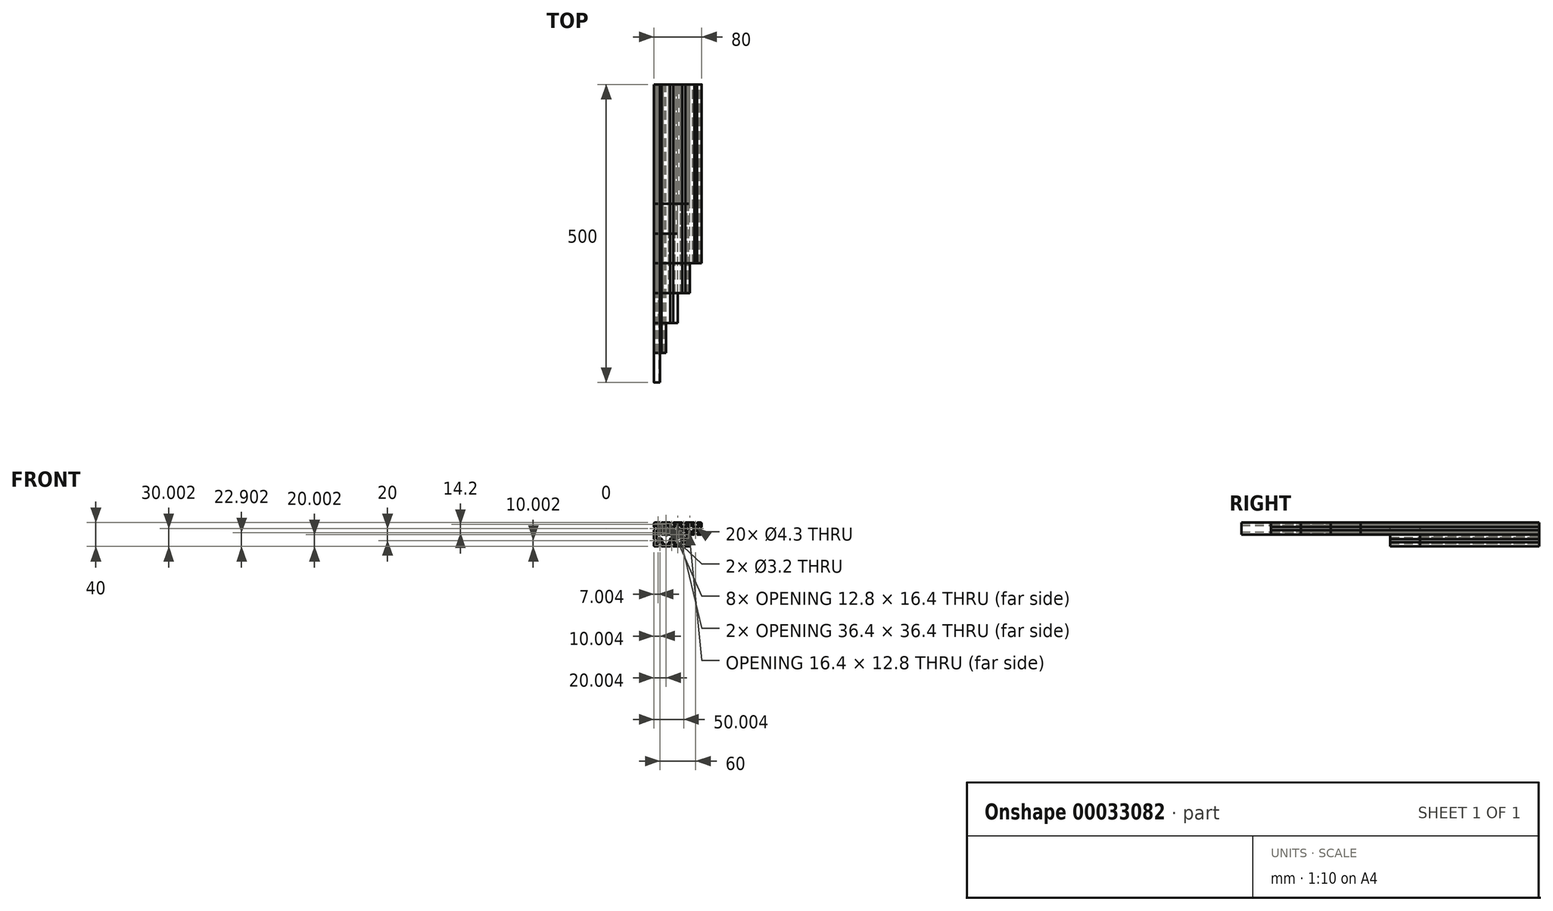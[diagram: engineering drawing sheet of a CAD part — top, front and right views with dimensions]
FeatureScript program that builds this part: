
annotation { "Feature Type Name" : "Feature", "Feature Type Description" : "" }
export const myFeature = defineFeature(function(context is Context, id is Id, definition is map)
    precondition{}
    {
        {
            var Q0;
            Q0=qCreatedBy(makeId("Front.planeOp"),FACE);
            var sketch = newSketch(context, id + "F0", { "sketchPlane" : qUnion([Q0])});
            skLineSegment(sketch, "E0.rect.bottom", {"start": v(-15.79, 10) * mm, "end": v(-10.29, 10) * mm});
            skLineSegment(sketch, "E0.rect.top", {"start": v(-15.79, -10) * mm, "end": v(-10.29, -10) * mm});
            skLineSegment(sketch, "E0.rect.left", {"start": v(-17.29, 8.5) * mm, "end": v(-17.29, 3) * mm});
            skLineSegment(sketch, "E0.rect.right", {"start": v(2.71, 8.5) * mm, "end": v(2.71, 3) * mm});
            skPoint(sketch, "E0.rect.middle", {"position": v(-7.29, 0) * mm});
            skCircle(sketch, "E1", {"center": v(-7.29, 0) * mm, "radius": 2.15 * mm});
            skPoint(sketch, "E2.visualSharp", {"position": v(-17.29, 10) * mm});
            skArc(sketch, "E2.filletArc", {"start": v(-15.79, 10) * mm, "mid": v(-16.85, 9.56) * mm, "end": v(-17.29, 8.5) * mm});
            skPoint(sketch, "E3.visualSharp", {"position": v(2.71, 10) * mm});
            skArc(sketch, "E3.filletArc", {"start": v(2.71, 8.5) * mm, "mid": v(2.27, 9.56) * mm, "end": v(1.21, 10) * mm});
            skPoint(sketch, "E4.visualSharp", {"position": v(2.71, -10) * mm});
            skArc(sketch, "E4.filletArc", {"start": v(1.21, -10) * mm, "mid": v(2.27, -9.56) * mm, "end": v(2.71, -8.5) * mm});
            skPoint(sketch, "E5.visualSharp", {"position": v(-17.29, -10) * mm});
            skArc(sketch, "E5.filletArc", {"start": v(-17.29, -8.5) * mm, "mid": v(-16.85, -9.56) * mm, "end": v(-15.79, -10) * mm});
            skLineSegment(sketch, "E6.rect.bottom", {"start": v(-15.74, 2.5) * mm, "end": v(-16.79, 2.5) * mm});
            skLineSegment(sketch, "E6.rect.top", {"start": v(-15.74, -2.5) * mm, "end": v(-16.79, -2.5) * mm});
            skLineSegment(sketch, "E6.rect.left", {"start": v(-10.89, 1.88) * mm, "end": v(-10.89, -1.88) * mm});
            skLineSegment(sketch, "E6.rect.right", {"start": v(-23.69, 2.5) * mm, "end": v(-23.69, -2.5) * mm});
            skPoint(sketch, "E6.rect.middle", {"position": v(-17.29, 0) * mm});
            skLineSegment(sketch, "E7.rect.bottom", {"start": v(-9.79, 16.4) * mm, "end": v(-4.79, 16.4) * mm});
            skLineSegment(sketch, "E7.rect.top", {"start": v(-9.16, 3.6) * mm, "end": v(-5.4, 3.6) * mm});
            skLineSegment(sketch, "E7.rect.left", {"start": v(-9.79, 9.5) * mm, "end": v(-9.79, 8.45) * mm});
            skLineSegment(sketch, "E7.rect.right", {"start": v(-4.79, 9.5) * mm, "end": v(-4.79, 8.45) * mm});
            skPoint(sketch, "E7.rect.middle", {"position": v(-7.29, 10) * mm});
            skLineSegment(sketch, "E8", {"start": v(-17.29, 10) * mm, "end": v(2.71, -10) * mm, "construction": true});
            skLineSegment(sketch, "E9", {"start": v(4.71, 8.2) * mm, "end": v(-4.79, 8.2) * mm, "construction": true});
            skLineSegment(sketch, "E10", {"start": v(-15.49, 13.5) * mm, "end": v(-15.49, -13.73) * mm, "construction": true});
            skLineSegment(sketch, "E11.0.MirrorCS", {"start": v(1.16, 2.5) * mm, "end": v(2.21, 2.5) * mm});
            skLineSegment(sketch, "E12.0.MirrorCS", {"start": v(1.16, -2.5) * mm, "end": v(2.21, -2.5) * mm});
            skLineSegment(sketch, "E13.0.MirrorCS", {"start": v(-3.69, 1.88) * mm, "end": v(-3.69, -1.88) * mm});
            skLineSegment(sketch, "E14.0.MirrorCS", {"start": v(0.91, 13.5) * mm, "end": v(0.91, -13.73) * mm, "construction": true});
            skLineSegment(sketch, "E15.0.MirrorCS", {"start": v(-4.79, -9.5) * mm, "end": v(-4.79, -8.45) * mm});
            skLineSegment(sketch, "E16.0.MirrorCS", {"start": v(-9.79, -9.5) * mm, "end": v(-9.79, -8.45) * mm});
            skLineSegment(sketch, "E17.0.MirrorCS", {"start": v(-9.16, -3.6) * mm, "end": v(-5.4, -3.6) * mm});
            skLineSegment(sketch, "E18.0.MirrorCS", {"start": v(4.71, -8.2) * mm, "end": v(-18.65, -8.2) * mm, "construction": true});
            skLineSegment(sketch, "E19.0.MirrorCS", {"start": v(-17.29, -10) * mm, "end": v(2.71, 10) * mm, "construction": true});
            skLineSegment(sketch, "E20", {"start": v(-10.23, 4.04) * mm, "end": v(-12.5, 6.32) * mm});
            skLineSegment(sketch, "E21", {"start": v(-11.33, 2.94) * mm, "end": v(-13.6, 5.22) * mm});
            skLineSegment(sketch, "E22", {"start": v(-11.33, -2.94) * mm, "end": v(-13.6, -5.22) * mm});
            skLineSegment(sketch, "E23", {"start": v(-10.23, -4.04) * mm, "end": v(-12.5, -6.32) * mm});
            skLineSegment(sketch, "E24", {"start": v(-4.35, -4.04) * mm, "end": v(-2.06, -6.32) * mm});
            skLineSegment(sketch, "E25", {"start": v(-3.25, -2.94) * mm, "end": v(-0.96, -5.22) * mm});
            skLineSegment(sketch, "E26", {"start": v(-3.25, 2.94) * mm, "end": v(-0.96, 5.22) * mm});
            skLineSegment(sketch, "E27", {"start": v(-4.35, 4.04) * mm, "end": v(-2.06, 6.32) * mm});
            skLineSegment(sketch, "E28", {"start": v(-2.84, 8.2) * mm, "end": v(-4.54, 8.2) * mm});
            skLineSegment(sketch, "E29", {"start": v(-10.04, 8.2) * mm, "end": v(-11.73, 8.2) * mm});
            skLineSegment(sketch, "E30", {"start": v(-15.49, 4.45) * mm, "end": v(-15.49, 2.75) * mm});
            skLineSegment(sketch, "E31", {"start": v(-15.49, -2.75) * mm, "end": v(-15.49, -4.44) * mm});
            skLineSegment(sketch, "E32", {"start": v(-11.73, -8.2) * mm, "end": v(-10.04, -8.2) * mm});
            skLineSegment(sketch, "E33", {"start": v(-4.54, -8.2) * mm, "end": v(-2.84, -8.2) * mm});
            skLineSegment(sketch, "E34", {"start": v(0.91, -4.44) * mm, "end": v(0.91, -2.75) * mm});
            skLineSegment(sketch, "E35", {"start": v(0.91, 2.75) * mm, "end": v(0.91, 4.45) * mm});
            skLineSegment(sketch, "E36.trimOffspring", {"start": v(-17.29, -3) * mm, "end": v(-17.29, -8.5) * mm});
            skLineSegment(sketch, "E37.trimOffspring", {"start": v(-4.29, 10) * mm, "end": v(1.21, 10) * mm});
            skLineSegment(sketch, "E38.trimOffspring", {"start": v(2.71, -3) * mm, "end": v(2.71, -8.5) * mm});
            skLineSegment(sketch, "E39.trimOffspring", {"start": v(-9.79, 8.2) * mm, "end": v(-18.65, 8.2) * mm, "construction": true});
            skLineSegment(sketch, "E40.trimOffspring", {"start": v(-4.29, -10) * mm, "end": v(1.21, -10) * mm});
            skPoint(sketch, "E41.0.MirrorCS.end.orphan", {"position": v(-4.79, -16.4) * mm});
            skPoint(sketch, "E41.0.MirrorCS.start.orphan", {"position": v(-9.79, -16.4) * mm});
            skPoint(sketch, "E42.visualSharp", {"position": v(-9.79, 10) * mm});
            skArc(sketch, "E42.filletArc", {"start": v(-9.79, 9.5) * mm, "mid": v(-9.93, 9.86) * mm, "end": v(-10.29, 10) * mm});
            skPoint(sketch, "E43.visualSharp", {"position": v(-4.79, 10) * mm});
            skArc(sketch, "E43.filletArc", {"start": v(-4.29, 10) * mm, "mid": v(-4.64, 9.86) * mm, "end": v(-4.79, 9.5) * mm});
            skPoint(sketch, "E44.visualSharp", {"position": v(2.71, 2.5) * mm});
            skArc(sketch, "E44.filletArc", {"start": v(2.21, 2.5) * mm, "mid": v(2.57, 2.65) * mm, "end": v(2.71, 3) * mm});
            skPoint(sketch, "E45.visualSharp", {"position": v(2.71, -2.5) * mm});
            skArc(sketch, "E45.filletArc", {"start": v(2.71, -3) * mm, "mid": v(2.57, -2.64) * mm, "end": v(2.21, -2.5) * mm});
            skPoint(sketch, "E46.visualSharp", {"position": v(-4.79, -10) * mm});
            skArc(sketch, "E46.filletArc", {"start": v(-4.79, -9.5) * mm, "mid": v(-4.64, -9.85) * mm, "end": v(-4.29, -10) * mm});
            skPoint(sketch, "E47.visualSharp", {"position": v(-9.79, -10) * mm});
            skArc(sketch, "E47.filletArc", {"start": v(-10.29, -10) * mm, "mid": v(-9.93, -9.85) * mm, "end": v(-9.79, -9.5) * mm});
            skPoint(sketch, "E48.visualSharp", {"position": v(-17.29, -2.5) * mm});
            skArc(sketch, "E48.filletArc", {"start": v(-16.79, -2.5) * mm, "mid": v(-17.14, -2.64) * mm, "end": v(-17.29, -3) * mm});
            skPoint(sketch, "E49.visualSharp", {"position": v(-17.29, 2.5) * mm});
            skArc(sketch, "E49.filletArc", {"start": v(-17.29, 3) * mm, "mid": v(-17.14, 2.65) * mm, "end": v(-16.79, 2.5) * mm});
            skPoint(sketch, "E50.visualSharp", {"position": v(-9.79, 8.2) * mm});
            skArc(sketch, "E50.filletArc", {"start": v(-10.04, 8.2) * mm, "mid": v(-9.86, 8.28) * mm, "end": v(-9.79, 8.45) * mm});
            skPoint(sketch, "E51.visualSharp", {"position": v(-4.79, 8.2) * mm});
            skArc(sketch, "E51.filletArc", {"start": v(-4.79, 8.45) * mm, "mid": v(-4.71, 8.28) * mm, "end": v(-4.54, 8.2) * mm});
            skPoint(sketch, "E52.visualSharp", {"position": v(0.91, 2.5) * mm});
            skArc(sketch, "E52.filletArc", {"start": v(0.91, 2.75) * mm, "mid": v(0.99, 2.58) * mm, "end": v(1.16, 2.5) * mm});
            skPoint(sketch, "E53.visualSharp", {"position": v(0.91, -2.5) * mm});
            skArc(sketch, "E53.filletArc", {"start": v(1.16, -2.5) * mm, "mid": v(0.99, -2.57) * mm, "end": v(0.91, -2.75) * mm});
            skPoint(sketch, "E54.visualSharp", {"position": v(-4.79, -8.2) * mm});
            skArc(sketch, "E54.filletArc", {"start": v(-4.54, -8.2) * mm, "mid": v(-4.71, -8.27) * mm, "end": v(-4.79, -8.45) * mm});
            skPoint(sketch, "E55.visualSharp", {"position": v(-9.79, -8.2) * mm});
            skArc(sketch, "E55.filletArc", {"start": v(-9.79, -8.45) * mm, "mid": v(-9.86, -8.27) * mm, "end": v(-10.04, -8.2) * mm});
            skPoint(sketch, "E56.visualSharp", {"position": v(-15.49, -2.5) * mm});
            skArc(sketch, "E56.filletArc", {"start": v(-15.49, -2.75) * mm, "mid": v(-15.56, -2.57) * mm, "end": v(-15.74, -2.5) * mm});
            skPoint(sketch, "E57.visualSharp", {"position": v(-15.49, 2.5) * mm});
            skArc(sketch, "E57.filletArc", {"start": v(-15.74, 2.5) * mm, "mid": v(-15.56, 2.58) * mm, "end": v(-15.49, 2.75) * mm});
            skPoint(sketch, "E58.visualSharp", {"position": v(-14.39, 8.2) * mm});
            skArc(sketch, "E58.filletArc", {"start": v(-11.73, 8.2) * mm, "mid": v(-12.75, 7.52) * mm, "end": v(-12.5, 6.32) * mm});
            skPoint(sketch, "E59.visualSharp", {"position": v(-0.19, 8.2) * mm});
            skArc(sketch, "E59.filletArc", {"start": v(-2.06, 6.32) * mm, "mid": v(-1.83, 7.52) * mm, "end": v(-2.84, 8.2) * mm});
            skPoint(sketch, "E60.visualSharp", {"position": v(0.91, 7.1) * mm});
            skArc(sketch, "E60.filletArc", {"start": v(0.91, 4.45) * mm, "mid": v(0.23, 5.46) * mm, "end": v(-0.96, 5.22) * mm});
            skPoint(sketch, "E61.visualSharp", {"position": v(0.91, -7.1) * mm});
            skArc(sketch, "E61.filletArc", {"start": v(-0.96, -5.22) * mm, "mid": v(0.23, -5.46) * mm, "end": v(0.91, -4.44) * mm});
            skPoint(sketch, "E62.visualSharp", {"position": v(-0.19, -8.2) * mm});
            skArc(sketch, "E62.filletArc", {"start": v(-2.84, -8.2) * mm, "mid": v(-1.83, -7.52) * mm, "end": v(-2.06, -6.32) * mm});
            skPoint(sketch, "E63.visualSharp", {"position": v(-14.39, -8.2) * mm});
            skArc(sketch, "E63.filletArc", {"start": v(-12.5, -6.32) * mm, "mid": v(-12.75, -7.52) * mm, "end": v(-11.73, -8.2) * mm});
            skPoint(sketch, "E64.visualSharp", {"position": v(-15.49, -7.1) * mm});
            skArc(sketch, "E64.filletArc", {"start": v(-15.49, -4.44) * mm, "mid": v(-14.8, -5.46) * mm, "end": v(-13.6, -5.22) * mm});
            skPoint(sketch, "E65.visualSharp", {"position": v(-15.49, 7.1) * mm});
            skArc(sketch, "E65.filletArc", {"start": v(-13.6, 5.22) * mm, "mid": v(-14.8, 5.46) * mm, "end": v(-15.49, 4.45) * mm});
            skPoint(sketch, "E66.visualSharp", {"position": v(-9.79, 3.6) * mm});
            skArc(sketch, "E66.filletArc", {"start": v(-10.23, 4.04) * mm, "mid": v(-9.74, 3.72) * mm, "end": v(-9.16, 3.6) * mm});
            skPoint(sketch, "E67.visualSharp", {"position": v(-4.79, 3.6) * mm});
            skArc(sketch, "E67.filletArc", {"start": v(-5.4, 3.6) * mm, "mid": v(-4.83, 3.72) * mm, "end": v(-4.35, 4.04) * mm});
            skPoint(sketch, "E68.visualSharp", {"position": v(-3.69, 2.5) * mm});
            skArc(sketch, "E68.filletArc", {"start": v(-3.25, 2.94) * mm, "mid": v(-3.57, 2.45) * mm, "end": v(-3.69, 1.88) * mm});
            skPoint(sketch, "E69.visualSharp", {"position": v(-3.69, -2.5) * mm});
            skArc(sketch, "E69.filletArc", {"start": v(-3.69, -1.88) * mm, "mid": v(-3.57, -2.45) * mm, "end": v(-3.25, -2.94) * mm});
            skPoint(sketch, "E70.visualSharp", {"position": v(-10.89, -2.5) * mm});
            skArc(sketch, "E70.filletArc", {"start": v(-11.33, -2.94) * mm, "mid": v(-11, -2.45) * mm, "end": v(-10.89, -1.88) * mm});
            skPoint(sketch, "E71.visualSharp", {"position": v(-10.89, 2.5) * mm});
            skArc(sketch, "E71.filletArc", {"start": v(-10.89, 1.88) * mm, "mid": v(-11, 2.45) * mm, "end": v(-11.33, 2.94) * mm});
            skPoint(sketch, "E72.visualSharp", {"position": v(-9.79, -3.6) * mm});
            skArc(sketch, "E72.filletArc", {"start": v(-9.16, -3.6) * mm, "mid": v(-9.74, -3.71) * mm, "end": v(-10.23, -4.04) * mm});
            skPoint(sketch, "E73.visualSharp", {"position": v(-4.79, -3.6) * mm});
            skArc(sketch, "E73.filletArc", {"start": v(-4.35, -4.04) * mm, "mid": v(-4.83, -3.71) * mm, "end": v(-5.4, -3.6) * mm});
            skLineSegment(sketch, "E74", {"start": v(-15.79, 10) * mm, "end": v(-8.79, 10) * mm});
            skLineSegment(sketch, "E75.0.MirrorCS", {"start": v(-15.79, -10) * mm, "end": v(-8.79, -10) * mm});
            skLineSegment(sketch, "E76", {"start": v(-7.29, 8.5) * mm, "end": v(-7.29, -8.5) * mm});
            skArc(sketch, "E77.filletArc", {"start": v(-7.29, 8.5) * mm, "mid": v(-7.73, 9.56) * mm, "end": v(-8.79, 10) * mm});
            skPoint(sketch, "E78.visualSharp", {"position": v(-7.29, -10) * mm});
            skArc(sketch, "E78.filletArc", {"start": v(-8.79, -10) * mm, "mid": v(-7.73, -9.56) * mm, "end": v(-7.29, -8.5) * mm});
            skLineSegment(sketch, "E79", {"start": v(-15.49, 7.1) * mm, "end": v(0.91, 7.1) * mm, "construction": true});
            skLineSegment(sketch, "E80", {"start": v(-15.49, -7.1) * mm, "end": v(0.91, -7.1) * mm, "construction": true});
            skLineSegment(sketch, "E81", {"start": v(-10.29, 9.5) * mm, "end": v(-10.29, -9.5) * mm, "construction": true});
            skCircle(sketch, "E82", {"center": v(-10.29, 7.1) * mm, "radius": 1.6 * mm});
            skCircle(sketch, "E83", {"center": v(-10.29, -7.1) * mm, "radius": 1.6 * mm});
            skLineSegment(sketch, "E84", {"start": v(2.71, 10) * mm, "end": v(2.71, -10) * mm, "construction": true});
            skLineSegment(sketch, "E85.0.MirrorCS", {"start": v(9.71, 10) * mm, "end": v(4.21, 10) * mm});
            skArc(sketch, "E86.0.MirrorCS", {"start": v(9.71, 10) * mm, "mid": v(10.07, 9.86) * mm, "end": v(10.21, 9.5) * mm});
            skLineSegment(sketch, "E87.0.MirrorCS", {"start": v(10.21, 9.5) * mm, "end": v(10.21, 8.45) * mm});
            skArc(sketch, "E88.0.MirrorCS", {"start": v(10.21, 8.45) * mm, "mid": v(10.14, 8.28) * mm, "end": v(9.96, 8.2) * mm});
            skLineSegment(sketch, "E89.0.MirrorCS", {"start": v(8.27, 8.2) * mm, "end": v(9.96, 8.2) * mm});
            skArc(sketch, "E90.0.MirrorCS", {"start": v(7.5, 6.32) * mm, "mid": v(7.25, 7.52) * mm, "end": v(8.27, 8.2) * mm});
            skLineSegment(sketch, "E91.0.MirrorCS", {"start": v(9.77, 4.04) * mm, "end": v(7.5, 6.32) * mm});
            skArc(sketch, "E92.0.MirrorCS", {"start": v(10.84, 3.6) * mm, "mid": v(10.26, 3.72) * mm, "end": v(9.77, 4.04) * mm});
            skLineSegment(sketch, "E93.0.MirrorCS", {"start": v(14.6, 3.6) * mm, "end": v(10.84, 3.6) * mm});
            skArc(sketch, "E94.0.MirrorCS", {"start": v(15.65, 4.04) * mm, "mid": v(15.17, 3.72) * mm, "end": v(14.6, 3.6) * mm});
            skLineSegment(sketch, "E95.0.MirrorCS", {"start": v(15.65, 4.04) * mm, "end": v(17.94, 6.32) * mm});
            skArc(sketch, "E96.0.MirrorCS", {"start": v(17.16, 8.2) * mm, "mid": v(18.17, 7.52) * mm, "end": v(17.94, 6.32) * mm});
            skLineSegment(sketch, "E97.0.MirrorCS", {"start": v(15.46, 8.2) * mm, "end": v(17.16, 8.2) * mm});
            skArc(sketch, "E98.0.MirrorCS", {"start": v(15.46, 8.2) * mm, "mid": v(15.29, 8.28) * mm, "end": v(15.21, 8.45) * mm});
            skLineSegment(sketch, "E99.0.MirrorCS", {"start": v(15.21, 9.5) * mm, "end": v(15.21, 8.45) * mm});
            skArc(sketch, "E100.0.MirrorCS", {"start": v(15.21, 9.5) * mm, "mid": v(15.36, 9.86) * mm, "end": v(15.71, 10) * mm});
            skLineSegment(sketch, "E101.0.MirrorCS", {"start": v(21.21, 10) * mm, "end": v(15.71, 10) * mm});
            skArc(sketch, "E102.0.MirrorCS", {"start": v(21.21, 10) * mm, "mid": v(22.27, 9.56) * mm, "end": v(22.71, 8.5) * mm});
            skLineSegment(sketch, "E103.0.MirrorCS", {"start": v(22.71, 8.5) * mm, "end": v(22.71, 3) * mm});
            skArc(sketch, "E104.0.MirrorCS", {"start": v(22.71, 3) * mm, "mid": v(22.57, 2.65) * mm, "end": v(22.21, 2.5) * mm});
            skLineSegment(sketch, "E105.0.MirrorCS", {"start": v(21.16, 2.5) * mm, "end": v(22.21, 2.5) * mm});
            skArc(sketch, "E106.0.MirrorCS", {"start": v(21.16, 2.5) * mm, "mid": v(20.99, 2.58) * mm, "end": v(20.91, 2.75) * mm});
            skLineSegment(sketch, "E107.0.MirrorCS", {"start": v(20.91, 4.45) * mm, "end": v(20.91, 2.75) * mm});
            skArc(sketch, "E108.0.MirrorCS", {"start": v(19.04, 5.22) * mm, "mid": v(20.23, 5.46) * mm, "end": v(20.91, 4.45) * mm});
            skLineSegment(sketch, "E109.0.MirrorCS", {"start": v(16.75, 2.94) * mm, "end": v(19.04, 5.22) * mm});
            skArc(sketch, "E110.0.MirrorCS", {"start": v(16.31, 1.88) * mm, "mid": v(16.43, 2.45) * mm, "end": v(16.75, 2.94) * mm});
            skLineSegment(sketch, "E111.0.MirrorCS", {"start": v(16.31, 1.88) * mm, "end": v(16.31, -1.88) * mm});
            skArc(sketch, "E112.0.MirrorCS", {"start": v(16.75, -2.94) * mm, "mid": v(16.43, -2.45) * mm, "end": v(16.31, -1.88) * mm});
            skLineSegment(sketch, "E113.0.MirrorCS", {"start": v(16.75, -2.94) * mm, "end": v(19.04, -5.22) * mm});
            skArc(sketch, "E114.0.MirrorCS", {"start": v(20.91, -4.44) * mm, "mid": v(20.23, -5.46) * mm, "end": v(19.04, -5.22) * mm});
            skLineSegment(sketch, "E115.0.MirrorCS", {"start": v(20.91, -2.75) * mm, "end": v(20.91, -4.44) * mm});
            skArc(sketch, "E116.0.MirrorCS", {"start": v(20.91, -2.75) * mm, "mid": v(20.99, -2.57) * mm, "end": v(21.16, -2.5) * mm});
            skLineSegment(sketch, "E117.0.MirrorCS", {"start": v(21.16, -2.5) * mm, "end": v(22.21, -2.5) * mm});
            skArc(sketch, "E118.0.MirrorCS", {"start": v(22.21, -2.5) * mm, "mid": v(22.57, -2.64) * mm, "end": v(22.71, -3) * mm});
            skLineSegment(sketch, "E119.0.MirrorCS", {"start": v(22.71, -3) * mm, "end": v(22.71, -8.5) * mm});
            skArc(sketch, "E120.0.MirrorCS", {"start": v(22.71, -8.5) * mm, "mid": v(22.27, -9.56) * mm, "end": v(21.21, -10) * mm});
            skLineSegment(sketch, "E121.0.MirrorCS", {"start": v(21.21, -10) * mm, "end": v(15.71, -10) * mm});
            skArc(sketch, "E122.0.MirrorCS", {"start": v(15.71, -10) * mm, "mid": v(15.36, -9.85) * mm, "end": v(15.21, -9.5) * mm});
            skLineSegment(sketch, "E123.0.MirrorCS", {"start": v(15.21, -9.5) * mm, "end": v(15.21, -8.45) * mm});
            skArc(sketch, "E124.0.MirrorCS", {"start": v(15.21, -8.45) * mm, "mid": v(15.29, -8.27) * mm, "end": v(15.46, -8.2) * mm});
            skLineSegment(sketch, "E125.0.MirrorCS", {"start": v(17.16, -8.2) * mm, "end": v(15.46, -8.2) * mm});
            skArc(sketch, "E126.0.MirrorCS", {"start": v(17.94, -6.32) * mm, "mid": v(18.17, -7.52) * mm, "end": v(17.16, -8.2) * mm});
            skLineSegment(sketch, "E127.0.MirrorCS", {"start": v(15.65, -4.04) * mm, "end": v(17.94, -6.32) * mm});
            skArc(sketch, "E128.0.MirrorCS", {"start": v(14.6, -3.6) * mm, "mid": v(15.17, -3.71) * mm, "end": v(15.65, -4.04) * mm});
            skLineSegment(sketch, "E129.0.MirrorCS", {"start": v(14.6, -3.6) * mm, "end": v(10.84, -3.6) * mm});
            skArc(sketch, "E130.0.MirrorCS", {"start": v(9.77, -4.04) * mm, "mid": v(10.26, -3.71) * mm, "end": v(10.84, -3.6) * mm});
            skLineSegment(sketch, "E131.0.MirrorCS", {"start": v(9.77, -4.04) * mm, "end": v(7.5, -6.32) * mm});
            skArc(sketch, "E132.0.MirrorCS", {"start": v(8.27, -8.2) * mm, "mid": v(7.25, -7.52) * mm, "end": v(7.5, -6.32) * mm});
            skLineSegment(sketch, "E133.0.MirrorCS", {"start": v(9.96, -8.2) * mm, "end": v(8.27, -8.2) * mm});
            skArc(sketch, "E134.0.MirrorCS", {"start": v(9.96, -8.2) * mm, "mid": v(10.14, -8.27) * mm, "end": v(10.21, -8.45) * mm});
            skLineSegment(sketch, "E135.0.MirrorCS", {"start": v(10.21, -9.5) * mm, "end": v(10.21, -8.45) * mm});
            skArc(sketch, "E136.0.MirrorCS", {"start": v(10.21, -9.5) * mm, "mid": v(10.07, -9.85) * mm, "end": v(9.71, -10) * mm});
            skLineSegment(sketch, "E137.0.MirrorCS", {"start": v(9.71, -10) * mm, "end": v(4.21, -10) * mm});
            skCircle(sketch, "E138.0.MirrorC", {"center": v(12.71, 0) * mm, "radius": 2.15 * mm});
            skLineSegment(sketch, "E139.0.MirrorCS", {"start": v(9.11, 1.88) * mm, "end": v(9.11, -1.88) * mm});
            skArc(sketch, "E140.0.MirrorCS", {"start": v(8.67, 2.94) * mm, "mid": v(9, 2.45) * mm, "end": v(9.11, 1.88) * mm});
            skArc(sketch, "E141.0.MirrorCS", {"start": v(9.11, -1.88) * mm, "mid": v(9, -2.45) * mm, "end": v(8.67, -2.94) * mm});
            skLineSegment(sketch, "E142.0.MirrorCS", {"start": v(8.67, -2.94) * mm, "end": v(6.4, -5.22) * mm});
            skLineSegment(sketch, "E143.0.MirrorCS", {"start": v(8.67, 2.94) * mm, "end": v(6.4, 5.22) * mm});
            skArc(sketch, "E144.0.MirrorCS", {"start": v(4.51, 4.45) * mm, "mid": v(5.2, 5.46) * mm, "end": v(6.4, 5.22) * mm});
            skArc(sketch, "E145.0.MirrorCS", {"start": v(6.4, -5.22) * mm, "mid": v(5.2, -5.46) * mm, "end": v(4.51, -4.44) * mm});
            skLineSegment(sketch, "E146.0.MirrorCS", {"start": v(4.51, 13.5) * mm, "end": v(4.51, -13.73) * mm, "construction": true});
            skLineSegment(sketch, "E147.0.MirrorCS", {"start": v(20.91, 13.5) * mm, "end": v(20.91, -13.73) * mm, "construction": true});
            skLineSegment(sketch, "E148.0.MirrorCS", {"start": v(0.71, -8.2) * mm, "end": v(24.08, -8.2) * mm, "construction": true});
            skLineSegment(sketch, "E149.0.MirrorCS", {"start": v(15.21, 8.2) * mm, "end": v(24.08, 8.2) * mm, "construction": true});
            skLineSegment(sketch, "E150.0.MirrorCS", {"start": v(0.71, 8.2) * mm, "end": v(10.21, 8.2) * mm, "construction": true});
            skPoint(sketch, "E151.orphan", {"position": v(14.21, 10) * mm});
            skPoint(sketch, "E152.orphan", {"position": v(14.21, -10) * mm});
            skLineSegment(sketch, "E153", {"start": v(4.21, 10) * mm, "end": v(1.21, 10) * mm});
            skLineSegment(sketch, "E154", {"start": v(4.21, -10) * mm, "end": v(1.21, -10) * mm});
            skLineSegment(sketch, "E155", {"start": v(-0.96, 5.22) * mm, "end": v(1.57, 7.76) * mm});
            skLineSegment(sketch, "E156", {"start": v(6.4, 5.22) * mm, "end": v(3.85, 7.76) * mm});
            skLineSegment(sketch, "E157", {"start": v(2.8, 8.2) * mm, "end": v(2.64, 8.2) * mm});
            skLineSegment(sketch, "E158", {"start": v(-0.96, -5.22) * mm, "end": v(1.57, -7.76) * mm});
            skLineSegment(sketch, "E159", {"start": v(6.4, -5.22) * mm, "end": v(3.85, -7.76) * mm});
            skLineSegment(sketch, "E160", {"start": v(2.8, -8.2) * mm, "end": v(2.64, -8.2) * mm});
            skPoint(sketch, "E161.visualSharp", {"position": v(2.01, 8.2) * mm});
            skArc(sketch, "E161.filletArc", {"start": v(2.64, 8.2) * mm, "mid": v(2.06, 8.09) * mm, "end": v(1.57, 7.76) * mm});
            skPoint(sketch, "E162.visualSharp", {"position": v(3.41, 8.2) * mm});
            skArc(sketch, "E162.filletArc", {"start": v(3.85, 7.76) * mm, "mid": v(3.37, 8.09) * mm, "end": v(2.8, 8.2) * mm});
            skPoint(sketch, "E163.visualSharp", {"position": v(3.41, -8.2) * mm});
            skArc(sketch, "E163.filletArc", {"start": v(2.8, -8.2) * mm, "mid": v(3.37, -8.08) * mm, "end": v(3.85, -7.76) * mm});
            skPoint(sketch, "E164.visualSharp", {"position": v(2.01, -8.2) * mm});
            skArc(sketch, "E164.filletArc", {"start": v(1.57, -7.76) * mm, "mid": v(2.06, -8.08) * mm, "end": v(2.64, -8.2) * mm});
            skSolve(sketch);
        }
        {
            var Q0;
            Q0=qCreatedBy(makeId("Front.planeOp"),FACE);
            var sketch = newSketch(context, id + "F1", { "sketchPlane" : qUnion([Q0])});
            skLineSegment(sketch, "E165.0", {"start": v(-17.29, 8.5) * mm, "end": v(-17.29, 3) * mm});
            skArc(sketch, "E166.0", {"start": v(-15.79, 10) * mm, "mid": v(-16.85, 9.56) * mm, "end": v(-17.29, 8.5) * mm});
            skArc(sketch, "E167.0", {"start": v(-7.29, 8.5) * mm, "mid": v(-7.73, 9.56) * mm, "end": v(-8.79, 10) * mm});
            skLineSegment(sketch, "E168.0", {"start": v(-7.29, 8.5) * mm, "end": v(-7.29, -8.5) * mm});
            skArc(sketch, "E169.0", {"start": v(-8.79, -10) * mm, "mid": v(-7.73, -9.56) * mm, "end": v(-7.29, -8.5) * mm});
            skArc(sketch, "E170.0", {"start": v(-17.29, -8.5) * mm, "mid": v(-16.85, -9.56) * mm, "end": v(-15.79, -10) * mm});
            skLineSegment(sketch, "E171.0", {"start": v(-17.29, -3) * mm, "end": v(-17.29, -8.5) * mm});
            skArc(sketch, "E172.0", {"start": v(-17.29, 3) * mm, "mid": v(-17.14, 2.65) * mm, "end": v(-16.79, 2.5) * mm});
            skArc(sketch, "E173.0", {"start": v(-16.79, -2.5) * mm, "mid": v(-17.14, -2.64) * mm, "end": v(-17.29, -3) * mm});
            skLineSegment(sketch, "E174.0", {"start": v(-15.74, -2.5) * mm, "end": v(-16.79, -2.5) * mm});
            skLineSegment(sketch, "E175.0", {"start": v(-15.74, 2.5) * mm, "end": v(-16.79, 2.5) * mm});
            skArc(sketch, "E176.0", {"start": v(-15.74, 2.5) * mm, "mid": v(-15.56, 2.58) * mm, "end": v(-15.49, 2.75) * mm});
            skArc(sketch, "E177.0", {"start": v(-15.49, -2.75) * mm, "mid": v(-15.56, -2.57) * mm, "end": v(-15.74, -2.5) * mm});
            skLineSegment(sketch, "E178.0", {"start": v(-15.49, -2.75) * mm, "end": v(-15.49, -4.44) * mm});
            skLineSegment(sketch, "E179.0", {"start": v(-15.49, 4.45) * mm, "end": v(-15.49, 2.75) * mm});
            skArc(sketch, "E180.0", {"start": v(-13.6, 5.22) * mm, "mid": v(-14.8, 5.46) * mm, "end": v(-15.49, 4.45) * mm});
            skLineSegment(sketch, "E181.0", {"start": v(-11.33, 2.94) * mm, "end": v(-13.6, 5.22) * mm});
            skArc(sketch, "E182.0", {"start": v(-10.89, 1.88) * mm, "mid": v(-11, 2.45) * mm, "end": v(-11.33, 2.94) * mm});
            skLineSegment(sketch, "E183.0", {"start": v(-10.89, 1.88) * mm, "end": v(-10.89, -1.88) * mm});
            skArc(sketch, "E184.0", {"start": v(-11.33, -2.94) * mm, "mid": v(-11, -2.45) * mm, "end": v(-10.89, -1.88) * mm});
            skLineSegment(sketch, "E185.0", {"start": v(-11.33, -2.94) * mm, "end": v(-13.6, -5.22) * mm});
            skArc(sketch, "E186.0", {"start": v(-15.49, -4.44) * mm, "mid": v(-14.8, -5.46) * mm, "end": v(-13.6, -5.22) * mm});
            skCircle(sketch, "E187.0", {"center": v(-10.29, -7.1) * mm, "radius": 1.6 * mm});
            skCircle(sketch, "E188.0", {"center": v(-10.29, 7.1) * mm, "radius": 1.6 * mm});
            skLineSegment(sketch, "E189", {"start": v(-15.79, 10) * mm, "end": v(-8.79, 10) * mm});
            skLineSegment(sketch, "E190", {"start": v(-15.79, -10) * mm, "end": v(-8.79, -10) * mm});
            skSolve(sketch);
        }
        {
            var Q0;
            Q0=qCreatedBy(makeId("Front.planeOp"),FACE);
            var sketch = newSketch(context, id + "F2", { "sketchPlane" : qUnion([Q0])});
            skArc(sketch, "E191.0", {"start": v(-15.79, 10) * mm, "mid": v(-16.85, 9.56) * mm, "end": v(-17.29, 8.5) * mm});
            skLineSegment(sketch, "E192.0", {"start": v(-17.29, 8.5) * mm, "end": v(-17.29, 3) * mm});
            skArc(sketch, "E193.0", {"start": v(-9.79, 9.5) * mm, "mid": v(-9.93, 9.86) * mm, "end": v(-10.29, 10) * mm});
            skLineSegment(sketch, "E194.0", {"start": v(-9.79, 9.5) * mm, "end": v(-9.79, 8.45) * mm});
            skLineSegment(sketch, "E195.0", {"start": v(-10.04, 8.2) * mm, "end": v(-11.73, 8.2) * mm});
            skArc(sketch, "E196.0", {"start": v(-11.73, 8.2) * mm, "mid": v(-12.75, 7.52) * mm, "end": v(-12.5, 6.32) * mm});
            skLineSegment(sketch, "E197.0", {"start": v(-10.23, 4.04) * mm, "end": v(-12.5, 6.32) * mm});
            skArc(sketch, "E198.0", {"start": v(-10.23, 4.04) * mm, "mid": v(-9.74, 3.72) * mm, "end": v(-9.16, 3.6) * mm});
            skLineSegment(sketch, "E199.0", {"start": v(-9.16, 3.6) * mm, "end": v(-5.4, 3.6) * mm});
            skArc(sketch, "E200.0", {"start": v(-5.4, 3.6) * mm, "mid": v(-4.83, 3.72) * mm, "end": v(-4.35, 4.04) * mm});
            skLineSegment(sketch, "E201.0", {"start": v(-4.35, 4.04) * mm, "end": v(-2.06, 6.32) * mm});
            skArc(sketch, "E202.0", {"start": v(-2.06, 6.32) * mm, "mid": v(-1.83, 7.52) * mm, "end": v(-2.84, 8.2) * mm});
            skLineSegment(sketch, "E203.0", {"start": v(-2.84, 8.2) * mm, "end": v(-4.54, 8.2) * mm});
            skArc(sketch, "E204.0", {"start": v(-4.29, 10) * mm, "mid": v(-4.64, 9.86) * mm, "end": v(-4.79, 9.5) * mm});
            skLineSegment(sketch, "E205.0", {"start": v(-4.29, 10) * mm, "end": v(1.21, 10) * mm});
            skArc(sketch, "E206.0", {"start": v(2.71, 8.5) * mm, "mid": v(2.27, 9.56) * mm, "end": v(1.21, 10) * mm});
            skLineSegment(sketch, "E207.0", {"start": v(2.71, 8.5) * mm, "end": v(2.71, 3) * mm});
            skArc(sketch, "E208.0", {"start": v(2.21, 2.5) * mm, "mid": v(2.57, 2.65) * mm, "end": v(2.71, 3) * mm});
            skLineSegment(sketch, "E209.0", {"start": v(1.16, 2.5) * mm, "end": v(2.21, 2.5) * mm});
            skLineSegment(sketch, "E210.0", {"start": v(-15.79, 10) * mm, "end": v(-10.29, 10) * mm});
            skArc(sketch, "E211.0", {"start": v(-17.29, 3) * mm, "mid": v(-17.14, 2.65) * mm, "end": v(-16.79, 2.5) * mm});
            skLineSegment(sketch, "E212.0", {"start": v(-15.74, 2.5) * mm, "end": v(-16.79, 2.5) * mm});
            skArc(sketch, "E213.0", {"start": v(-15.74, 2.5) * mm, "mid": v(-15.56, 2.58) * mm, "end": v(-15.49, 2.75) * mm});
            skLineSegment(sketch, "E213.1", {"start": v(-15.49, 4.45) * mm, "end": v(-15.49, 2.75) * mm});
            skArc(sketch, "E213.2", {"start": v(-13.6, 5.22) * mm, "mid": v(-14.8, 5.46) * mm, "end": v(-15.49, 4.45) * mm});
            skLineSegment(sketch, "E214.0", {"start": v(-11.33, 2.94) * mm, "end": v(-13.6, 5.22) * mm});
            skArc(sketch, "E215.0", {"start": v(-10.89, 1.88) * mm, "mid": v(-11, 2.45) * mm, "end": v(-11.33, 2.94) * mm});
            skLineSegment(sketch, "E216.0", {"start": v(-10.89, 1.88) * mm, "end": v(-10.89, -1.88) * mm});
            skArc(sketch, "E217.0", {"start": v(-11.33, -2.94) * mm, "mid": v(-11, -2.45) * mm, "end": v(-10.89, -1.88) * mm});
            skLineSegment(sketch, "E218.0", {"start": v(-11.33, -2.94) * mm, "end": v(-13.6, -5.22) * mm});
            skArc(sketch, "E219.0", {"start": v(-15.49, -4.44) * mm, "mid": v(-14.8, -5.46) * mm, "end": v(-13.6, -5.22) * mm});
            skLineSegment(sketch, "E220.0", {"start": v(-15.49, -2.75) * mm, "end": v(-15.49, -4.44) * mm});
            skArc(sketch, "E221.0", {"start": v(-15.49, -2.75) * mm, "mid": v(-15.56, -2.57) * mm, "end": v(-15.74, -2.5) * mm});
            skLineSegment(sketch, "E222.0", {"start": v(-15.74, -2.5) * mm, "end": v(-16.79, -2.5) * mm});
            skArc(sketch, "E223.0", {"start": v(-16.79, -2.5) * mm, "mid": v(-17.14, -2.64) * mm, "end": v(-17.29, -3) * mm});
            skLineSegment(sketch, "E224.0", {"start": v(-17.29, -3) * mm, "end": v(-17.29, -8.5) * mm});
            skArc(sketch, "E225.0", {"start": v(-17.29, -8.5) * mm, "mid": v(-16.85, -9.56) * mm, "end": v(-15.79, -10) * mm});
            skLineSegment(sketch, "E226.0", {"start": v(-15.79, -10) * mm, "end": v(-10.29, -10) * mm});
            skArc(sketch, "E227.0", {"start": v(-10.29, -10) * mm, "mid": v(-9.93, -9.85) * mm, "end": v(-9.79, -9.5) * mm});
            skLineSegment(sketch, "E228.0", {"start": v(-9.79, -9.5) * mm, "end": v(-9.79, -8.45) * mm});
            skArc(sketch, "E229.0", {"start": v(-9.79, -8.45) * mm, "mid": v(-9.86, -8.27) * mm, "end": v(-10.04, -8.2) * mm});
            skLineSegment(sketch, "E230.0", {"start": v(-11.73, -8.2) * mm, "end": v(-10.04, -8.2) * mm});
            skArc(sketch, "E231.0", {"start": v(-12.5, -6.32) * mm, "mid": v(-12.75, -7.52) * mm, "end": v(-11.73, -8.2) * mm});
            skLineSegment(sketch, "E232.0", {"start": v(-10.23, -4.04) * mm, "end": v(-12.5, -6.32) * mm});
            skArc(sketch, "E233.0", {"start": v(-9.16, -3.6) * mm, "mid": v(-9.74, -3.71) * mm, "end": v(-10.23, -4.04) * mm});
            skLineSegment(sketch, "E234.0", {"start": v(-9.16, -3.6) * mm, "end": v(-5.4, -3.6) * mm});
            skArc(sketch, "E235.0", {"start": v(-4.35, -4.04) * mm, "mid": v(-4.83, -3.71) * mm, "end": v(-5.4, -3.6) * mm});
            skLineSegment(sketch, "E236.0", {"start": v(-4.35, -4.04) * mm, "end": v(-2.06, -6.32) * mm});
            skArc(sketch, "E237.0", {"start": v(-2.84, -8.2) * mm, "mid": v(-1.83, -7.52) * mm, "end": v(-2.06, -6.32) * mm});
            skLineSegment(sketch, "E238.0", {"start": v(-4.54, -8.2) * mm, "end": v(-2.84, -8.2) * mm});
            skArc(sketch, "E239.0", {"start": v(-4.54, -8.2) * mm, "mid": v(-4.71, -8.27) * mm, "end": v(-4.79, -8.45) * mm});
            skLineSegment(sketch, "E240.0", {"start": v(-4.79, -9.5) * mm, "end": v(-4.79, -8.45) * mm});
            skArc(sketch, "E241.0", {"start": v(-4.79, -9.5) * mm, "mid": v(-4.64, -9.85) * mm, "end": v(-4.29, -10) * mm});
            skLineSegment(sketch, "E242.0", {"start": v(-4.29, -10) * mm, "end": v(1.21, -10) * mm});
            skArc(sketch, "E243.0", {"start": v(1.21, -10) * mm, "mid": v(2.27, -9.56) * mm, "end": v(2.71, -8.5) * mm});
            skLineSegment(sketch, "E244.0", {"start": v(2.71, -3) * mm, "end": v(2.71, -8.5) * mm});
            skArc(sketch, "E245.0", {"start": v(2.71, -3) * mm, "mid": v(2.57, -2.64) * mm, "end": v(2.21, -2.5) * mm});
            skLineSegment(sketch, "E246.0", {"start": v(1.16, -2.5) * mm, "end": v(2.21, -2.5) * mm});
            skArc(sketch, "E247.0", {"start": v(1.16, -2.5) * mm, "mid": v(0.99, -2.57) * mm, "end": v(0.91, -2.75) * mm});
            skLineSegment(sketch, "E248.0", {"start": v(0.91, -4.44) * mm, "end": v(0.91, -2.75) * mm});
            skArc(sketch, "E249.0", {"start": v(-0.96, -5.22) * mm, "mid": v(0.23, -5.46) * mm, "end": v(0.91, -4.44) * mm});
            skLineSegment(sketch, "E250.0", {"start": v(-3.25, -2.94) * mm, "end": v(-0.96, -5.22) * mm});
            skArc(sketch, "E251.0", {"start": v(-3.69, -1.88) * mm, "mid": v(-3.57, -2.45) * mm, "end": v(-3.25, -2.94) * mm});
            skLineSegment(sketch, "E252.0", {"start": v(-3.69, 1.88) * mm, "end": v(-3.69, -1.88) * mm});
            skArc(sketch, "E253.0", {"start": v(-3.25, 2.94) * mm, "mid": v(-3.57, 2.45) * mm, "end": v(-3.69, 1.88) * mm});
            skLineSegment(sketch, "E254.0", {"start": v(-3.25, 2.94) * mm, "end": v(-0.96, 5.22) * mm});
            skArc(sketch, "E255.0", {"start": v(0.91, 4.45) * mm, "mid": v(0.23, 5.46) * mm, "end": v(-0.96, 5.22) * mm});
            skLineSegment(sketch, "E256.0", {"start": v(0.91, 2.75) * mm, "end": v(0.91, 4.45) * mm});
            skArc(sketch, "E257.0", {"start": v(0.91, 2.75) * mm, "mid": v(0.99, 2.58) * mm, "end": v(1.16, 2.5) * mm});
            skLineSegment(sketch, "E258.0", {"start": v(-4.79, 9.5) * mm, "end": v(-4.79, 8.45) * mm});
            skArc(sketch, "E259.0", {"start": v(-4.79, 8.45) * mm, "mid": v(-4.71, 8.28) * mm, "end": v(-4.54, 8.2) * mm});
            skArc(sketch, "E260.0", {"start": v(-10.04, 8.2) * mm, "mid": v(-9.86, 8.28) * mm, "end": v(-9.79, 8.45) * mm});
            skCircle(sketch, "E261.0", {"center": v(-7.29, 0) * mm, "radius": 2.15 * mm});
            skSolve(sketch);
        }
        {
            var Q0;
            Q0=qCreatedBy(makeId("Front.planeOp"),FACE);
            var sketch = newSketch(context, id + "F3", { "sketchPlane" : qUnion([Q0])});
            skArc(sketch, "E262.0", {"start": v(-15.79, 10) * mm, "mid": v(-16.85, 9.56) * mm, "end": v(-17.29, 8.5) * mm});
            skLineSegment(sketch, "E263.0", {"start": v(-15.79, 10) * mm, "end": v(-10.29, 10) * mm});
            skArc(sketch, "E264.0", {"start": v(-9.79, 9.5) * mm, "mid": v(-9.93, 9.86) * mm, "end": v(-10.29, 10) * mm});
            skLineSegment(sketch, "E265.0", {"start": v(-9.79, 9.5) * mm, "end": v(-9.79, 8.45) * mm});
            skArc(sketch, "E266.0", {"start": v(-10.04, 8.2) * mm, "mid": v(-9.86, 8.28) * mm, "end": v(-9.79, 8.45) * mm});
            skLineSegment(sketch, "E267.0", {"start": v(-10.04, 8.2) * mm, "end": v(-11.73, 8.2) * mm});
            skArc(sketch, "E268.0", {"start": v(-11.73, 8.2) * mm, "mid": v(-12.75, 7.52) * mm, "end": v(-12.5, 6.32) * mm});
            skLineSegment(sketch, "E269.0", {"start": v(-10.23, 4.04) * mm, "end": v(-12.5, 6.32) * mm});
            skArc(sketch, "E270.0", {"start": v(-10.23, 4.04) * mm, "mid": v(-9.74, 3.72) * mm, "end": v(-9.16, 3.6) * mm});
            skLineSegment(sketch, "E271.0", {"start": v(-9.16, 3.6) * mm, "end": v(-5.4, 3.6) * mm});
            skArc(sketch, "E272.0", {"start": v(-5.4, 3.6) * mm, "mid": v(-4.83, 3.72) * mm, "end": v(-4.35, 4.04) * mm});
            skLineSegment(sketch, "E273.0", {"start": v(-4.35, 4.04) * mm, "end": v(-2.06, 6.32) * mm});
            skArc(sketch, "E274.0", {"start": v(-2.06, 6.32) * mm, "mid": v(-1.83, 7.52) * mm, "end": v(-2.84, 8.2) * mm});
            skLineSegment(sketch, "E275.0", {"start": v(-2.84, 8.2) * mm, "end": v(-4.54, 8.2) * mm});
            skArc(sketch, "E276.0", {"start": v(-4.79, 8.45) * mm, "mid": v(-4.71, 8.28) * mm, "end": v(-4.54, 8.2) * mm});
            skLineSegment(sketch, "E277.0", {"start": v(-4.79, 9.5) * mm, "end": v(-4.79, 8.45) * mm});
            skArc(sketch, "E278.0", {"start": v(-4.29, 10) * mm, "mid": v(-4.64, 9.86) * mm, "end": v(-4.79, 9.5) * mm});
            skLineSegment(sketch, "E279.0", {"start": v(-17.29, 8.5) * mm, "end": v(-17.29, 3) * mm});
            skArc(sketch, "E280.0", {"start": v(-17.29, 3) * mm, "mid": v(-17.14, 2.65) * mm, "end": v(-16.79, 2.5) * mm});
            skLineSegment(sketch, "E281.0", {"start": v(-15.74, 2.5) * mm, "end": v(-16.79, 2.5) * mm});
            skArc(sketch, "E282.0", {"start": v(-15.74, 2.5) * mm, "mid": v(-15.56, 2.58) * mm, "end": v(-15.49, 2.75) * mm});
            skLineSegment(sketch, "E283.0", {"start": v(-15.49, 4.45) * mm, "end": v(-15.49, 2.75) * mm});
            skArc(sketch, "E284.0", {"start": v(-13.6, 5.22) * mm, "mid": v(-14.8, 5.46) * mm, "end": v(-15.49, 4.45) * mm});
            skLineSegment(sketch, "E285.0", {"start": v(-11.33, 2.94) * mm, "end": v(-13.6, 5.22) * mm});
            skArc(sketch, "E286.0", {"start": v(-10.89, 1.88) * mm, "mid": v(-11, 2.45) * mm, "end": v(-11.33, 2.94) * mm});
            skLineSegment(sketch, "E287.0", {"start": v(-10.89, 1.88) * mm, "end": v(-10.89, -1.88) * mm});
            skArc(sketch, "E288.0", {"start": v(-11.33, -2.94) * mm, "mid": v(-11, -2.45) * mm, "end": v(-10.89, -1.88) * mm});
            skLineSegment(sketch, "E289.0", {"start": v(-11.33, -2.94) * mm, "end": v(-13.6, -5.22) * mm});
            skArc(sketch, "E290.0", {"start": v(-15.49, -4.44) * mm, "mid": v(-14.8, -5.46) * mm, "end": v(-13.6, -5.22) * mm});
            skLineSegment(sketch, "E291.0", {"start": v(-15.49, -2.75) * mm, "end": v(-15.49, -4.44) * mm});
            skArc(sketch, "E292.0", {"start": v(-15.49, -2.75) * mm, "mid": v(-15.56, -2.57) * mm, "end": v(-15.74, -2.5) * mm});
            skLineSegment(sketch, "E293.0", {"start": v(-15.74, -2.5) * mm, "end": v(-16.79, -2.5) * mm});
            skArc(sketch, "E294.0", {"start": v(-16.79, -2.5) * mm, "mid": v(-17.14, -2.64) * mm, "end": v(-17.29, -3) * mm});
            skLineSegment(sketch, "E295.0", {"start": v(-17.29, -3) * mm, "end": v(-17.29, -8.5) * mm});
            skArc(sketch, "E296.0", {"start": v(-17.29, -8.5) * mm, "mid": v(-16.85, -9.56) * mm, "end": v(-15.79, -10) * mm});
            skLineSegment(sketch, "E297.0", {"start": v(-15.79, -10) * mm, "end": v(-10.29, -10) * mm});
            skArc(sketch, "E298.0", {"start": v(-10.29, -10) * mm, "mid": v(-9.93, -9.85) * mm, "end": v(-9.79, -9.5) * mm});
            skLineSegment(sketch, "E299.0", {"start": v(-9.79, -9.5) * mm, "end": v(-9.79, -8.45) * mm});
            skArc(sketch, "E300.0", {"start": v(-9.79, -8.45) * mm, "mid": v(-9.86, -8.27) * mm, "end": v(-10.04, -8.2) * mm});
            skLineSegment(sketch, "E301.0", {"start": v(-11.73, -8.2) * mm, "end": v(-10.04, -8.2) * mm});
            skArc(sketch, "E302.0", {"start": v(-12.5, -6.32) * mm, "mid": v(-12.75, -7.52) * mm, "end": v(-11.73, -8.2) * mm});
            skLineSegment(sketch, "E303.0", {"start": v(-10.23, -4.04) * mm, "end": v(-12.5, -6.32) * mm});
            skArc(sketch, "E304.0", {"start": v(-9.16, -3.6) * mm, "mid": v(-9.74, -3.71) * mm, "end": v(-10.23, -4.04) * mm});
            skLineSegment(sketch, "E305.0", {"start": v(-9.16, -3.6) * mm, "end": v(-5.4, -3.6) * mm});
            skArc(sketch, "E306.0", {"start": v(-4.35, -4.04) * mm, "mid": v(-4.83, -3.71) * mm, "end": v(-5.4, -3.6) * mm});
            skCircle(sketch, "E307.0", {"center": v(-7.29, 0) * mm, "radius": 2.15 * mm});
            skLineSegment(sketch, "E308.0", {"start": v(-4.35, -4.04) * mm, "end": v(-2.06, -6.32) * mm});
            skArc(sketch, "E309.0", {"start": v(-2.84, -8.2) * mm, "mid": v(-1.83, -7.52) * mm, "end": v(-2.06, -6.32) * mm});
            skLineSegment(sketch, "E310.0", {"start": v(-4.54, -8.2) * mm, "end": v(-2.84, -8.2) * mm});
            skArc(sketch, "E311.0", {"start": v(-4.54, -8.2) * mm, "mid": v(-4.71, -8.27) * mm, "end": v(-4.79, -8.45) * mm});
            skLineSegment(sketch, "E312.0", {"start": v(-4.79, -9.5) * mm, "end": v(-4.79, -8.45) * mm});
            skArc(sketch, "E313.0", {"start": v(-4.79, -9.5) * mm, "mid": v(-4.64, -9.85) * mm, "end": v(-4.29, -10) * mm});
            skArc(sketch, "E314.0", {"start": v(-3.25, 2.94) * mm, "mid": v(-3.57, 2.45) * mm, "end": v(-3.69, 1.88) * mm});
            skLineSegment(sketch, "E315.0", {"start": v(-3.69, 1.88) * mm, "end": v(-3.69, -1.88) * mm});
            skArc(sketch, "E316.0", {"start": v(-3.69, -1.88) * mm, "mid": v(-3.57, -2.45) * mm, "end": v(-3.25, -2.94) * mm});
            skArc(sketch, "E317.0", {"start": v(2.64, 8.2) * mm, "mid": v(2.06, 8.09) * mm, "end": v(1.57, 7.76) * mm});
            skArc(sketch, "E318.0", {"start": v(3.85, 7.76) * mm, "mid": v(3.37, 8.09) * mm, "end": v(2.8, 8.2) * mm});
            skArc(sketch, "E319.0", {"start": v(8.67, 2.94) * mm, "mid": v(9, 2.45) * mm, "end": v(9.11, 1.88) * mm});
            skLineSegment(sketch, "E320.0", {"start": v(9.11, 1.88) * mm, "end": v(9.11, -1.88) * mm});
            skArc(sketch, "E321.0", {"start": v(9.11, -1.88) * mm, "mid": v(9, -2.45) * mm, "end": v(8.67, -2.94) * mm});
            skArc(sketch, "E322.0", {"start": v(1.57, -7.76) * mm, "mid": v(2.06, -8.08) * mm, "end": v(2.64, -8.2) * mm});
            skArc(sketch, "E323.0", {"start": v(2.8, -8.2) * mm, "mid": v(3.37, -8.08) * mm, "end": v(3.85, -7.76) * mm});
            skLineSegment(sketch, "E324.0", {"start": v(2.8, -8.2) * mm, "end": v(2.64, -8.2) * mm});
            skLineSegment(sketch, "E325.0", {"start": v(2.8, 8.2) * mm, "end": v(2.64, 8.2) * mm});
            skArc(sketch, "E326.0", {"start": v(9.71, 10) * mm, "mid": v(10.07, 9.86) * mm, "end": v(10.21, 9.5) * mm});
            skLineSegment(sketch, "E327.0", {"start": v(10.21, 9.5) * mm, "end": v(10.21, 8.45) * mm});
            skArc(sketch, "E328.0", {"start": v(10.21, 8.45) * mm, "mid": v(10.14, 8.28) * mm, "end": v(9.96, 8.2) * mm});
            skLineSegment(sketch, "E329.0", {"start": v(8.27, 8.2) * mm, "end": v(9.96, 8.2) * mm});
            skArc(sketch, "E330.0", {"start": v(7.5, 6.32) * mm, "mid": v(7.25, 7.52) * mm, "end": v(8.27, 8.2) * mm});
            skLineSegment(sketch, "E331.0", {"start": v(9.77, 4.04) * mm, "end": v(7.5, 6.32) * mm});
            skArc(sketch, "E332.0", {"start": v(10.84, 3.6) * mm, "mid": v(10.26, 3.72) * mm, "end": v(9.77, 4.04) * mm});
            skLineSegment(sketch, "E333.0", {"start": v(14.6, 3.6) * mm, "end": v(10.84, 3.6) * mm});
            skArc(sketch, "E334.0", {"start": v(15.65, 4.04) * mm, "mid": v(15.17, 3.72) * mm, "end": v(14.6, 3.6) * mm});
            skLineSegment(sketch, "E335.0", {"start": v(15.65, 4.04) * mm, "end": v(17.94, 6.32) * mm});
            skArc(sketch, "E336.0", {"start": v(17.16, 8.2) * mm, "mid": v(18.17, 7.52) * mm, "end": v(17.94, 6.32) * mm});
            skLineSegment(sketch, "E337.0", {"start": v(15.46, 8.2) * mm, "end": v(17.16, 8.2) * mm});
            skArc(sketch, "E338.0", {"start": v(15.46, 8.2) * mm, "mid": v(15.29, 8.28) * mm, "end": v(15.21, 8.45) * mm});
            skLineSegment(sketch, "E339.0", {"start": v(15.21, 9.5) * mm, "end": v(15.21, 8.45) * mm});
            skArc(sketch, "E340.0", {"start": v(15.21, 9.5) * mm, "mid": v(15.36, 9.86) * mm, "end": v(15.71, 10) * mm});
            skLineSegment(sketch, "E341.0", {"start": v(21.21, 10) * mm, "end": v(15.71, 10) * mm});
            skArc(sketch, "E342.0", {"start": v(21.21, 10) * mm, "mid": v(22.27, 9.56) * mm, "end": v(22.71, 8.5) * mm});
            skLineSegment(sketch, "E343.0", {"start": v(22.71, 8.5) * mm, "end": v(22.71, 3) * mm});
            skArc(sketch, "E344.0", {"start": v(22.71, 3) * mm, "mid": v(22.57, 2.65) * mm, "end": v(22.21, 2.5) * mm});
            skLineSegment(sketch, "E345.0", {"start": v(21.16, 2.5) * mm, "end": v(22.21, 2.5) * mm});
            skArc(sketch, "E346.0", {"start": v(21.16, 2.5) * mm, "mid": v(20.99, 2.58) * mm, "end": v(20.91, 2.75) * mm});
            skLineSegment(sketch, "E347.0", {"start": v(20.91, 4.45) * mm, "end": v(20.91, 2.75) * mm});
            skArc(sketch, "E348.0", {"start": v(19.04, 5.22) * mm, "mid": v(20.23, 5.46) * mm, "end": v(20.91, 4.45) * mm});
            skLineSegment(sketch, "E349.0", {"start": v(16.75, 2.94) * mm, "end": v(19.04, 5.22) * mm});
            skArc(sketch, "E350.0", {"start": v(16.31, 1.88) * mm, "mid": v(16.43, 2.45) * mm, "end": v(16.75, 2.94) * mm});
            skLineSegment(sketch, "E351.0", {"start": v(16.31, 1.88) * mm, "end": v(16.31, -1.88) * mm});
            skCircle(sketch, "E352.0", {"center": v(12.71, 0) * mm, "radius": 2.15 * mm});
            skArc(sketch, "E353.0", {"start": v(16.75, -2.94) * mm, "mid": v(16.43, -2.45) * mm, "end": v(16.31, -1.88) * mm});
            skLineSegment(sketch, "E354.0", {"start": v(16.75, -2.94) * mm, "end": v(19.04, -5.22) * mm});
            skArc(sketch, "E355.0", {"start": v(20.91, -4.44) * mm, "mid": v(20.23, -5.46) * mm, "end": v(19.04, -5.22) * mm});
            skLineSegment(sketch, "E356.0", {"start": v(20.91, -2.75) * mm, "end": v(20.91, -4.44) * mm});
            skArc(sketch, "E357.0", {"start": v(20.91, -2.75) * mm, "mid": v(20.99, -2.57) * mm, "end": v(21.16, -2.5) * mm});
            skLineSegment(sketch, "E358.0", {"start": v(21.16, -2.5) * mm, "end": v(22.21, -2.5) * mm});
            skArc(sketch, "E359.0", {"start": v(22.21, -2.5) * mm, "mid": v(22.57, -2.64) * mm, "end": v(22.71, -3) * mm});
            skLineSegment(sketch, "E360.0", {"start": v(22.71, -3) * mm, "end": v(22.71, -8.5) * mm});
            skArc(sketch, "E361.0", {"start": v(22.71, -8.5) * mm, "mid": v(22.27, -9.56) * mm, "end": v(21.21, -10) * mm});
            skLineSegment(sketch, "E362.0", {"start": v(21.21, -10) * mm, "end": v(15.71, -10) * mm});
            skArc(sketch, "E363.0", {"start": v(15.71, -10) * mm, "mid": v(15.36, -9.85) * mm, "end": v(15.21, -9.5) * mm});
            skLineSegment(sketch, "E364.0", {"start": v(15.21, -9.5) * mm, "end": v(15.21, -8.45) * mm});
            skArc(sketch, "E365.0", {"start": v(15.21, -8.45) * mm, "mid": v(15.29, -8.27) * mm, "end": v(15.46, -8.2) * mm});
            skLineSegment(sketch, "E366.0", {"start": v(17.16, -8.2) * mm, "end": v(15.46, -8.2) * mm});
            skArc(sketch, "E367.0", {"start": v(17.94, -6.32) * mm, "mid": v(18.17, -7.52) * mm, "end": v(17.16, -8.2) * mm});
            skLineSegment(sketch, "E368.0", {"start": v(15.65, -4.04) * mm, "end": v(17.94, -6.32) * mm});
            skArc(sketch, "E369.0", {"start": v(14.6, -3.6) * mm, "mid": v(15.17, -3.71) * mm, "end": v(15.65, -4.04) * mm});
            skLineSegment(sketch, "E370.0", {"start": v(14.6, -3.6) * mm, "end": v(10.84, -3.6) * mm});
            skArc(sketch, "E371.0", {"start": v(9.77, -4.04) * mm, "mid": v(10.26, -3.71) * mm, "end": v(10.84, -3.6) * mm});
            skLineSegment(sketch, "E372.0", {"start": v(9.77, -4.04) * mm, "end": v(7.5, -6.32) * mm});
            skArc(sketch, "E373.0", {"start": v(8.27, -8.2) * mm, "mid": v(7.25, -7.52) * mm, "end": v(7.5, -6.32) * mm});
            skLineSegment(sketch, "E374.0", {"start": v(9.96, -8.2) * mm, "end": v(8.27, -8.2) * mm});
            skArc(sketch, "E375.0", {"start": v(9.96, -8.2) * mm, "mid": v(10.14, -8.27) * mm, "end": v(10.21, -8.45) * mm});
            skLineSegment(sketch, "E376.0", {"start": v(10.21, -9.5) * mm, "end": v(10.21, -8.45) * mm});
            skArc(sketch, "E377.0", {"start": v(10.21, -9.5) * mm, "mid": v(10.07, -9.85) * mm, "end": v(9.71, -10) * mm});
            skLineSegment(sketch, "E378", {"start": v(-4.29, 10) * mm, "end": v(9.71, 10) * mm});
            skLineSegment(sketch, "E379", {"start": v(-3.25, 2.94) * mm, "end": v(1.57, 7.76) * mm});
            skLineSegment(sketch, "E380", {"start": v(3.85, 7.76) * mm, "end": v(8.67, 2.94) * mm});
            skLineSegment(sketch, "E381", {"start": v(8.67, -2.94) * mm, "end": v(3.85, -7.76) * mm});
            skLineSegment(sketch, "E382", {"start": v(1.57, -7.76) * mm, "end": v(-3.25, -2.94) * mm});
            skLineSegment(sketch, "E383", {"start": v(-4.29, -10) * mm, "end": v(9.71, -10) * mm});
            skSolve(sketch);
        }
        {
            var Q0;
            Q0=qCreatedBy(makeId("Front.planeOp"),FACE);
            var sketch = newSketch(context, id + "F4", { "sketchPlane" : qUnion([Q0])});
            skLineSegment(sketch, "E384.0.0", {"start": v(-10.29, 10) * mm, "end": v(-15.79, 10) * mm});
            skArc(sketch, "E384.0.1", {"start": v(-15.79, 10) * mm, "mid": v(-16.85, 9.56) * mm, "end": v(-17.29, 8.5) * mm});
            skLineSegment(sketch, "E384.0.2", {"start": v(-17.29, 8.5) * mm, "end": v(-17.29, 3) * mm});
            skArc(sketch, "E384.0.3", {"start": v(-17.29, 3) * mm, "mid": v(-17.14, 2.65) * mm, "end": v(-16.79, 2.5) * mm});
            skLineSegment(sketch, "E384.0.4", {"start": v(-16.79, 2.5) * mm, "end": v(-15.74, 2.5) * mm});
            skArc(sketch, "E384.0.5", {"start": v(-15.74, 2.5) * mm, "mid": v(-15.56, 2.58) * mm, "end": v(-15.49, 2.75) * mm});
            skLineSegment(sketch, "E384.0.6", {"start": v(-15.49, 2.75) * mm, "end": v(-15.49, 4.45) * mm});
            skArc(sketch, "E384.0.7", {"start": v(-15.49, 4.45) * mm, "mid": v(-14.8, 5.46) * mm, "end": v(-13.6, 5.22) * mm});
            skLineSegment(sketch, "E384.0.8", {"start": v(-13.6, 5.22) * mm, "end": v(-11.33, 2.94) * mm});
            skArc(sketch, "E384.0.9", {"start": v(-11.33, 2.94) * mm, "mid": v(-11, 2.45) * mm, "end": v(-10.89, 1.88) * mm});
            skLineSegment(sketch, "E384.0.10", {"start": v(-10.89, 1.88) * mm, "end": v(-10.89, -1.88) * mm});
            skArc(sketch, "E384.0.11", {"start": v(-10.89, -1.88) * mm, "mid": v(-11, -2.45) * mm, "end": v(-11.33, -2.94) * mm});
            skLineSegment(sketch, "E384.0.12", {"start": v(-11.33, -2.94) * mm, "end": v(-13.6, -5.22) * mm});
            skArc(sketch, "E384.0.13", {"start": v(-13.6, -5.22) * mm, "mid": v(-14.8, -5.46) * mm, "end": v(-15.49, -4.44) * mm});
            skLineSegment(sketch, "E384.0.14", {"start": v(-15.49, -4.44) * mm, "end": v(-15.49, -2.75) * mm});
            skArc(sketch, "E384.0.15", {"start": v(-15.49, -2.75) * mm, "mid": v(-15.56, -2.57) * mm, "end": v(-15.74, -2.5) * mm});
            skLineSegment(sketch, "E384.0.16", {"start": v(-15.74, -2.5) * mm, "end": v(-16.79, -2.5) * mm});
            skArc(sketch, "E384.0.17", {"start": v(-16.79, -2.5) * mm, "mid": v(-17.14, -2.64) * mm, "end": v(-17.29, -3) * mm});
            skLineSegment(sketch, "E384.0.18", {"start": v(-17.29, -3) * mm, "end": v(-17.29, -8.5) * mm});
            skArc(sketch, "E384.0.19", {"start": v(-17.29, -8.5) * mm, "mid": v(-16.85, -9.56) * mm, "end": v(-15.79, -10) * mm});
            skLineSegment(sketch, "E384.0.20", {"start": v(-15.79, -10) * mm, "end": v(-10.29, -10) * mm});
            skArc(sketch, "E384.0.21", {"start": v(-10.29, -10) * mm, "mid": v(-9.93, -9.85) * mm, "end": v(-9.79, -9.5) * mm});
            skLineSegment(sketch, "E384.0.22", {"start": v(-9.79, -9.5) * mm, "end": v(-9.79, -8.45) * mm});
            skArc(sketch, "E384.0.23", {"start": v(-9.79, -8.45) * mm, "mid": v(-9.86, -8.27) * mm, "end": v(-10.04, -8.2) * mm});
            skLineSegment(sketch, "E384.0.24", {"start": v(-10.04, -8.2) * mm, "end": v(-11.73, -8.2) * mm});
            skArc(sketch, "E384.0.25", {"start": v(-11.73, -8.2) * mm, "mid": v(-12.75, -7.52) * mm, "end": v(-12.5, -6.32) * mm});
            skLineSegment(sketch, "E384.0.26", {"start": v(-12.5, -6.32) * mm, "end": v(-10.23, -4.04) * mm});
            skArc(sketch, "E384.0.27", {"start": v(-10.23, -4.04) * mm, "mid": v(-9.74, -3.71) * mm, "end": v(-9.16, -3.6) * mm});
            skLineSegment(sketch, "E384.0.28", {"start": v(-9.16, -3.6) * mm, "end": v(-5.4, -3.6) * mm});
            skArc(sketch, "E384.0.29", {"start": v(-5.4, -3.6) * mm, "mid": v(-4.83, -3.71) * mm, "end": v(-4.35, -4.04) * mm});
            skLineSegment(sketch, "E384.0.30", {"start": v(-4.35, -4.04) * mm, "end": v(-2.06, -6.32) * mm});
            skArc(sketch, "E384.0.31", {"start": v(-2.06, -6.32) * mm, "mid": v(-1.83, -7.52) * mm, "end": v(-2.84, -8.2) * mm});
            skLineSegment(sketch, "E384.0.32", {"start": v(-2.84, -8.2) * mm, "end": v(-4.54, -8.2) * mm});
            skArc(sketch, "E384.0.33", {"start": v(-4.54, -8.2) * mm, "mid": v(-4.71, -8.27) * mm, "end": v(-4.79, -8.45) * mm});
            skLineSegment(sketch, "E384.0.34", {"start": v(-4.79, -8.45) * mm, "end": v(-4.79, -9.5) * mm});
            skArc(sketch, "E384.0.35", {"start": v(-4.79, -9.5) * mm, "mid": v(-4.64, -9.85) * mm, "end": v(-4.29, -10) * mm});
            skLineSegment(sketch, "E384.0.36", {"start": v(-4.29, -10) * mm, "end": v(9.71, -10) * mm});
            skArc(sketch, "E384.0.37", {"start": v(9.71, -10) * mm, "mid": v(10.07, -9.85) * mm, "end": v(10.21, -9.5) * mm});
            skLineSegment(sketch, "E384.0.38", {"start": v(10.21, -9.5) * mm, "end": v(10.21, -8.45) * mm});
            skArc(sketch, "E384.0.39", {"start": v(10.21, -8.45) * mm, "mid": v(10.14, -8.27) * mm, "end": v(9.96, -8.2) * mm});
            skLineSegment(sketch, "E384.0.40", {"start": v(9.96, -8.2) * mm, "end": v(8.27, -8.2) * mm});
            skArc(sketch, "E384.0.41", {"start": v(8.27, -8.2) * mm, "mid": v(7.25, -7.52) * mm, "end": v(7.5, -6.32) * mm});
            skLineSegment(sketch, "E384.0.42", {"start": v(7.5, -6.32) * mm, "end": v(9.77, -4.04) * mm});
            skArc(sketch, "E384.0.43", {"start": v(9.77, -4.04) * mm, "mid": v(10.26, -3.71) * mm, "end": v(10.84, -3.6) * mm});
            skLineSegment(sketch, "E384.0.44", {"start": v(10.84, -3.6) * mm, "end": v(14.6, -3.6) * mm});
            skArc(sketch, "E384.0.45", {"start": v(14.6, -3.6) * mm, "mid": v(15.17, -3.71) * mm, "end": v(15.65, -4.04) * mm});
            skLineSegment(sketch, "E384.0.46", {"start": v(15.65, -4.04) * mm, "end": v(17.94, -6.32) * mm});
            skArc(sketch, "E384.0.47", {"start": v(17.94, -6.32) * mm, "mid": v(18.17, -7.52) * mm, "end": v(17.16, -8.2) * mm});
            skLineSegment(sketch, "E384.0.48", {"start": v(17.16, -8.2) * mm, "end": v(15.46, -8.2) * mm});
            skArc(sketch, "E384.0.49", {"start": v(15.46, -8.2) * mm, "mid": v(15.29, -8.27) * mm, "end": v(15.21, -8.45) * mm});
            skLineSegment(sketch, "E384.0.50", {"start": v(15.21, -8.45) * mm, "end": v(15.21, -9.5) * mm});
            skArc(sketch, "E384.0.51", {"start": v(15.21, -9.5) * mm, "mid": v(15.36, -9.85) * mm, "end": v(15.71, -10) * mm});
            skArc(sketch, "E384.0.61", {"start": v(16.75, -2.94) * mm, "mid": v(16.43, -2.45) * mm, "end": v(16.31, -1.88) * mm});
            skLineSegment(sketch, "E384.0.62", {"start": v(16.31, -1.88) * mm, "end": v(16.31, 1.88) * mm});
            skArc(sketch, "E384.0.63", {"start": v(16.31, 1.88) * mm, "mid": v(16.43, 2.45) * mm, "end": v(16.75, 2.94) * mm});
            skArc(sketch, "E384.0.73", {"start": v(15.71, 10) * mm, "mid": v(15.36, 9.86) * mm, "end": v(15.21, 9.5) * mm});
            skLineSegment(sketch, "E384.0.74", {"start": v(15.21, 9.5) * mm, "end": v(15.21, 8.45) * mm});
            skArc(sketch, "E384.0.75", {"start": v(15.21, 8.45) * mm, "mid": v(15.29, 8.28) * mm, "end": v(15.46, 8.2) * mm});
            skLineSegment(sketch, "E384.0.76", {"start": v(15.46, 8.2) * mm, "end": v(17.16, 8.2) * mm});
            skArc(sketch, "E384.0.77", {"start": v(17.16, 8.2) * mm, "mid": v(18.17, 7.52) * mm, "end": v(17.94, 6.32) * mm});
            skLineSegment(sketch, "E384.0.78", {"start": v(17.94, 6.32) * mm, "end": v(15.65, 4.04) * mm});
            skArc(sketch, "E384.0.79", {"start": v(15.65, 4.04) * mm, "mid": v(15.17, 3.72) * mm, "end": v(14.6, 3.6) * mm});
            skLineSegment(sketch, "E384.0.80", {"start": v(14.6, 3.6) * mm, "end": v(10.84, 3.6) * mm});
            skArc(sketch, "E384.0.81", {"start": v(10.84, 3.6) * mm, "mid": v(10.26, 3.72) * mm, "end": v(9.77, 4.04) * mm});
            skLineSegment(sketch, "E384.0.82", {"start": v(9.77, 4.04) * mm, "end": v(7.5, 6.32) * mm});
            skArc(sketch, "E384.0.83", {"start": v(7.5, 6.32) * mm, "mid": v(7.25, 7.52) * mm, "end": v(8.27, 8.2) * mm});
            skLineSegment(sketch, "E384.0.84", {"start": v(8.27, 8.2) * mm, "end": v(9.96, 8.2) * mm});
            skArc(sketch, "E384.0.85", {"start": v(9.96, 8.2) * mm, "mid": v(10.14, 8.28) * mm, "end": v(10.21, 8.45) * mm});
            skLineSegment(sketch, "E384.0.86", {"start": v(10.21, 8.45) * mm, "end": v(10.21, 9.5) * mm});
            skArc(sketch, "E384.0.87", {"start": v(10.21, 9.5) * mm, "mid": v(10.07, 9.86) * mm, "end": v(9.71, 10) * mm});
            skLineSegment(sketch, "E384.0.88", {"start": v(9.71, 10) * mm, "end": v(-4.29, 10) * mm});
            skArc(sketch, "E384.0.89", {"start": v(-4.29, 10) * mm, "mid": v(-4.64, 9.86) * mm, "end": v(-4.79, 9.5) * mm});
            skLineSegment(sketch, "E384.0.90", {"start": v(-4.79, 9.5) * mm, "end": v(-4.79, 8.45) * mm});
            skArc(sketch, "E384.0.91", {"start": v(-4.79, 8.45) * mm, "mid": v(-4.71, 8.28) * mm, "end": v(-4.54, 8.2) * mm});
            skLineSegment(sketch, "E384.0.92", {"start": v(-4.54, 8.2) * mm, "end": v(-2.84, 8.2) * mm});
            skArc(sketch, "E384.0.93", {"start": v(-2.84, 8.2) * mm, "mid": v(-1.83, 7.52) * mm, "end": v(-2.06, 6.32) * mm});
            skLineSegment(sketch, "E384.0.94", {"start": v(-2.06, 6.32) * mm, "end": v(-4.35, 4.04) * mm});
            skArc(sketch, "E384.0.95", {"start": v(-4.35, 4.04) * mm, "mid": v(-4.83, 3.72) * mm, "end": v(-5.4, 3.6) * mm});
            skLineSegment(sketch, "E384.0.96", {"start": v(-5.4, 3.6) * mm, "end": v(-9.16, 3.6) * mm});
            skArc(sketch, "E384.0.97", {"start": v(-9.16, 3.6) * mm, "mid": v(-9.74, 3.72) * mm, "end": v(-10.23, 4.04) * mm});
            skLineSegment(sketch, "E384.0.98", {"start": v(-10.23, 4.04) * mm, "end": v(-12.5, 6.32) * mm});
            skArc(sketch, "E384.0.99", {"start": v(-12.5, 6.32) * mm, "mid": v(-12.75, 7.52) * mm, "end": v(-11.73, 8.2) * mm});
            skLineSegment(sketch, "E384.0.100", {"start": v(-11.73, 8.2) * mm, "end": v(-10.04, 8.2) * mm});
            skArc(sketch, "E384.0.101", {"start": v(-10.04, 8.2) * mm, "mid": v(-9.86, 8.28) * mm, "end": v(-9.79, 8.45) * mm});
            skLineSegment(sketch, "E384.0.102", {"start": v(-9.79, 8.45) * mm, "end": v(-9.79, 9.5) * mm});
            skArc(sketch, "E384.0.103", {"start": v(-9.79, 9.5) * mm, "mid": v(-9.93, 9.86) * mm, "end": v(-10.29, 10) * mm});
            skLineSegment(sketch, "E385.0.0", {"start": v(1.57, 7.76) * mm, "end": v(-3.25, 2.94) * mm});
            skArc(sketch, "E385.0.1", {"start": v(-3.25, 2.94) * mm, "mid": v(-3.57, 2.45) * mm, "end": v(-3.69, 1.88) * mm});
            skLineSegment(sketch, "E385.0.2", {"start": v(-3.69, 1.88) * mm, "end": v(-3.69, -1.88) * mm});
            skArc(sketch, "E385.0.3", {"start": v(-3.69, -1.88) * mm, "mid": v(-3.57, -2.45) * mm, "end": v(-3.25, -2.94) * mm});
            skLineSegment(sketch, "E385.0.4", {"start": v(-3.25, -2.94) * mm, "end": v(1.57, -7.76) * mm});
            skArc(sketch, "E385.0.5", {"start": v(1.57, -7.76) * mm, "mid": v(2.06, -8.08) * mm, "end": v(2.64, -8.2) * mm});
            skLineSegment(sketch, "E385.0.6", {"start": v(2.64, -8.2) * mm, "end": v(2.8, -8.2) * mm});
            skArc(sketch, "E385.0.7", {"start": v(2.8, -8.2) * mm, "mid": v(3.37, -8.08) * mm, "end": v(3.85, -7.76) * mm});
            skLineSegment(sketch, "E385.0.8", {"start": v(3.85, -7.76) * mm, "end": v(8.67, -2.94) * mm});
            skArc(sketch, "E385.0.9", {"start": v(8.67, -2.94) * mm, "mid": v(9, -2.45) * mm, "end": v(9.11, -1.88) * mm});
            skLineSegment(sketch, "E385.0.10", {"start": v(9.11, -1.88) * mm, "end": v(9.11, 1.88) * mm});
            skArc(sketch, "E385.0.11", {"start": v(9.11, 1.88) * mm, "mid": v(9, 2.45) * mm, "end": v(8.67, 2.94) * mm});
            skLineSegment(sketch, "E385.0.12", {"start": v(8.67, 2.94) * mm, "end": v(3.85, 7.76) * mm});
            skArc(sketch, "E385.0.13", {"start": v(3.85, 7.76) * mm, "mid": v(3.37, 8.09) * mm, "end": v(2.8, 8.2) * mm});
            skLineSegment(sketch, "E385.0.14", {"start": v(2.8, 8.2) * mm, "end": v(2.64, 8.2) * mm});
            skArc(sketch, "E385.0.15", {"start": v(2.64, 8.2) * mm, "mid": v(2.06, 8.09) * mm, "end": v(1.57, 7.76) * mm});
            skCircle(sketch, "E386.0", {"center": v(-7.29, 0) * mm, "radius": 2.15 * mm});
            skCircle(sketch, "E387.0", {"center": v(12.71, 0) * mm, "radius": 2.15 * mm});
            skLineSegment(sketch, "E388", {"start": v(12.71, 11.72) * mm, "end": v(12.71, -12.08) * mm, "construction": true});
            skLineSegment(sketch, "E389.0.MirrorCS", {"start": v(16.75, 2.94) * mm, "end": v(21.57, 7.76) * mm});
            skLineSegment(sketch, "E390.0.MirrorCS", {"start": v(21.57, -7.76) * mm, "end": v(16.75, -2.94) * mm});
            skArc(sketch, "E391.0.MirrorCS", {"start": v(22.64, -8.2) * mm, "mid": v(22.06, -8.08) * mm, "end": v(21.57, -7.76) * mm});
            skArc(sketch, "E392.0.MirrorCS", {"start": v(21.57, 7.76) * mm, "mid": v(22.06, 8.09) * mm, "end": v(22.64, 8.2) * mm});
            skLineSegment(sketch, "E393.0.MirrorCS", {"start": v(22.64, 8.2) * mm, "end": v(22.8, 8.2) * mm});
            skArc(sketch, "E394.0.MirrorCS", {"start": v(22.8, 8.2) * mm, "mid": v(23.37, 8.09) * mm, "end": v(23.85, 7.76) * mm});
            skLineSegment(sketch, "E395.0.MirrorCS", {"start": v(23.85, 7.76) * mm, "end": v(28.67, 2.94) * mm});
            skArc(sketch, "E396.0.MirrorCS", {"start": v(28.67, 2.94) * mm, "mid": v(29, 2.45) * mm, "end": v(29.11, 1.88) * mm});
            skLineSegment(sketch, "E397.0.MirrorCS", {"start": v(29.11, 1.88) * mm, "end": v(29.11, -1.88) * mm});
            skArc(sketch, "E398.0.MirrorCS", {"start": v(29.11, -1.88) * mm, "mid": v(29, -2.45) * mm, "end": v(28.67, -2.94) * mm});
            skLineSegment(sketch, "E399.0.MirrorCS", {"start": v(28.67, -2.94) * mm, "end": v(23.85, -7.76) * mm});
            skArc(sketch, "E400.0.MirrorCS", {"start": v(23.85, -7.76) * mm, "mid": v(23.37, -8.08) * mm, "end": v(22.8, -8.2) * mm});
            skLineSegment(sketch, "E401.0.MirrorCS", {"start": v(22.8, -8.2) * mm, "end": v(22.64, -8.2) * mm});
            skLineSegment(sketch, "E402.0.MirrorCS", {"start": v(29.71, -10) * mm, "end": v(15.71, -10) * mm});
            skLineSegment(sketch, "E403.0.MirrorCS", {"start": v(15.71, 10) * mm, "end": v(29.71, 10) * mm});
            skArc(sketch, "E404.0.MirrorCS", {"start": v(29.71, 10) * mm, "mid": v(30.07, 9.86) * mm, "end": v(30.21, 9.5) * mm});
            skLineSegment(sketch, "E405.0.MirrorCS", {"start": v(30.21, 9.5) * mm, "end": v(30.21, 8.45) * mm});
            skArc(sketch, "E406.0.MirrorCS", {"start": v(30.21, 8.45) * mm, "mid": v(30.14, 8.28) * mm, "end": v(29.96, 8.2) * mm});
            skLineSegment(sketch, "E407.0.MirrorCS", {"start": v(29.96, 8.2) * mm, "end": v(28.27, 8.2) * mm});
            skArc(sketch, "E408.0.MirrorCS", {"start": v(28.27, 8.2) * mm, "mid": v(27.25, 7.52) * mm, "end": v(27.5, 6.32) * mm});
            skLineSegment(sketch, "E409.0.MirrorCS", {"start": v(27.5, 6.32) * mm, "end": v(29.77, 4.04) * mm});
            skArc(sketch, "E410.0.MirrorCS", {"start": v(29.77, 4.04) * mm, "mid": v(30.26, 3.72) * mm, "end": v(30.84, 3.6) * mm});
            skLineSegment(sketch, "E411.0.MirrorCS", {"start": v(30.84, 3.6) * mm, "end": v(34.6, 3.6) * mm});
            skArc(sketch, "E412.0.MirrorCS", {"start": v(34.6, 3.6) * mm, "mid": v(35.17, 3.72) * mm, "end": v(35.65, 4.04) * mm});
            skLineSegment(sketch, "E413.0.MirrorCS", {"start": v(35.65, 4.04) * mm, "end": v(37.94, 6.32) * mm});
            skArc(sketch, "E414.0.MirrorCS", {"start": v(37.94, 6.32) * mm, "mid": v(38.17, 7.52) * mm, "end": v(37.16, 8.2) * mm});
            skLineSegment(sketch, "E415.0.MirrorCS", {"start": v(37.16, 8.2) * mm, "end": v(35.46, 8.2) * mm});
            skArc(sketch, "E416.0.MirrorCS", {"start": v(35.46, 8.2) * mm, "mid": v(35.29, 8.28) * mm, "end": v(35.21, 8.45) * mm});
            skLineSegment(sketch, "E417.0.MirrorCS", {"start": v(35.21, 8.45) * mm, "end": v(35.21, 9.5) * mm});
            skArc(sketch, "E418.0.MirrorCS", {"start": v(35.21, 9.5) * mm, "mid": v(35.36, 9.86) * mm, "end": v(35.71, 10) * mm});
            skLineSegment(sketch, "E419.0.MirrorCS", {"start": v(35.71, 10) * mm, "end": v(41.21, 10) * mm});
            skArc(sketch, "E420.0.MirrorCS", {"start": v(41.21, 10) * mm, "mid": v(42.27, 9.56) * mm, "end": v(42.71, 8.5) * mm});
            skLineSegment(sketch, "E421.0.MirrorCS", {"start": v(42.71, 8.5) * mm, "end": v(42.71, 3) * mm});
            skArc(sketch, "E422.0.MirrorCS", {"start": v(42.71, 3) * mm, "mid": v(42.57, 2.65) * mm, "end": v(42.21, 2.5) * mm});
            skLineSegment(sketch, "E423.0.MirrorCS", {"start": v(42.21, 2.5) * mm, "end": v(41.16, 2.5) * mm});
            skArc(sketch, "E424.0.MirrorCS", {"start": v(41.16, 2.5) * mm, "mid": v(40.99, 2.58) * mm, "end": v(40.91, 2.75) * mm});
            skLineSegment(sketch, "E425.0.MirrorCS", {"start": v(40.91, 2.75) * mm, "end": v(40.91, 4.45) * mm});
            skArc(sketch, "E426.0.MirrorCS", {"start": v(40.91, 4.45) * mm, "mid": v(40.23, 5.46) * mm, "end": v(39.04, 5.22) * mm});
            skLineSegment(sketch, "E427.0.MirrorCS", {"start": v(39.04, 5.22) * mm, "end": v(36.75, 2.94) * mm});
            skArc(sketch, "E428.0.MirrorCS", {"start": v(36.75, 2.94) * mm, "mid": v(36.43, 2.45) * mm, "end": v(36.31, 1.88) * mm});
            skLineSegment(sketch, "E429.0.MirrorCS", {"start": v(36.31, 1.88) * mm, "end": v(36.31, -1.88) * mm});
            skArc(sketch, "E430.0.MirrorCS", {"start": v(36.31, -1.88) * mm, "mid": v(36.43, -2.45) * mm, "end": v(36.75, -2.94) * mm});
            skLineSegment(sketch, "E431.0.MirrorCS", {"start": v(36.75, -2.94) * mm, "end": v(39.04, -5.22) * mm});
            skArc(sketch, "E432.0.MirrorCS", {"start": v(39.04, -5.22) * mm, "mid": v(40.23, -5.46) * mm, "end": v(40.91, -4.44) * mm});
            skLineSegment(sketch, "E433.0.MirrorCS", {"start": v(40.91, -4.44) * mm, "end": v(40.91, -2.75) * mm});
            skArc(sketch, "E434.0.MirrorCS", {"start": v(40.91, -2.75) * mm, "mid": v(40.99, -2.57) * mm, "end": v(41.16, -2.5) * mm});
            skLineSegment(sketch, "E435.0.MirrorCS", {"start": v(41.16, -2.5) * mm, "end": v(42.21, -2.5) * mm});
            skArc(sketch, "E436.0.MirrorCS", {"start": v(42.21, -2.5) * mm, "mid": v(42.57, -2.64) * mm, "end": v(42.71, -3) * mm});
            skLineSegment(sketch, "E437.0.MirrorCS", {"start": v(42.71, -3) * mm, "end": v(42.71, -8.5) * mm});
            skArc(sketch, "E438.0.MirrorCS", {"start": v(42.71, -8.5) * mm, "mid": v(42.27, -9.56) * mm, "end": v(41.21, -10) * mm});
            skLineSegment(sketch, "E439.0.MirrorCS", {"start": v(41.21, -10) * mm, "end": v(35.71, -10) * mm});
            skArc(sketch, "E440.0.MirrorCS", {"start": v(35.71, -10) * mm, "mid": v(35.36, -9.85) * mm, "end": v(35.21, -9.5) * mm});
            skLineSegment(sketch, "E441.0.MirrorCS", {"start": v(35.21, -9.5) * mm, "end": v(35.21, -8.45) * mm});
            skArc(sketch, "E442.0.MirrorCS", {"start": v(35.21, -8.45) * mm, "mid": v(35.29, -8.27) * mm, "end": v(35.46, -8.2) * mm});
            skLineSegment(sketch, "E443.0.MirrorCS", {"start": v(35.46, -8.2) * mm, "end": v(37.16, -8.2) * mm});
            skArc(sketch, "E444.0.MirrorCS", {"start": v(37.16, -8.2) * mm, "mid": v(38.17, -7.52) * mm, "end": v(37.94, -6.32) * mm});
            skLineSegment(sketch, "E445.0.MirrorCS", {"start": v(37.94, -6.32) * mm, "end": v(35.65, -4.04) * mm});
            skArc(sketch, "E446.0.MirrorCS", {"start": v(35.65, -4.04) * mm, "mid": v(35.17, -3.71) * mm, "end": v(34.6, -3.6) * mm});
            skLineSegment(sketch, "E447.0.MirrorCS", {"start": v(34.6, -3.6) * mm, "end": v(30.84, -3.6) * mm});
            skArc(sketch, "E448.0.MirrorCS", {"start": v(30.84, -3.6) * mm, "mid": v(30.26, -3.71) * mm, "end": v(29.77, -4.04) * mm});
            skLineSegment(sketch, "E449.0.MirrorCS", {"start": v(29.77, -4.04) * mm, "end": v(27.5, -6.32) * mm});
            skArc(sketch, "E450.0.MirrorCS", {"start": v(27.5, -6.32) * mm, "mid": v(27.25, -7.52) * mm, "end": v(28.27, -8.2) * mm});
            skLineSegment(sketch, "E451.0.MirrorCS", {"start": v(28.27, -8.2) * mm, "end": v(29.96, -8.2) * mm});
            skArc(sketch, "E452.0.MirrorCS", {"start": v(29.96, -8.2) * mm, "mid": v(30.14, -8.27) * mm, "end": v(30.21, -8.45) * mm});
            skLineSegment(sketch, "E453.0.MirrorCS", {"start": v(30.21, -8.45) * mm, "end": v(30.21, -9.5) * mm});
            skArc(sketch, "E454.0.MirrorCS", {"start": v(30.21, -9.5) * mm, "mid": v(30.07, -9.85) * mm, "end": v(29.71, -10) * mm});
            skCircle(sketch, "E455.0.MirrorC", {"center": v(32.71, 0) * mm, "radius": 2.15 * mm});
            skSolve(sketch);
        }
        {
            var Q0;
            Q0=qCreatedBy(makeId("Front.planeOp"),FACE);
            var sketch = newSketch(context, id + "F5", { "sketchPlane" : qUnion([Q0])});
            skLineSegment(sketch, "E456.0.0", {"start": v(-10.29, 10) * mm, "end": v(-15.79, 10) * mm});
            skArc(sketch, "E456.0.1", {"start": v(-15.79, 10) * mm, "mid": v(-16.85, 9.56) * mm, "end": v(-17.29, 8.5) * mm});
            skLineSegment(sketch, "E456.0.2", {"start": v(-17.29, 8.5) * mm, "end": v(-17.29, 3) * mm});
            skArc(sketch, "E456.0.3", {"start": v(-17.29, 3) * mm, "mid": v(-17.14, 2.65) * mm, "end": v(-16.79, 2.5) * mm});
            skLineSegment(sketch, "E456.0.4", {"start": v(-16.79, 2.5) * mm, "end": v(-15.74, 2.5) * mm});
            skArc(sketch, "E456.0.5", {"start": v(-15.74, 2.5) * mm, "mid": v(-15.56, 2.58) * mm, "end": v(-15.49, 2.75) * mm});
            skLineSegment(sketch, "E456.0.6", {"start": v(-15.49, 2.75) * mm, "end": v(-15.49, 4.45) * mm});
            skArc(sketch, "E456.0.7", {"start": v(-15.49, 4.45) * mm, "mid": v(-14.8, 5.46) * mm, "end": v(-13.6, 5.22) * mm});
            skLineSegment(sketch, "E456.0.8", {"start": v(-13.6, 5.22) * mm, "end": v(-11.33, 2.94) * mm});
            skArc(sketch, "E456.0.9", {"start": v(-11.33, 2.94) * mm, "mid": v(-11, 2.45) * mm, "end": v(-10.89, 1.88) * mm});
            skLineSegment(sketch, "E456.0.10", {"start": v(-10.89, 1.88) * mm, "end": v(-10.89, -1.88) * mm});
            skArc(sketch, "E456.0.11", {"start": v(-10.89, -1.88) * mm, "mid": v(-11, -2.45) * mm, "end": v(-11.33, -2.94) * mm});
            skLineSegment(sketch, "E456.0.12", {"start": v(-11.33, -2.94) * mm, "end": v(-13.6, -5.22) * mm});
            skArc(sketch, "E456.0.13", {"start": v(-13.6, -5.22) * mm, "mid": v(-14.8, -5.46) * mm, "end": v(-15.49, -4.44) * mm});
            skLineSegment(sketch, "E456.0.14", {"start": v(-15.49, -4.44) * mm, "end": v(-15.49, -2.75) * mm});
            skArc(sketch, "E456.0.15", {"start": v(-15.49, -2.75) * mm, "mid": v(-15.56, -2.57) * mm, "end": v(-15.74, -2.5) * mm});
            skLineSegment(sketch, "E456.0.16", {"start": v(-15.74, -2.5) * mm, "end": v(-16.79, -2.5) * mm});
            skArc(sketch, "E456.0.17", {"start": v(-16.79, -2.5) * mm, "mid": v(-17.14, -2.64) * mm, "end": v(-17.29, -3) * mm});
            skLineSegment(sketch, "E456.0.18", {"start": v(-17.29, -3) * mm, "end": v(-17.29, -8.5) * mm});
            skArc(sketch, "E456.0.19", {"start": v(-17.29, -8.5) * mm, "mid": v(-16.85, -9.56) * mm, "end": v(-15.79, -10) * mm});
            skLineSegment(sketch, "E456.0.20", {"start": v(-15.79, -10) * mm, "end": v(-10.29, -10) * mm});
            skArc(sketch, "E456.0.21", {"start": v(-10.29, -10) * mm, "mid": v(-9.93, -9.85) * mm, "end": v(-9.79, -9.5) * mm});
            skLineSegment(sketch, "E456.0.22", {"start": v(-9.79, -9.5) * mm, "end": v(-9.79, -8.45) * mm});
            skArc(sketch, "E456.0.23", {"start": v(-9.79, -8.45) * mm, "mid": v(-9.86, -8.27) * mm, "end": v(-10.04, -8.2) * mm});
            skLineSegment(sketch, "E456.0.24", {"start": v(-10.04, -8.2) * mm, "end": v(-11.73, -8.2) * mm});
            skArc(sketch, "E456.0.25", {"start": v(-11.73, -8.2) * mm, "mid": v(-12.75, -7.52) * mm, "end": v(-12.5, -6.32) * mm});
            skLineSegment(sketch, "E456.0.26", {"start": v(-12.5, -6.32) * mm, "end": v(-10.23, -4.04) * mm});
            skArc(sketch, "E456.0.27", {"start": v(-10.23, -4.04) * mm, "mid": v(-9.74, -3.71) * mm, "end": v(-9.16, -3.6) * mm});
            skLineSegment(sketch, "E456.0.28", {"start": v(-9.16, -3.6) * mm, "end": v(-5.4, -3.6) * mm});
            skArc(sketch, "E456.0.29", {"start": v(-5.4, -3.6) * mm, "mid": v(-4.83, -3.71) * mm, "end": v(-4.35, -4.04) * mm});
            skLineSegment(sketch, "E456.0.30", {"start": v(-4.35, -4.04) * mm, "end": v(-2.06, -6.32) * mm});
            skArc(sketch, "E456.0.31", {"start": v(-2.06, -6.32) * mm, "mid": v(-1.83, -7.52) * mm, "end": v(-2.84, -8.2) * mm});
            skLineSegment(sketch, "E456.0.32", {"start": v(-2.84, -8.2) * mm, "end": v(-4.54, -8.2) * mm});
            skArc(sketch, "E456.0.33", {"start": v(-4.54, -8.2) * mm, "mid": v(-4.71, -8.27) * mm, "end": v(-4.79, -8.45) * mm});
            skLineSegment(sketch, "E456.0.34", {"start": v(-4.79, -8.45) * mm, "end": v(-4.79, -9.5) * mm});
            skArc(sketch, "E456.0.35", {"start": v(-4.79, -9.5) * mm, "mid": v(-4.64, -9.85) * mm, "end": v(-4.29, -10) * mm});
            skLineSegment(sketch, "E456.0.36", {"start": v(-4.29, -10) * mm, "end": v(9.71, -10) * mm});
            skArc(sketch, "E456.0.37", {"start": v(9.71, -10) * mm, "mid": v(10.07, -9.85) * mm, "end": v(10.21, -9.5) * mm});
            skLineSegment(sketch, "E456.0.38", {"start": v(10.21, -9.5) * mm, "end": v(10.21, -8.45) * mm});
            skArc(sketch, "E456.0.39", {"start": v(10.21, -8.45) * mm, "mid": v(10.14, -8.27) * mm, "end": v(9.96, -8.2) * mm});
            skLineSegment(sketch, "E456.0.40", {"start": v(9.96, -8.2) * mm, "end": v(8.27, -8.2) * mm});
            skArc(sketch, "E456.0.41", {"start": v(8.27, -8.2) * mm, "mid": v(7.25, -7.52) * mm, "end": v(7.5, -6.32) * mm});
            skLineSegment(sketch, "E456.0.42", {"start": v(7.5, -6.32) * mm, "end": v(9.77, -4.04) * mm});
            skArc(sketch, "E456.0.43", {"start": v(9.77, -4.04) * mm, "mid": v(10.26, -3.71) * mm, "end": v(10.84, -3.6) * mm});
            skLineSegment(sketch, "E456.0.44", {"start": v(10.84, -3.6) * mm, "end": v(14.6, -3.6) * mm});
            skArc(sketch, "E456.0.45", {"start": v(14.6, -3.6) * mm, "mid": v(15.17, -3.71) * mm, "end": v(15.65, -4.04) * mm});
            skLineSegment(sketch, "E456.0.46", {"start": v(15.65, -4.04) * mm, "end": v(17.94, -6.32) * mm});
            skArc(sketch, "E456.0.47", {"start": v(17.94, -6.32) * mm, "mid": v(18.17, -7.52) * mm, "end": v(17.16, -8.2) * mm});
            skLineSegment(sketch, "E456.0.48", {"start": v(17.16, -8.2) * mm, "end": v(15.46, -8.2) * mm});
            skArc(sketch, "E456.0.49", {"start": v(15.46, -8.2) * mm, "mid": v(15.29, -8.27) * mm, "end": v(15.21, -8.45) * mm});
            skLineSegment(sketch, "E456.0.50", {"start": v(15.21, -8.45) * mm, "end": v(15.21, -9.5) * mm});
            skArc(sketch, "E456.0.51", {"start": v(15.21, -9.5) * mm, "mid": v(15.36, -9.85) * mm, "end": v(15.71, -10) * mm});
            skArc(sketch, "E456.0.61", {"start": v(16.75, -2.94) * mm, "mid": v(16.43, -2.45) * mm, "end": v(16.31, -1.88) * mm});
            skLineSegment(sketch, "E456.0.62", {"start": v(16.31, -1.88) * mm, "end": v(16.31, 1.88) * mm});
            skArc(sketch, "E456.0.63", {"start": v(16.31, 1.88) * mm, "mid": v(16.43, 2.45) * mm, "end": v(16.75, 2.94) * mm});
            skArc(sketch, "E456.0.73", {"start": v(15.71, 10) * mm, "mid": v(15.36, 9.86) * mm, "end": v(15.21, 9.5) * mm});
            skLineSegment(sketch, "E456.0.74", {"start": v(15.21, 9.5) * mm, "end": v(15.21, 8.45) * mm});
            skArc(sketch, "E456.0.75", {"start": v(15.21, 8.45) * mm, "mid": v(15.29, 8.28) * mm, "end": v(15.46, 8.2) * mm});
            skLineSegment(sketch, "E456.0.76", {"start": v(15.46, 8.2) * mm, "end": v(17.16, 8.2) * mm});
            skArc(sketch, "E456.0.77", {"start": v(17.16, 8.2) * mm, "mid": v(18.17, 7.52) * mm, "end": v(17.94, 6.32) * mm});
            skLineSegment(sketch, "E456.0.78", {"start": v(17.94, 6.32) * mm, "end": v(15.65, 4.04) * mm});
            skArc(sketch, "E456.0.79", {"start": v(15.65, 4.04) * mm, "mid": v(15.17, 3.72) * mm, "end": v(14.6, 3.6) * mm});
            skLineSegment(sketch, "E456.0.80", {"start": v(14.6, 3.6) * mm, "end": v(10.84, 3.6) * mm});
            skArc(sketch, "E456.0.81", {"start": v(10.84, 3.6) * mm, "mid": v(10.26, 3.72) * mm, "end": v(9.77, 4.04) * mm});
            skLineSegment(sketch, "E456.0.82", {"start": v(9.77, 4.04) * mm, "end": v(7.5, 6.32) * mm});
            skArc(sketch, "E456.0.83", {"start": v(7.5, 6.32) * mm, "mid": v(7.25, 7.52) * mm, "end": v(8.27, 8.2) * mm});
            skLineSegment(sketch, "E456.0.84", {"start": v(8.27, 8.2) * mm, "end": v(9.96, 8.2) * mm});
            skArc(sketch, "E456.0.85", {"start": v(9.96, 8.2) * mm, "mid": v(10.14, 8.28) * mm, "end": v(10.21, 8.45) * mm});
            skLineSegment(sketch, "E456.0.86", {"start": v(10.21, 8.45) * mm, "end": v(10.21, 9.5) * mm});
            skArc(sketch, "E456.0.87", {"start": v(10.21, 9.5) * mm, "mid": v(10.07, 9.86) * mm, "end": v(9.71, 10) * mm});
            skLineSegment(sketch, "E456.0.88", {"start": v(9.71, 10) * mm, "end": v(-4.29, 10) * mm});
            skArc(sketch, "E456.0.89", {"start": v(-4.29, 10) * mm, "mid": v(-4.64, 9.86) * mm, "end": v(-4.79, 9.5) * mm});
            skLineSegment(sketch, "E456.0.90", {"start": v(-4.79, 9.5) * mm, "end": v(-4.79, 8.45) * mm});
            skArc(sketch, "E456.0.91", {"start": v(-4.79, 8.45) * mm, "mid": v(-4.71, 8.28) * mm, "end": v(-4.54, 8.2) * mm});
            skLineSegment(sketch, "E456.0.92", {"start": v(-4.54, 8.2) * mm, "end": v(-2.84, 8.2) * mm});
            skArc(sketch, "E456.0.93", {"start": v(-2.84, 8.2) * mm, "mid": v(-1.83, 7.52) * mm, "end": v(-2.06, 6.32) * mm});
            skLineSegment(sketch, "E456.0.94", {"start": v(-2.06, 6.32) * mm, "end": v(-4.35, 4.04) * mm});
            skArc(sketch, "E456.0.95", {"start": v(-4.35, 4.04) * mm, "mid": v(-4.83, 3.72) * mm, "end": v(-5.4, 3.6) * mm});
            skLineSegment(sketch, "E456.0.96", {"start": v(-5.4, 3.6) * mm, "end": v(-9.16, 3.6) * mm});
            skArc(sketch, "E456.0.97", {"start": v(-9.16, 3.6) * mm, "mid": v(-9.74, 3.72) * mm, "end": v(-10.23, 4.04) * mm});
            skLineSegment(sketch, "E456.0.98", {"start": v(-10.23, 4.04) * mm, "end": v(-12.5, 6.32) * mm});
            skArc(sketch, "E456.0.99", {"start": v(-12.5, 6.32) * mm, "mid": v(-12.75, 7.52) * mm, "end": v(-11.73, 8.2) * mm});
            skLineSegment(sketch, "E456.0.100", {"start": v(-11.73, 8.2) * mm, "end": v(-10.04, 8.2) * mm});
            skArc(sketch, "E456.0.101", {"start": v(-10.04, 8.2) * mm, "mid": v(-9.86, 8.28) * mm, "end": v(-9.79, 8.45) * mm});
            skLineSegment(sketch, "E456.0.102", {"start": v(-9.79, 8.45) * mm, "end": v(-9.79, 9.5) * mm});
            skArc(sketch, "E456.0.103", {"start": v(-9.79, 9.5) * mm, "mid": v(-9.93, 9.86) * mm, "end": v(-10.29, 10) * mm});
            skCircle(sketch, "E457.0.0", {"center": v(-7.29, 0) * mm, "radius": 2.15 * mm});
            skCircle(sketch, "E458.0.0", {"center": v(12.71, 0) * mm, "radius": 2.15 * mm});
            skLineSegment(sketch, "E459.0.0", {"start": v(1.57, 7.76) * mm, "end": v(-3.25, 2.94) * mm});
            skArc(sketch, "E459.0.1", {"start": v(-3.25, 2.94) * mm, "mid": v(-3.57, 2.45) * mm, "end": v(-3.69, 1.88) * mm});
            skLineSegment(sketch, "E459.0.2", {"start": v(-3.69, 1.88) * mm, "end": v(-3.69, -1.88) * mm});
            skArc(sketch, "E459.0.3", {"start": v(-3.69, -1.88) * mm, "mid": v(-3.57, -2.45) * mm, "end": v(-3.25, -2.94) * mm});
            skLineSegment(sketch, "E459.0.4", {"start": v(-3.25, -2.94) * mm, "end": v(1.57, -7.76) * mm});
            skArc(sketch, "E459.0.5", {"start": v(1.57, -7.76) * mm, "mid": v(2.06, -8.08) * mm, "end": v(2.64, -8.2) * mm});
            skLineSegment(sketch, "E459.0.6", {"start": v(2.64, -8.2) * mm, "end": v(2.8, -8.2) * mm});
            skArc(sketch, "E459.0.7", {"start": v(2.8, -8.2) * mm, "mid": v(3.37, -8.08) * mm, "end": v(3.85, -7.76) * mm});
            skLineSegment(sketch, "E459.0.8", {"start": v(3.85, -7.76) * mm, "end": v(8.67, -2.94) * mm});
            skArc(sketch, "E459.0.9", {"start": v(8.67, -2.94) * mm, "mid": v(9, -2.45) * mm, "end": v(9.11, -1.88) * mm});
            skLineSegment(sketch, "E459.0.10", {"start": v(9.11, -1.88) * mm, "end": v(9.11, 1.88) * mm});
            skArc(sketch, "E459.0.11", {"start": v(9.11, 1.88) * mm, "mid": v(9, 2.45) * mm, "end": v(8.67, 2.94) * mm});
            skLineSegment(sketch, "E459.0.12", {"start": v(8.67, 2.94) * mm, "end": v(3.85, 7.76) * mm});
            skArc(sketch, "E459.0.13", {"start": v(3.85, 7.76) * mm, "mid": v(3.37, 8.09) * mm, "end": v(2.8, 8.2) * mm});
            skLineSegment(sketch, "E459.0.14", {"start": v(2.8, 8.2) * mm, "end": v(2.64, 8.2) * mm});
            skArc(sketch, "E459.0.15", {"start": v(2.64, 8.2) * mm, "mid": v(2.06, 8.09) * mm, "end": v(1.57, 7.76) * mm});
            skLineSegment(sketch, "E460", {"start": v(22.71, 12.69) * mm, "end": v(22.71, -12.08) * mm, "construction": true});
            skCircle(sketch, "E461.0.MirrorC", {"center": v(32.71, 0) * mm, "radius": 2.15 * mm});
            skCircle(sketch, "E462.0.MirrorC", {"center": v(52.71, 0) * mm, "radius": 2.15 * mm});
            skArc(sketch, "E463.0.MirrorCS", {"start": v(29.11, 1.88) * mm, "mid": v(29, 2.45) * mm, "end": v(28.67, 2.94) * mm});
            skLineSegment(sketch, "E464.0.MirrorCS", {"start": v(29.11, -1.88) * mm, "end": v(29.11, 1.88) * mm});
            skArc(sketch, "E465.0.MirrorCS", {"start": v(28.67, -2.94) * mm, "mid": v(29, -2.45) * mm, "end": v(29.11, -1.88) * mm});
            skArc(sketch, "E466.0.MirrorCS", {"start": v(29.71, 10) * mm, "mid": v(30.07, 9.86) * mm, "end": v(30.21, 9.5) * mm});
            skLineSegment(sketch, "E467.0.MirrorCS", {"start": v(30.21, 9.5) * mm, "end": v(30.21, 8.45) * mm});
            skArc(sketch, "E468.0.MirrorCS", {"start": v(30.21, 8.45) * mm, "mid": v(30.14, 8.28) * mm, "end": v(29.96, 8.2) * mm});
            skLineSegment(sketch, "E469.0.MirrorCS", {"start": v(29.96, 8.2) * mm, "end": v(28.27, 8.2) * mm});
            skArc(sketch, "E470.0.MirrorCS", {"start": v(28.27, 8.2) * mm, "mid": v(27.25, 7.52) * mm, "end": v(27.5, 6.32) * mm});
            skLineSegment(sketch, "E471.0.MirrorCS", {"start": v(27.5, 6.32) * mm, "end": v(29.77, 4.04) * mm});
            skArc(sketch, "E472.0.MirrorCS", {"start": v(29.77, 4.04) * mm, "mid": v(30.26, 3.72) * mm, "end": v(30.84, 3.6) * mm});
            skLineSegment(sketch, "E473.0.MirrorCS", {"start": v(30.84, 3.6) * mm, "end": v(34.6, 3.6) * mm});
            skArc(sketch, "E474.0.MirrorCS", {"start": v(34.6, 3.6) * mm, "mid": v(35.17, 3.72) * mm, "end": v(35.65, 4.04) * mm});
            skLineSegment(sketch, "E475.0.MirrorCS", {"start": v(35.65, 4.04) * mm, "end": v(37.94, 6.32) * mm});
            skArc(sketch, "E476.0.MirrorCS", {"start": v(37.94, 6.32) * mm, "mid": v(38.17, 7.52) * mm, "end": v(37.16, 8.2) * mm});
            skLineSegment(sketch, "E477.0.MirrorCS", {"start": v(37.16, 8.2) * mm, "end": v(35.46, 8.2) * mm});
            skArc(sketch, "E478.0.MirrorCS", {"start": v(35.46, 8.2) * mm, "mid": v(35.29, 8.28) * mm, "end": v(35.21, 8.45) * mm});
            skLineSegment(sketch, "E479.0.MirrorCS", {"start": v(35.21, 8.45) * mm, "end": v(35.21, 9.5) * mm});
            skArc(sketch, "E480.0.MirrorCS", {"start": v(35.21, 9.5) * mm, "mid": v(35.36, 9.86) * mm, "end": v(35.71, 10) * mm});
            skLineSegment(sketch, "E481.0.MirrorCS", {"start": v(35.71, 10) * mm, "end": v(49.71, 10) * mm});
            skArc(sketch, "E482.0.MirrorCS", {"start": v(49.71, 10) * mm, "mid": v(50.07, 9.86) * mm, "end": v(50.21, 9.5) * mm});
            skLineSegment(sketch, "E483.0.MirrorCS", {"start": v(50.21, 9.5) * mm, "end": v(50.21, 8.45) * mm});
            skArc(sketch, "E484.0.MirrorCS", {"start": v(50.21, 8.45) * mm, "mid": v(50.14, 8.28) * mm, "end": v(49.96, 8.2) * mm});
            skLineSegment(sketch, "E485.0.MirrorCS", {"start": v(49.96, 8.2) * mm, "end": v(48.27, 8.2) * mm});
            skArc(sketch, "E486.0.MirrorCS", {"start": v(48.27, 8.2) * mm, "mid": v(47.25, 7.52) * mm, "end": v(47.5, 6.32) * mm});
            skLineSegment(sketch, "E487.0.MirrorCS", {"start": v(47.5, 6.32) * mm, "end": v(49.77, 4.04) * mm});
            skArc(sketch, "E488.0.MirrorCS", {"start": v(49.77, 4.04) * mm, "mid": v(50.26, 3.72) * mm, "end": v(50.84, 3.6) * mm});
            skLineSegment(sketch, "E489.0.MirrorCS", {"start": v(50.84, 3.6) * mm, "end": v(54.6, 3.6) * mm});
            skArc(sketch, "E490.0.MirrorCS", {"start": v(54.6, 3.6) * mm, "mid": v(55.17, 3.72) * mm, "end": v(55.65, 4.04) * mm});
            skLineSegment(sketch, "E491.0.MirrorCS", {"start": v(55.65, 4.04) * mm, "end": v(57.94, 6.32) * mm});
            skArc(sketch, "E492.0.MirrorCS", {"start": v(57.94, 6.32) * mm, "mid": v(58.17, 7.52) * mm, "end": v(57.16, 8.2) * mm});
            skLineSegment(sketch, "E493.0.MirrorCS", {"start": v(57.16, 8.2) * mm, "end": v(55.46, 8.2) * mm});
            skArc(sketch, "E494.0.MirrorCS", {"start": v(55.46, 8.2) * mm, "mid": v(55.29, 8.28) * mm, "end": v(55.21, 8.45) * mm});
            skLineSegment(sketch, "E495.0.MirrorCS", {"start": v(55.21, 8.45) * mm, "end": v(55.21, 9.5) * mm});
            skArc(sketch, "E496.0.MirrorCS", {"start": v(55.21, 9.5) * mm, "mid": v(55.36, 9.86) * mm, "end": v(55.71, 10) * mm});
            skLineSegment(sketch, "E497.0.MirrorCS", {"start": v(55.71, 10) * mm, "end": v(61.21, 10) * mm});
            skArc(sketch, "E498.0.MirrorCS", {"start": v(61.21, 10) * mm, "mid": v(62.27, 9.56) * mm, "end": v(62.71, 8.5) * mm});
            skLineSegment(sketch, "E499.0.MirrorCS", {"start": v(62.71, 8.5) * mm, "end": v(62.71, 3) * mm});
            skArc(sketch, "E500.0.MirrorCS", {"start": v(62.71, 3) * mm, "mid": v(62.57, 2.65) * mm, "end": v(62.21, 2.5) * mm});
            skLineSegment(sketch, "E501.0.MirrorCS", {"start": v(62.21, 2.5) * mm, "end": v(61.16, 2.5) * mm});
            skArc(sketch, "E502.0.MirrorCS", {"start": v(61.16, 2.5) * mm, "mid": v(60.99, 2.58) * mm, "end": v(60.91, 2.75) * mm});
            skLineSegment(sketch, "E503.0.MirrorCS", {"start": v(60.91, 2.75) * mm, "end": v(60.91, 4.45) * mm});
            skArc(sketch, "E504.0.MirrorCS", {"start": v(60.91, 4.45) * mm, "mid": v(60.23, 5.46) * mm, "end": v(59.04, 5.22) * mm});
            skLineSegment(sketch, "E505.0.MirrorCS", {"start": v(59.04, 5.22) * mm, "end": v(56.75, 2.94) * mm});
            skArc(sketch, "E506.0.MirrorCS", {"start": v(56.75, 2.94) * mm, "mid": v(56.43, 2.45) * mm, "end": v(56.31, 1.88) * mm});
            skLineSegment(sketch, "E507.0.MirrorCS", {"start": v(56.31, 1.88) * mm, "end": v(56.31, -1.88) * mm});
            skArc(sketch, "E508.0.MirrorCS", {"start": v(56.31, -1.88) * mm, "mid": v(56.43, -2.45) * mm, "end": v(56.75, -2.94) * mm});
            skLineSegment(sketch, "E509.0.MirrorCS", {"start": v(56.75, -2.94) * mm, "end": v(59.04, -5.22) * mm});
            skArc(sketch, "E510.0.MirrorCS", {"start": v(59.04, -5.22) * mm, "mid": v(60.23, -5.46) * mm, "end": v(60.91, -4.44) * mm});
            skLineSegment(sketch, "E511.0.MirrorCS", {"start": v(60.91, -4.44) * mm, "end": v(60.91, -2.75) * mm});
            skArc(sketch, "E512.0.MirrorCS", {"start": v(60.91, -2.75) * mm, "mid": v(60.99, -2.57) * mm, "end": v(61.16, -2.5) * mm});
            skLineSegment(sketch, "E513.0.MirrorCS", {"start": v(61.16, -2.5) * mm, "end": v(62.21, -2.5) * mm});
            skArc(sketch, "E514.0.MirrorCS", {"start": v(62.21, -2.5) * mm, "mid": v(62.57, -2.64) * mm, "end": v(62.71, -3) * mm});
            skLineSegment(sketch, "E515.0.MirrorCS", {"start": v(62.71, -3) * mm, "end": v(62.71, -8.5) * mm});
            skArc(sketch, "E516.0.MirrorCS", {"start": v(62.71, -8.5) * mm, "mid": v(62.27, -9.56) * mm, "end": v(61.21, -10) * mm});
            skLineSegment(sketch, "E517.0.MirrorCS", {"start": v(61.21, -10) * mm, "end": v(55.71, -10) * mm});
            skArc(sketch, "E518.0.MirrorCS", {"start": v(55.71, -10) * mm, "mid": v(55.36, -9.85) * mm, "end": v(55.21, -9.5) * mm});
            skLineSegment(sketch, "E519.0.MirrorCS", {"start": v(55.21, -9.5) * mm, "end": v(55.21, -8.45) * mm});
            skArc(sketch, "E520.0.MirrorCS", {"start": v(55.21, -8.45) * mm, "mid": v(55.29, -8.27) * mm, "end": v(55.46, -8.2) * mm});
            skLineSegment(sketch, "E521.0.MirrorCS", {"start": v(55.46, -8.2) * mm, "end": v(57.16, -8.2) * mm});
            skArc(sketch, "E522.0.MirrorCS", {"start": v(57.16, -8.2) * mm, "mid": v(58.17, -7.52) * mm, "end": v(57.94, -6.32) * mm});
            skLineSegment(sketch, "E523.0.MirrorCS", {"start": v(57.94, -6.32) * mm, "end": v(55.65, -4.04) * mm});
            skArc(sketch, "E524.0.MirrorCS", {"start": v(55.65, -4.04) * mm, "mid": v(55.17, -3.71) * mm, "end": v(54.6, -3.6) * mm});
            skLineSegment(sketch, "E525.0.MirrorCS", {"start": v(54.6, -3.6) * mm, "end": v(50.84, -3.6) * mm});
            skArc(sketch, "E526.0.MirrorCS", {"start": v(50.84, -3.6) * mm, "mid": v(50.26, -3.71) * mm, "end": v(49.77, -4.04) * mm});
            skLineSegment(sketch, "E527.0.MirrorCS", {"start": v(49.77, -4.04) * mm, "end": v(47.5, -6.32) * mm});
            skArc(sketch, "E528.0.MirrorCS", {"start": v(47.5, -6.32) * mm, "mid": v(47.25, -7.52) * mm, "end": v(48.27, -8.2) * mm});
            skLineSegment(sketch, "E529.0.MirrorCS", {"start": v(48.27, -8.2) * mm, "end": v(49.96, -8.2) * mm});
            skArc(sketch, "E530.0.MirrorCS", {"start": v(49.96, -8.2) * mm, "mid": v(50.14, -8.27) * mm, "end": v(50.21, -8.45) * mm});
            skLineSegment(sketch, "E531.0.MirrorCS", {"start": v(50.21, -8.45) * mm, "end": v(50.21, -9.5) * mm});
            skArc(sketch, "E532.0.MirrorCS", {"start": v(50.21, -9.5) * mm, "mid": v(50.07, -9.85) * mm, "end": v(49.71, -10) * mm});
            skLineSegment(sketch, "E533.0.MirrorCS", {"start": v(49.71, -10) * mm, "end": v(35.71, -10) * mm});
            skArc(sketch, "E534.0.MirrorCS", {"start": v(35.71, -10) * mm, "mid": v(35.36, -9.85) * mm, "end": v(35.21, -9.5) * mm});
            skLineSegment(sketch, "E535.0.MirrorCS", {"start": v(35.21, -9.5) * mm, "end": v(35.21, -8.45) * mm});
            skArc(sketch, "E536.0.MirrorCS", {"start": v(35.21, -8.45) * mm, "mid": v(35.29, -8.27) * mm, "end": v(35.46, -8.2) * mm});
            skLineSegment(sketch, "E537.0.MirrorCS", {"start": v(35.46, -8.2) * mm, "end": v(37.16, -8.2) * mm});
            skArc(sketch, "E538.0.MirrorCS", {"start": v(37.16, -8.2) * mm, "mid": v(38.17, -7.52) * mm, "end": v(37.94, -6.32) * mm});
            skLineSegment(sketch, "E539.0.MirrorCS", {"start": v(37.94, -6.32) * mm, "end": v(35.65, -4.04) * mm});
            skArc(sketch, "E540.0.MirrorCS", {"start": v(35.65, -4.04) * mm, "mid": v(35.17, -3.71) * mm, "end": v(34.6, -3.6) * mm});
            skLineSegment(sketch, "E541.0.MirrorCS", {"start": v(34.6, -3.6) * mm, "end": v(30.84, -3.6) * mm});
            skArc(sketch, "E542.0.MirrorCS", {"start": v(30.84, -3.6) * mm, "mid": v(30.26, -3.71) * mm, "end": v(29.77, -4.04) * mm});
            skLineSegment(sketch, "E543.0.MirrorCS", {"start": v(29.77, -4.04) * mm, "end": v(27.5, -6.32) * mm});
            skArc(sketch, "E544.0.MirrorCS", {"start": v(27.5, -6.32) * mm, "mid": v(27.25, -7.52) * mm, "end": v(28.27, -8.2) * mm});
            skLineSegment(sketch, "E545.0.MirrorCS", {"start": v(28.27, -8.2) * mm, "end": v(29.96, -8.2) * mm});
            skArc(sketch, "E546.0.MirrorCS", {"start": v(29.96, -8.2) * mm, "mid": v(30.14, -8.27) * mm, "end": v(30.21, -8.45) * mm});
            skLineSegment(sketch, "E547.0.MirrorCS", {"start": v(30.21, -8.45) * mm, "end": v(30.21, -9.5) * mm});
            skArc(sketch, "E548.0.MirrorCS", {"start": v(30.21, -9.5) * mm, "mid": v(30.07, -9.85) * mm, "end": v(29.71, -10) * mm});
            skLineSegment(sketch, "E549.0.MirrorCS", {"start": v(36.31, -1.88) * mm, "end": v(36.31, 1.88) * mm});
            skArc(sketch, "E550.0.MirrorCS", {"start": v(36.31, 1.88) * mm, "mid": v(36.43, 2.45) * mm, "end": v(36.75, 2.94) * mm});
            skLineSegment(sketch, "E551.0.MirrorCS", {"start": v(36.75, 2.94) * mm, "end": v(41.57, 7.76) * mm});
            skArc(sketch, "E552.0.MirrorCS", {"start": v(41.57, 7.76) * mm, "mid": v(42.06, 8.09) * mm, "end": v(42.64, 8.2) * mm});
            skLineSegment(sketch, "E553.0.MirrorCS", {"start": v(42.64, 8.2) * mm, "end": v(42.8, 8.2) * mm});
            skArc(sketch, "E554.0.MirrorCS", {"start": v(42.8, 8.2) * mm, "mid": v(43.37, 8.09) * mm, "end": v(43.85, 7.76) * mm});
            skLineSegment(sketch, "E555.0.MirrorCS", {"start": v(43.85, 7.76) * mm, "end": v(48.67, 2.94) * mm});
            skArc(sketch, "E556.0.MirrorCS", {"start": v(48.67, 2.94) * mm, "mid": v(49, 2.45) * mm, "end": v(49.11, 1.88) * mm});
            skLineSegment(sketch, "E557.0.MirrorCS", {"start": v(49.11, 1.88) * mm, "end": v(49.11, -1.88) * mm});
            skArc(sketch, "E558.0.MirrorCS", {"start": v(49.11, -1.88) * mm, "mid": v(49, -2.45) * mm, "end": v(48.67, -2.94) * mm});
            skLineSegment(sketch, "E559.0.MirrorCS", {"start": v(48.67, -2.94) * mm, "end": v(43.85, -7.76) * mm});
            skArc(sketch, "E560.0.MirrorCS", {"start": v(43.85, -7.76) * mm, "mid": v(43.37, -8.08) * mm, "end": v(42.8, -8.2) * mm});
            skLineSegment(sketch, "E561.0.MirrorCS", {"start": v(42.8, -8.2) * mm, "end": v(42.64, -8.2) * mm});
            skArc(sketch, "E562.0.MirrorCS", {"start": v(42.64, -8.2) * mm, "mid": v(42.06, -8.08) * mm, "end": v(41.57, -7.76) * mm});
            skLineSegment(sketch, "E563.0.MirrorCS", {"start": v(41.57, -7.76) * mm, "end": v(36.75, -2.94) * mm});
            skArc(sketch, "E564.0.MirrorCS", {"start": v(36.75, -2.94) * mm, "mid": v(36.43, -2.45) * mm, "end": v(36.31, -1.88) * mm});
            skLineSegment(sketch, "E565", {"start": v(15.71, 10) * mm, "end": v(29.71, 10) * mm});
            skLineSegment(sketch, "E566", {"start": v(15.71, -10) * mm, "end": v(29.71, -10) * mm});
            skLineSegment(sketch, "E567", {"start": v(12.71, 12.57) * mm, "end": v(12.71, -12.54) * mm, "construction": true});
            skLineSegment(sketch, "E568.0.MirrorCS", {"start": v(21.57, -7.76) * mm, "end": v(16.75, -2.94) * mm});
            skLineSegment(sketch, "E569.0.MirrorCS", {"start": v(16.75, 2.94) * mm, "end": v(21.57, 7.76) * mm});
            skLineSegment(sketch, "E570.0.MirrorCS", {"start": v(23.85, 7.76) * mm, "end": v(28.67, 2.94) * mm});
            skLineSegment(sketch, "E571.0.MirrorCS", {"start": v(28.67, -2.94) * mm, "end": v(23.85, -7.76) * mm});
            skArc(sketch, "E572.0.MirrorCS", {"start": v(22.8, 8.2) * mm, "mid": v(23.37, 8.09) * mm, "end": v(23.85, 7.76) * mm});
            skArc(sketch, "E573.0.MirrorCS", {"start": v(21.57, 7.76) * mm, "mid": v(22.06, 8.09) * mm, "end": v(22.64, 8.2) * mm});
            skArc(sketch, "E574.0.MirrorCS", {"start": v(23.85, -7.76) * mm, "mid": v(23.37, -8.08) * mm, "end": v(22.8, -8.2) * mm});
            skArc(sketch, "E575.0.MirrorCS", {"start": v(22.64, -8.2) * mm, "mid": v(22.06, -8.08) * mm, "end": v(21.57, -7.76) * mm});
            skLineSegment(sketch, "E576.0.MirrorCS", {"start": v(22.8, -8.2) * mm, "end": v(22.64, -8.2) * mm});
            skLineSegment(sketch, "E577.0.MirrorCS", {"start": v(22.64, 8.2) * mm, "end": v(22.8, 8.2) * mm});
            skSolve(sketch);
        }
        {
            var Q0;
            Q0=qCreatedBy(makeId("Front.planeOp"),FACE);
            var sketch = newSketch(context, id + "F6", { "sketchPlane" : qUnion([Q0])});
            skLineSegment(sketch, "E578.0.0", {"start": v(-10.29, 10) * mm, "end": v(-15.79, 10) * mm});
            skArc(sketch, "E578.0.1", {"start": v(-15.79, 10) * mm, "mid": v(-16.85, 9.56) * mm, "end": v(-17.29, 8.5) * mm});
            skLineSegment(sketch, "E578.0.2", {"start": v(-17.29, 8.5) * mm, "end": v(-17.29, 3) * mm});
            skArc(sketch, "E578.0.3", {"start": v(-17.29, 3) * mm, "mid": v(-17.14, 2.65) * mm, "end": v(-16.79, 2.5) * mm});
            skLineSegment(sketch, "E578.0.4", {"start": v(-16.79, 2.5) * mm, "end": v(-15.74, 2.5) * mm});
            skArc(sketch, "E578.0.5", {"start": v(-15.74, 2.5) * mm, "mid": v(-15.56, 2.58) * mm, "end": v(-15.49, 2.75) * mm});
            skLineSegment(sketch, "E578.0.6", {"start": v(-15.49, 2.75) * mm, "end": v(-15.49, 4.45) * mm});
            skArc(sketch, "E578.0.7", {"start": v(-15.49, 4.45) * mm, "mid": v(-14.8, 5.46) * mm, "end": v(-13.6, 5.22) * mm});
            skLineSegment(sketch, "E578.0.8", {"start": v(-13.6, 5.22) * mm, "end": v(-11.33, 2.94) * mm});
            skArc(sketch, "E578.0.9", {"start": v(-11.33, 2.94) * mm, "mid": v(-11, 2.45) * mm, "end": v(-10.89, 1.88) * mm});
            skLineSegment(sketch, "E578.0.10", {"start": v(-10.89, 1.88) * mm, "end": v(-10.89, -1.88) * mm});
            skArc(sketch, "E578.0.11", {"start": v(-10.89, -1.88) * mm, "mid": v(-11, -2.45) * mm, "end": v(-11.33, -2.94) * mm});
            skLineSegment(sketch, "E578.0.12", {"start": v(-11.33, -2.94) * mm, "end": v(-13.6, -5.22) * mm});
            skArc(sketch, "E578.0.13", {"start": v(-13.6, -5.22) * mm, "mid": v(-14.8, -5.46) * mm, "end": v(-15.49, -4.44) * mm});
            skLineSegment(sketch, "E578.0.14", {"start": v(-15.49, -4.44) * mm, "end": v(-15.49, -2.75) * mm});
            skArc(sketch, "E578.0.15", {"start": v(-15.49, -2.75) * mm, "mid": v(-15.56, -2.57) * mm, "end": v(-15.74, -2.5) * mm});
            skLineSegment(sketch, "E578.0.16", {"start": v(-15.74, -2.5) * mm, "end": v(-16.79, -2.5) * mm});
            skArc(sketch, "E578.0.17", {"start": v(-16.79, -2.5) * mm, "mid": v(-17.14, -2.64) * mm, "end": v(-17.29, -3) * mm});
            skArc(sketch, "E578.0.27", {"start": v(-10.23, -4.04) * mm, "mid": v(-9.74, -3.71) * mm, "end": v(-9.16, -3.6) * mm});
            skLineSegment(sketch, "E578.0.28", {"start": v(-9.16, -3.6) * mm, "end": v(-5.4, -3.6) * mm});
            skLineSegment(sketch, "E578.0.44", {"start": v(10.84, -3.6) * mm, "end": v(14.6, -3.6) * mm});
            skArc(sketch, "E578.0.45", {"start": v(14.6, -3.6) * mm, "mid": v(15.17, -3.71) * mm, "end": v(15.65, -4.04) * mm});
            skArc(sketch, "E578.0.55", {"start": v(22.71, -3) * mm, "mid": v(22.57, -2.64) * mm, "end": v(22.21, -2.5) * mm});
            skLineSegment(sketch, "E578.0.56", {"start": v(22.21, -2.5) * mm, "end": v(21.16, -2.5) * mm});
            skArc(sketch, "E578.0.57", {"start": v(21.16, -2.5) * mm, "mid": v(20.99, -2.57) * mm, "end": v(20.91, -2.75) * mm});
            skLineSegment(sketch, "E578.0.58", {"start": v(20.91, -2.75) * mm, "end": v(20.91, -4.44) * mm});
            skArc(sketch, "E578.0.59", {"start": v(20.91, -4.44) * mm, "mid": v(20.23, -5.46) * mm, "end": v(19.04, -5.22) * mm});
            skLineSegment(sketch, "E578.0.60", {"start": v(19.04, -5.22) * mm, "end": v(16.75, -2.94) * mm});
            skArc(sketch, "E578.0.61", {"start": v(16.75, -2.94) * mm, "mid": v(16.43, -2.45) * mm, "end": v(16.31, -1.88) * mm});
            skLineSegment(sketch, "E578.0.62", {"start": v(16.31, -1.88) * mm, "end": v(16.31, 1.88) * mm});
            skArc(sketch, "E578.0.63", {"start": v(16.31, 1.88) * mm, "mid": v(16.43, 2.45) * mm, "end": v(16.75, 2.94) * mm});
            skLineSegment(sketch, "E578.0.64", {"start": v(16.75, 2.94) * mm, "end": v(19.04, 5.22) * mm});
            skArc(sketch, "E578.0.65", {"start": v(19.04, 5.22) * mm, "mid": v(20.23, 5.46) * mm, "end": v(20.91, 4.45) * mm});
            skLineSegment(sketch, "E578.0.66", {"start": v(20.91, 4.45) * mm, "end": v(20.91, 2.75) * mm});
            skArc(sketch, "E578.0.67", {"start": v(20.91, 2.75) * mm, "mid": v(20.99, 2.58) * mm, "end": v(21.16, 2.5) * mm});
            skLineSegment(sketch, "E578.0.68", {"start": v(21.16, 2.5) * mm, "end": v(22.21, 2.5) * mm});
            skArc(sketch, "E578.0.69", {"start": v(22.21, 2.5) * mm, "mid": v(22.57, 2.65) * mm, "end": v(22.71, 3) * mm});
            skLineSegment(sketch, "E578.0.70", {"start": v(22.71, 3) * mm, "end": v(22.71, 8.5) * mm});
            skArc(sketch, "E578.0.71", {"start": v(22.71, 8.5) * mm, "mid": v(22.27, 9.56) * mm, "end": v(21.21, 10) * mm});
            skLineSegment(sketch, "E578.0.72", {"start": v(21.21, 10) * mm, "end": v(15.71, 10) * mm});
            skArc(sketch, "E578.0.73", {"start": v(15.71, 10) * mm, "mid": v(15.36, 9.86) * mm, "end": v(15.21, 9.5) * mm});
            skLineSegment(sketch, "E578.0.74", {"start": v(15.21, 9.5) * mm, "end": v(15.21, 8.45) * mm});
            skArc(sketch, "E578.0.75", {"start": v(15.21, 8.45) * mm, "mid": v(15.29, 8.28) * mm, "end": v(15.46, 8.2) * mm});
            skLineSegment(sketch, "E578.0.76", {"start": v(15.46, 8.2) * mm, "end": v(17.16, 8.2) * mm});
            skArc(sketch, "E578.0.77", {"start": v(17.16, 8.2) * mm, "mid": v(18.17, 7.52) * mm, "end": v(17.94, 6.32) * mm});
            skLineSegment(sketch, "E578.0.78", {"start": v(17.94, 6.32) * mm, "end": v(15.65, 4.04) * mm});
            skArc(sketch, "E578.0.79", {"start": v(15.65, 4.04) * mm, "mid": v(15.17, 3.72) * mm, "end": v(14.6, 3.6) * mm});
            skLineSegment(sketch, "E578.0.80", {"start": v(14.6, 3.6) * mm, "end": v(10.84, 3.6) * mm});
            skArc(sketch, "E578.0.81", {"start": v(10.84, 3.6) * mm, "mid": v(10.26, 3.72) * mm, "end": v(9.77, 4.04) * mm});
            skLineSegment(sketch, "E578.0.82", {"start": v(9.77, 4.04) * mm, "end": v(7.5, 6.32) * mm});
            skArc(sketch, "E578.0.83", {"start": v(7.5, 6.32) * mm, "mid": v(7.25, 7.52) * mm, "end": v(8.27, 8.2) * mm});
            skLineSegment(sketch, "E578.0.84", {"start": v(8.27, 8.2) * mm, "end": v(9.96, 8.2) * mm});
            skArc(sketch, "E578.0.85", {"start": v(9.96, 8.2) * mm, "mid": v(10.14, 8.28) * mm, "end": v(10.21, 8.45) * mm});
            skLineSegment(sketch, "E578.0.86", {"start": v(10.21, 8.45) * mm, "end": v(10.21, 9.5) * mm});
            skArc(sketch, "E578.0.87", {"start": v(10.21, 9.5) * mm, "mid": v(10.07, 9.86) * mm, "end": v(9.71, 10) * mm});
            skLineSegment(sketch, "E578.0.88", {"start": v(9.71, 10) * mm, "end": v(-4.29, 10) * mm});
            skArc(sketch, "E578.0.89", {"start": v(-4.29, 10) * mm, "mid": v(-4.64, 9.86) * mm, "end": v(-4.79, 9.5) * mm});
            skLineSegment(sketch, "E578.0.90", {"start": v(-4.79, 9.5) * mm, "end": v(-4.79, 8.45) * mm});
            skArc(sketch, "E578.0.91", {"start": v(-4.79, 8.45) * mm, "mid": v(-4.71, 8.28) * mm, "end": v(-4.54, 8.2) * mm});
            skLineSegment(sketch, "E578.0.92", {"start": v(-4.54, 8.2) * mm, "end": v(-2.84, 8.2) * mm});
            skArc(sketch, "E578.0.93", {"start": v(-2.84, 8.2) * mm, "mid": v(-1.83, 7.52) * mm, "end": v(-2.06, 6.32) * mm});
            skLineSegment(sketch, "E578.0.94", {"start": v(-2.06, 6.32) * mm, "end": v(-4.35, 4.04) * mm});
            skArc(sketch, "E578.0.95", {"start": v(-4.35, 4.04) * mm, "mid": v(-4.83, 3.72) * mm, "end": v(-5.4, 3.6) * mm});
            skLineSegment(sketch, "E578.0.96", {"start": v(-5.4, 3.6) * mm, "end": v(-9.16, 3.6) * mm});
            skArc(sketch, "E578.0.97", {"start": v(-9.16, 3.6) * mm, "mid": v(-9.74, 3.72) * mm, "end": v(-10.23, 4.04) * mm});
            skLineSegment(sketch, "E578.0.98", {"start": v(-10.23, 4.04) * mm, "end": v(-12.5, 6.32) * mm});
            skArc(sketch, "E578.0.99", {"start": v(-12.5, 6.32) * mm, "mid": v(-12.75, 7.52) * mm, "end": v(-11.73, 8.2) * mm});
            skLineSegment(sketch, "E578.0.100", {"start": v(-11.73, 8.2) * mm, "end": v(-10.04, 8.2) * mm});
            skArc(sketch, "E578.0.101", {"start": v(-10.04, 8.2) * mm, "mid": v(-9.86, 8.28) * mm, "end": v(-9.79, 8.45) * mm});
            skLineSegment(sketch, "E578.0.102", {"start": v(-9.79, 8.45) * mm, "end": v(-9.79, 9.5) * mm});
            skArc(sketch, "E578.0.103", {"start": v(-9.79, 9.5) * mm, "mid": v(-9.93, 9.86) * mm, "end": v(-10.29, 10) * mm});
            skCircle(sketch, "E579.0", {"center": v(-7.29, 0) * mm, "radius": 2.15 * mm});
            skLineSegment(sketch, "E580.0.0", {"start": v(1.57, 7.76) * mm, "end": v(-3.25, 2.94) * mm});
            skArc(sketch, "E580.0.1", {"start": v(-3.25, 2.94) * mm, "mid": v(-3.57, 2.45) * mm, "end": v(-3.69, 1.88) * mm});
            skLineSegment(sketch, "E580.0.2", {"start": v(-3.69, 1.88) * mm, "end": v(-3.69, -1.88) * mm});
            skLineSegment(sketch, "E580.0.10", {"start": v(9.11, -1.88) * mm, "end": v(9.11, 1.88) * mm});
            skArc(sketch, "E580.0.11", {"start": v(9.11, 1.88) * mm, "mid": v(9, 2.45) * mm, "end": v(8.67, 2.94) * mm});
            skLineSegment(sketch, "E580.0.12", {"start": v(8.67, 2.94) * mm, "end": v(3.85, 7.76) * mm});
            skArc(sketch, "E580.0.13", {"start": v(3.85, 7.76) * mm, "mid": v(3.37, 8.09) * mm, "end": v(2.8, 8.2) * mm});
            skLineSegment(sketch, "E580.0.14", {"start": v(2.8, 8.2) * mm, "end": v(2.64, 8.2) * mm});
            skArc(sketch, "E580.0.15", {"start": v(2.64, 8.2) * mm, "mid": v(2.06, 8.09) * mm, "end": v(1.57, 7.76) * mm});
            skCircle(sketch, "E581.0.0", {"center": v(12.71, 0) * mm, "radius": 2.15 * mm});
            skLineSegment(sketch, "E582.1", {"start": v(-15.79, 10) * mm, "end": v(-10.29, 10) * mm});
            skLineSegment(sketch, "E582.3", {"start": v(-9.79, 9.5) * mm, "end": v(-9.79, 8.45) * mm});
            skLineSegment(sketch, "E582.5", {"start": v(-10.04, 8.2) * mm, "end": v(-11.73, 8.2) * mm});
            skArc(sketch, "E582.6", {"start": v(-11.73, 8.2) * mm, "mid": v(-12.75, 7.52) * mm, "end": v(-12.5, 6.32) * mm});
            skArc(sketch, "E582.8", {"start": v(-10.23, 4.04) * mm, "mid": v(-9.74, 3.72) * mm, "end": v(-9.16, 3.6) * mm});
            skLineSegment(sketch, "E582.9", {"start": v(-9.16, 3.6) * mm, "end": v(-5.4, 3.6) * mm});
            skArc(sketch, "E582.10", {"start": v(-5.4, 3.6) * mm, "mid": v(-4.83, 3.72) * mm, "end": v(-4.35, 4.04) * mm});
            skLineSegment(sketch, "E582.11", {"start": v(-4.35, 4.04) * mm, "end": v(-2.06, 6.32) * mm});
            skArc(sketch, "E582.12", {"start": v(-2.06, 6.32) * mm, "mid": v(-1.83, 7.52) * mm, "end": v(-2.84, 8.2) * mm});
            skLineSegment(sketch, "E582.13", {"start": v(-2.84, 8.2) * mm, "end": v(-4.54, 8.2) * mm});
            skLineSegment(sketch, "E582.19", {"start": v(-15.74, 2.5) * mm, "end": v(-16.79, 2.5) * mm});
            skLineSegment(sketch, "E582.21", {"start": v(-15.49, 4.45) * mm, "end": v(-15.49, 2.75) * mm});
            skArc(sketch, "E582.22", {"start": v(-13.6, 5.22) * mm, "mid": v(-14.8, 5.46) * mm, "end": v(-15.49, 4.45) * mm});
            skLineSegment(sketch, "E582.23", {"start": v(-11.33, 2.94) * mm, "end": v(-13.6, 5.22) * mm});
            skArc(sketch, "E582.24", {"start": v(-10.89, 1.88) * mm, "mid": v(-11, 2.45) * mm, "end": v(-11.33, 2.94) * mm});
            skArc(sketch, "E582.26", {"start": v(-11.33, -2.94) * mm, "mid": v(-11, -2.45) * mm, "end": v(-10.89, -1.88) * mm});
            skArc(sketch, "E582.28", {"start": v(-15.49, -4.44) * mm, "mid": v(-14.8, -5.46) * mm, "end": v(-13.6, -5.22) * mm});
            skLineSegment(sketch, "E582.29", {"start": v(-15.49, -2.75) * mm, "end": v(-15.49, -4.44) * mm});
            skArc(sketch, "E582.42", {"start": v(-9.16, -3.6) * mm, "mid": v(-9.74, -3.71) * mm, "end": v(-10.23, -4.04) * mm});
            skArc(sketch, "E582.57", {"start": v(8.67, 2.94) * mm, "mid": v(9, 2.45) * mm, "end": v(9.11, 1.88) * mm});
            skLineSegment(sketch, "E582.58", {"start": v(9.11, 1.88) * mm, "end": v(9.11, -1.88) * mm});
            skArc(sketch, "E582.64", {"start": v(9.71, 10) * mm, "mid": v(10.07, 9.86) * mm, "end": v(10.21, 9.5) * mm});
            skLineSegment(sketch, "E582.65", {"start": v(10.21, 9.5) * mm, "end": v(10.21, 8.45) * mm});
            skArc(sketch, "E582.66", {"start": v(10.21, 8.45) * mm, "mid": v(10.14, 8.28) * mm, "end": v(9.96, 8.2) * mm});
            skLineSegment(sketch, "E582.73", {"start": v(15.65, 4.04) * mm, "end": v(17.94, 6.32) * mm});
            skArc(sketch, "E582.76", {"start": v(15.46, 8.2) * mm, "mid": v(15.29, 8.28) * mm, "end": v(15.21, 8.45) * mm});
            skArc(sketch, "E582.78", {"start": v(15.21, 9.5) * mm, "mid": v(15.36, 9.86) * mm, "end": v(15.71, 10) * mm});
            skArc(sketch, "E582.80", {"start": v(21.21, 10) * mm, "mid": v(22.27, 9.56) * mm, "end": v(22.71, 8.5) * mm});
            skLineSegment(sketch, "E582.81", {"start": v(22.71, 8.5) * mm, "end": v(22.71, 3) * mm});
            skArc(sketch, "E582.82", {"start": v(22.71, 3) * mm, "mid": v(22.57, 2.65) * mm, "end": v(22.21, 2.5) * mm});
            skArc(sketch, "E582.84", {"start": v(21.16, 2.5) * mm, "mid": v(20.99, 2.58) * mm, "end": v(20.91, 2.75) * mm});
            skLineSegment(sketch, "E582.89", {"start": v(16.31, 1.88) * mm, "end": v(16.31, -1.88) * mm});
            skLineSegment(sketch, "E582.92", {"start": v(16.75, -2.94) * mm, "end": v(19.04, -5.22) * mm});
            skArc(sketch, "E582.95", {"start": v(20.91, -2.75) * mm, "mid": v(20.99, -2.57) * mm, "end": v(21.16, -2.5) * mm});
            skLineSegment(sketch, "E582.96", {"start": v(21.16, -2.5) * mm, "end": v(22.21, -2.5) * mm});
            skArc(sketch, "E582.97", {"start": v(22.21, -2.5) * mm, "mid": v(22.57, -2.64) * mm, "end": v(22.71, -3) * mm});
            skLineSegment(sketch, "E582.108", {"start": v(14.6, -3.6) * mm, "end": v(10.84, -3.6) * mm});
            skLineSegment(sketch, "E582.116", {"start": v(-4.29, 10) * mm, "end": v(9.71, 10) * mm});
            skLineSegment(sketch, "E582.117", {"start": v(-3.25, 2.94) * mm, "end": v(1.57, 7.76) * mm});
            skLineSegment(sketch, "E582.118", {"start": v(3.85, 7.76) * mm, "end": v(8.67, 2.94) * mm});
            skLineSegment(sketch, "E583", {"start": v(-19.41, -10) * mm, "end": v(25.27, -10) * mm, "construction": true});
            skLineSegment(sketch, "E584", {"start": v(-15.79, 8.5) * mm, "end": v(6.66, -13.95) * mm, "construction": true});
            skArc(sketch, "E585.0.MirrorCS", {"start": v(-16.79, -17.5) * mm, "mid": v(-17.14, -17.35) * mm, "end": v(-17.29, -17) * mm});
            skLineSegment(sketch, "E586.0.MirrorCS", {"start": v(-15.74, -17.5) * mm, "end": v(-16.79, -17.5) * mm});
            skArc(sketch, "E587.0.MirrorCS", {"start": v(-15.49, -17.25) * mm, "mid": v(-15.56, -17.42) * mm, "end": v(-15.74, -17.5) * mm});
            skLineSegment(sketch, "E588.0.MirrorCS", {"start": v(-15.49, -17.25) * mm, "end": v(-15.49, -15.55) * mm});
            skArc(sketch, "E589.0.MirrorCS", {"start": v(-13.6, -14.78) * mm, "mid": v(-14.8, -14.54) * mm, "end": v(-15.49, -15.55) * mm});
            skLineSegment(sketch, "E590.0.MirrorCS", {"start": v(-11.33, -17.06) * mm, "end": v(-13.6, -14.78) * mm});
            skArc(sketch, "E591.0.MirrorCS", {"start": v(-10.89, -18.12) * mm, "mid": v(-11, -17.55) * mm, "end": v(-11.33, -17.06) * mm});
            skLineSegment(sketch, "E592.0.MirrorCS", {"start": v(-10.89, -21.88) * mm, "end": v(-10.89, -18.12) * mm});
            skArc(sketch, "E593.0.MirrorCS", {"start": v(-11.33, -22.94) * mm, "mid": v(-11, -22.45) * mm, "end": v(-10.89, -21.88) * mm});
            skLineSegment(sketch, "E594.0.MirrorCS", {"start": v(-13.6, -25.22) * mm, "end": v(-11.33, -22.94) * mm});
            skArc(sketch, "E595.0.MirrorCS", {"start": v(-15.49, -24.44) * mm, "mid": v(-14.8, -25.46) * mm, "end": v(-13.6, -25.22) * mm});
            skLineSegment(sketch, "E596.0.MirrorCS", {"start": v(-15.49, -22.75) * mm, "end": v(-15.49, -24.44) * mm});
            skArc(sketch, "E597.0.MirrorCS", {"start": v(-15.74, -22.5) * mm, "mid": v(-15.56, -22.57) * mm, "end": v(-15.49, -22.75) * mm});
            skLineSegment(sketch, "E598.0.MirrorCS", {"start": v(-16.79, -22.5) * mm, "end": v(-15.74, -22.5) * mm});
            skArc(sketch, "E599.0.MirrorCS", {"start": v(-17.29, -23) * mm, "mid": v(-17.14, -22.64) * mm, "end": v(-16.79, -22.5) * mm});
            skLineSegment(sketch, "E600.0.MirrorCS", {"start": v(-17.29, -28.5) * mm, "end": v(-17.29, -23) * mm});
            skArc(sketch, "E601.0.MirrorCS", {"start": v(-15.79, -30) * mm, "mid": v(-16.85, -29.56) * mm, "end": v(-17.29, -28.5) * mm});
            skLineSegment(sketch, "E602.0.MirrorCS", {"start": v(-15.79, -30) * mm, "end": v(-10.29, -30) * mm});
            skArc(sketch, "E603.0.MirrorCS", {"start": v(-9.79, -29.5) * mm, "mid": v(-9.93, -29.85) * mm, "end": v(-10.29, -30) * mm});
            skLineSegment(sketch, "E604.0.MirrorCS", {"start": v(-9.79, -29.5) * mm, "end": v(-9.79, -28.45) * mm});
            skArc(sketch, "E605.0.MirrorCS", {"start": v(-10.04, -28.2) * mm, "mid": v(-9.86, -28.27) * mm, "end": v(-9.79, -28.45) * mm});
            skLineSegment(sketch, "E606.0.MirrorCS", {"start": v(-10.04, -28.2) * mm, "end": v(-11.73, -28.2) * mm});
            skArc(sketch, "E607.0.MirrorCS", {"start": v(-11.73, -28.2) * mm, "mid": v(-12.75, -27.52) * mm, "end": v(-12.5, -26.32) * mm});
            skLineSegment(sketch, "E608.0.MirrorCS", {"start": v(-10.23, -24.04) * mm, "end": v(-12.5, -26.32) * mm});
            skArc(sketch, "E609.0.MirrorCS", {"start": v(-10.23, -24.04) * mm, "mid": v(-9.74, -23.71) * mm, "end": v(-9.16, -23.6) * mm});
            skLineSegment(sketch, "E610.0.MirrorCS", {"start": v(-5.4, -23.6) * mm, "end": v(-9.16, -23.6) * mm});
            skArc(sketch, "E611.0.MirrorCS", {"start": v(-4.35, -24.04) * mm, "mid": v(-4.83, -23.71) * mm, "end": v(-5.4, -23.6) * mm});
            skLineSegment(sketch, "E612.0.MirrorCS", {"start": v(-2.06, -26.32) * mm, "end": v(-4.35, -24.04) * mm});
            skArc(sketch, "E613.0.MirrorCS", {"start": v(-2.84, -28.2) * mm, "mid": v(-1.83, -27.52) * mm, "end": v(-2.06, -26.32) * mm});
            skLineSegment(sketch, "E614.0.MirrorCS", {"start": v(-2.84, -28.2) * mm, "end": v(-4.54, -28.2) * mm});
            skArc(sketch, "E615.0.MirrorCS", {"start": v(-4.79, -28.45) * mm, "mid": v(-4.71, -28.27) * mm, "end": v(-4.54, -28.2) * mm});
            skLineSegment(sketch, "E616.0.MirrorCS", {"start": v(-4.79, -29.5) * mm, "end": v(-4.79, -28.45) * mm});
            skArc(sketch, "E617.0.MirrorCS", {"start": v(-4.29, -30) * mm, "mid": v(-4.64, -29.85) * mm, "end": v(-4.79, -29.5) * mm});
            skLineSegment(sketch, "E618.0.MirrorCS", {"start": v(-4.29, -30) * mm, "end": v(9.71, -30) * mm});
            skArc(sketch, "E619.0.MirrorCS", {"start": v(9.71, -30) * mm, "mid": v(10.07, -29.85) * mm, "end": v(10.21, -29.5) * mm});
            skLineSegment(sketch, "E620.0.MirrorCS", {"start": v(10.21, -28.45) * mm, "end": v(10.21, -29.5) * mm});
            skArc(sketch, "E621.0.MirrorCS", {"start": v(9.96, -28.2) * mm, "mid": v(10.14, -28.27) * mm, "end": v(10.21, -28.45) * mm});
            skLineSegment(sketch, "E622.0.MirrorCS", {"start": v(8.27, -28.2) * mm, "end": v(9.96, -28.2) * mm});
            skArc(sketch, "E623.0.MirrorCS", {"start": v(7.5, -26.32) * mm, "mid": v(7.25, -27.52) * mm, "end": v(8.27, -28.2) * mm});
            skLineSegment(sketch, "E624.0.MirrorCS", {"start": v(9.77, -24.04) * mm, "end": v(7.5, -26.32) * mm});
            skArc(sketch, "E625.0.MirrorCS", {"start": v(10.84, -23.6) * mm, "mid": v(10.26, -23.71) * mm, "end": v(9.77, -24.04) * mm});
            skLineSegment(sketch, "E626.0.MirrorCS", {"start": v(14.6, -23.6) * mm, "end": v(10.84, -23.6) * mm});
            skArc(sketch, "E627.0.MirrorCS", {"start": v(15.65, -24.04) * mm, "mid": v(15.17, -23.71) * mm, "end": v(14.6, -23.6) * mm});
            skLineSegment(sketch, "E628.0.MirrorCS", {"start": v(17.94, -26.32) * mm, "end": v(15.65, -24.04) * mm});
            skArc(sketch, "E629.0.MirrorCS", {"start": v(17.16, -28.2) * mm, "mid": v(18.17, -27.52) * mm, "end": v(17.94, -26.32) * mm});
            skLineSegment(sketch, "E630.0.MirrorCS", {"start": v(15.46, -28.2) * mm, "end": v(17.16, -28.2) * mm});
            skArc(sketch, "E631.0.MirrorCS", {"start": v(15.46, -28.2) * mm, "mid": v(15.29, -28.27) * mm, "end": v(15.21, -28.45) * mm});
            skLineSegment(sketch, "E632.0.MirrorCS", {"start": v(15.21, -29.5) * mm, "end": v(15.21, -28.45) * mm});
            skArc(sketch, "E633.0.MirrorCS", {"start": v(15.71, -30) * mm, "mid": v(15.36, -29.85) * mm, "end": v(15.21, -29.5) * mm});
            skLineSegment(sketch, "E634.0.MirrorCS", {"start": v(21.21, -30) * mm, "end": v(15.71, -30) * mm});
            skArc(sketch, "E635.0.MirrorCS", {"start": v(21.21, -30) * mm, "mid": v(22.27, -29.56) * mm, "end": v(22.71, -28.5) * mm});
            skLineSegment(sketch, "E636.0.MirrorCS", {"start": v(22.71, -23) * mm, "end": v(22.71, -28.5) * mm});
            skArc(sketch, "E637.0.MirrorCS", {"start": v(22.21, -22.5) * mm, "mid": v(22.57, -22.64) * mm, "end": v(22.71, -23) * mm});
            skLineSegment(sketch, "E638.0.MirrorCS", {"start": v(21.16, -22.5) * mm, "end": v(22.21, -22.5) * mm});
            skArc(sketch, "E639.0.MirrorCS", {"start": v(21.16, -22.5) * mm, "mid": v(20.99, -22.57) * mm, "end": v(20.91, -22.75) * mm});
            skLineSegment(sketch, "E640.0.MirrorCS", {"start": v(20.91, -24.44) * mm, "end": v(20.91, -22.75) * mm});
            skArc(sketch, "E641.0.MirrorCS", {"start": v(19.04, -25.22) * mm, "mid": v(20.23, -25.46) * mm, "end": v(20.91, -24.44) * mm});
            skLineSegment(sketch, "E642.0.MirrorCS", {"start": v(16.75, -22.94) * mm, "end": v(19.04, -25.22) * mm});
            skArc(sketch, "E643.0.MirrorCS", {"start": v(16.31, -21.88) * mm, "mid": v(16.43, -22.45) * mm, "end": v(16.75, -22.94) * mm});
            skLineSegment(sketch, "E644.0.MirrorCS", {"start": v(16.31, -18.12) * mm, "end": v(16.31, -21.88) * mm});
            skArc(sketch, "E645.0.MirrorCS", {"start": v(16.75, -17.06) * mm, "mid": v(16.43, -17.55) * mm, "end": v(16.31, -18.12) * mm});
            skLineSegment(sketch, "E646.0.MirrorCS", {"start": v(16.75, -17.06) * mm, "end": v(19.04, -14.78) * mm});
            skArc(sketch, "E647.0.MirrorCS", {"start": v(20.91, -15.55) * mm, "mid": v(20.23, -14.54) * mm, "end": v(19.04, -14.78) * mm});
            skLineSegment(sketch, "E648.0.MirrorCS", {"start": v(20.91, -17.25) * mm, "end": v(20.91, -15.55) * mm});
            skArc(sketch, "E649.0.MirrorCS", {"start": v(20.91, -17.25) * mm, "mid": v(20.99, -17.42) * mm, "end": v(21.16, -17.5) * mm});
            skLineSegment(sketch, "E650.0.MirrorCS", {"start": v(21.16, -17.5) * mm, "end": v(22.21, -17.5) * mm});
            skArc(sketch, "E651.0.MirrorCS", {"start": v(22.71, -17) * mm, "mid": v(22.57, -17.35) * mm, "end": v(22.21, -17.5) * mm});
            skCircle(sketch, "E652.0.MirrorC", {"center": v(12.71, -20) * mm, "radius": 2.15 * mm});
            skCircle(sketch, "E653.0.MirrorC", {"center": v(-7.29, -20) * mm, "radius": 2.15 * mm});
            skArc(sketch, "E654.0.MirrorCS", {"start": v(-3.25, -22.94) * mm, "mid": v(-3.57, -22.45) * mm, "end": v(-3.69, -21.88) * mm});
            skLineSegment(sketch, "E655.0.MirrorCS", {"start": v(-3.25, -22.94) * mm, "end": v(1.57, -27.76) * mm});
            skArc(sketch, "E656.0.MirrorCS", {"start": v(2.64, -28.2) * mm, "mid": v(2.06, -28.08) * mm, "end": v(1.57, -27.76) * mm});
            skLineSegment(sketch, "E657.0.MirrorCS", {"start": v(2.8, -28.2) * mm, "end": v(2.64, -28.2) * mm});
            skArc(sketch, "E658.0.MirrorCS", {"start": v(3.85, -27.76) * mm, "mid": v(3.37, -28.08) * mm, "end": v(2.8, -28.2) * mm});
            skLineSegment(sketch, "E659.0.MirrorCS", {"start": v(3.85, -27.76) * mm, "end": v(8.67, -22.94) * mm});
            skArc(sketch, "E660.0.MirrorCS", {"start": v(9.11, -21.88) * mm, "mid": v(9, -22.45) * mm, "end": v(8.67, -22.94) * mm});
            skArc(sketch, "E661.0.MirrorCS", {"start": v(14.6, -16.4) * mm, "mid": v(15.17, -16.28) * mm, "end": v(15.65, -15.96) * mm});
            skLineSegment(sketch, "E662.0.MirrorCS", {"start": v(14.6, -16.4) * mm, "end": v(10.84, -16.4) * mm});
            skLineSegment(sketch, "E663.0.MirrorCS", {"start": v(9.11, -21.88) * mm, "end": v(9.11, -18.12) * mm});
            skLineSegment(sketch, "E664.0.MirrorCS", {"start": v(-3.69, -21.88) * mm, "end": v(-3.69, -18.12) * mm});
            skLineSegment(sketch, "E665.0.MirrorCS", {"start": v(-9.16, -16.4) * mm, "end": v(-5.4, -16.4) * mm});
            skArc(sketch, "E666.0.MirrorCS", {"start": v(-9.16, -16.4) * mm, "mid": v(-9.74, -16.28) * mm, "end": v(-10.23, -15.96) * mm});
            skLineSegment(sketch, "E667.0.MirrorCS", {"start": v(-15.05, -8.86) * mm, "end": v(-10.23, -4.04) * mm});
            skArc(sketch, "E668.0.MirrorCS", {"start": v(-15.49, -9.92) * mm, "mid": v(-15.37, -9.35) * mm, "end": v(-15.05, -8.86) * mm});
            skLineSegment(sketch, "E669.0.MirrorCS", {"start": v(-15.49, -10.08) * mm, "end": v(-15.49, -9.92) * mm});
            skArc(sketch, "E670.0.MirrorCS", {"start": v(-15.05, -11.14) * mm, "mid": v(-15.37, -10.65) * mm, "end": v(-15.49, -10.08) * mm});
            skLineSegment(sketch, "E671.0.MirrorCS", {"start": v(-15.05, -11.14) * mm, "end": v(-10.23, -15.96) * mm});
            skLineSegment(sketch, "E672", {"start": v(2.71, -10) * mm, "end": v(21.21, 8.5) * mm, "construction": true});
            skLineSegment(sketch, "E673.0.MirrorCS", {"start": v(20.47, -8.86) * mm, "end": v(15.65, -4.04) * mm});
            skArc(sketch, "E674.0.MirrorCS", {"start": v(20.47, -8.86) * mm, "mid": v(20.8, -9.35) * mm, "end": v(20.91, -9.92) * mm});
            skLineSegment(sketch, "E675.0.MirrorCS", {"start": v(20.91, -9.92) * mm, "end": v(20.91, -10.08) * mm});
            skArc(sketch, "E676.0.MirrorCS", {"start": v(20.91, -10.08) * mm, "mid": v(20.8, -10.65) * mm, "end": v(20.47, -11.14) * mm});
            skLineSegment(sketch, "E677.0.MirrorCS", {"start": v(20.47, -11.14) * mm, "end": v(15.65, -15.96) * mm});
            skLineSegment(sketch, "E678", {"start": v(-5.4, -3.6) * mm, "end": v(-3.69, -1.88) * mm});
            skLineSegment(sketch, "E679", {"start": v(9.11, -1.88) * mm, "end": v(10.84, -3.6) * mm});
            skLineSegment(sketch, "E680", {"start": v(-3.69, -18.12) * mm, "end": v(-5.4, -16.4) * mm});
            skLineSegment(sketch, "E681", {"start": v(10.84, -16.4) * mm, "end": v(9.11, -18.12) * mm});
            skLineSegment(sketch, "E682", {"start": v(-17.29, -3) * mm, "end": v(-17.29, -17) * mm});
            skLineSegment(sketch, "E683", {"start": v(22.71, -3) * mm, "end": v(22.71, -17) * mm});
            skSolve(sketch);
        }
        {
            var Q0;
            Q0=qCreatedBy(makeId("Front.planeOp"),FACE);
            var sketch = newSketch(context, id + "F7", { "sketchPlane" : qUnion([Q0])});
            skLineSegment(sketch, "E684.0.0", {"start": v(-10.29, 10) * mm, "end": v(-15.79, 10) * mm});
            skArc(sketch, "E684.0.1", {"start": v(-15.79, 10) * mm, "mid": v(-16.85, 9.56) * mm, "end": v(-17.29, 8.5) * mm});
            skLineSegment(sketch, "E684.0.2", {"start": v(-17.29, 8.5) * mm, "end": v(-17.29, 3) * mm});
            skArc(sketch, "E684.0.3", {"start": v(-17.29, 3) * mm, "mid": v(-17.14, 2.65) * mm, "end": v(-16.79, 2.5) * mm});
            skLineSegment(sketch, "E684.0.4", {"start": v(-16.79, 2.5) * mm, "end": v(-15.74, 2.5) * mm});
            skArc(sketch, "E684.0.5", {"start": v(-15.74, 2.5) * mm, "mid": v(-15.56, 2.58) * mm, "end": v(-15.49, 2.75) * mm});
            skLineSegment(sketch, "E684.0.6", {"start": v(-15.49, 2.75) * mm, "end": v(-15.49, 4.45) * mm});
            skArc(sketch, "E684.0.7", {"start": v(-15.49, 4.45) * mm, "mid": v(-14.8, 5.46) * mm, "end": v(-13.6, 5.22) * mm});
            skLineSegment(sketch, "E684.0.8", {"start": v(-13.6, 5.22) * mm, "end": v(-11.33, 2.94) * mm});
            skArc(sketch, "E684.0.9", {"start": v(-11.33, 2.94) * mm, "mid": v(-11, 2.45) * mm, "end": v(-10.89, 1.88) * mm});
            skLineSegment(sketch, "E684.0.10", {"start": v(-10.89, 1.88) * mm, "end": v(-10.89, -1.88) * mm});
            skArc(sketch, "E684.0.11", {"start": v(-10.89, -1.88) * mm, "mid": v(-11, -2.45) * mm, "end": v(-11.33, -2.94) * mm});
            skLineSegment(sketch, "E684.0.12", {"start": v(-11.33, -2.94) * mm, "end": v(-13.6, -5.22) * mm});
            skArc(sketch, "E684.0.13", {"start": v(-13.6, -5.22) * mm, "mid": v(-14.8, -5.46) * mm, "end": v(-15.49, -4.44) * mm});
            skLineSegment(sketch, "E684.0.14", {"start": v(-15.49, -4.44) * mm, "end": v(-15.49, -2.75) * mm});
            skArc(sketch, "E684.0.15", {"start": v(-15.49, -2.75) * mm, "mid": v(-15.56, -2.57) * mm, "end": v(-15.74, -2.5) * mm});
            skLineSegment(sketch, "E684.0.16", {"start": v(-15.74, -2.5) * mm, "end": v(-16.79, -2.5) * mm});
            skArc(sketch, "E684.0.17", {"start": v(-16.79, -2.5) * mm, "mid": v(-17.14, -2.64) * mm, "end": v(-17.29, -3) * mm});
            skLineSegment(sketch, "E684.0.18", {"start": v(-17.29, -3) * mm, "end": v(-17.29, -17) * mm});
            skArc(sketch, "E684.0.19", {"start": v(-17.29, -17) * mm, "mid": v(-17.14, -17.35) * mm, "end": v(-16.79, -17.5) * mm});
            skLineSegment(sketch, "E684.0.20", {"start": v(-16.79, -17.5) * mm, "end": v(-15.74, -17.5) * mm});
            skArc(sketch, "E684.0.21", {"start": v(-15.74, -17.5) * mm, "mid": v(-15.56, -17.42) * mm, "end": v(-15.49, -17.25) * mm});
            skLineSegment(sketch, "E684.0.22", {"start": v(-15.49, -17.25) * mm, "end": v(-15.49, -15.55) * mm});
            skArc(sketch, "E684.0.23", {"start": v(-15.49, -15.55) * mm, "mid": v(-14.8, -14.54) * mm, "end": v(-13.6, -14.78) * mm});
            skLineSegment(sketch, "E684.0.24", {"start": v(-13.6, -14.78) * mm, "end": v(-11.33, -17.06) * mm});
            skArc(sketch, "E684.0.25", {"start": v(-11.33, -17.06) * mm, "mid": v(-11, -17.55) * mm, "end": v(-10.89, -18.12) * mm});
            skLineSegment(sketch, "E684.0.26", {"start": v(-10.89, -18.12) * mm, "end": v(-10.89, -21.88) * mm});
            skArc(sketch, "E684.0.27", {"start": v(-10.89, -21.88) * mm, "mid": v(-11, -22.45) * mm, "end": v(-11.33, -22.94) * mm});
            skLineSegment(sketch, "E684.0.28", {"start": v(-11.33, -22.94) * mm, "end": v(-13.6, -25.22) * mm});
            skArc(sketch, "E684.0.29", {"start": v(-13.6, -25.22) * mm, "mid": v(-14.8, -25.46) * mm, "end": v(-15.49, -24.44) * mm});
            skLineSegment(sketch, "E684.0.30", {"start": v(-15.49, -24.44) * mm, "end": v(-15.49, -22.75) * mm});
            skArc(sketch, "E684.0.31", {"start": v(-15.49, -22.75) * mm, "mid": v(-15.56, -22.57) * mm, "end": v(-15.74, -22.5) * mm});
            skLineSegment(sketch, "E684.0.32", {"start": v(-15.74, -22.5) * mm, "end": v(-16.79, -22.5) * mm});
            skArc(sketch, "E684.0.33", {"start": v(-16.79, -22.5) * mm, "mid": v(-17.14, -22.64) * mm, "end": v(-17.29, -23) * mm});
            skLineSegment(sketch, "E684.0.34", {"start": v(-17.29, -23) * mm, "end": v(-17.29, -28.5) * mm});
            skArc(sketch, "E684.0.35", {"start": v(-17.29, -28.5) * mm, "mid": v(-16.85, -29.56) * mm, "end": v(-15.79, -30) * mm});
            skLineSegment(sketch, "E684.0.36", {"start": v(-15.79, -30) * mm, "end": v(-10.29, -30) * mm});
            skArc(sketch, "E684.0.37", {"start": v(-10.29, -30) * mm, "mid": v(-9.93, -29.85) * mm, "end": v(-9.79, -29.5) * mm});
            skLineSegment(sketch, "E684.0.38", {"start": v(-9.79, -29.5) * mm, "end": v(-9.79, -28.45) * mm});
            skArc(sketch, "E684.0.39", {"start": v(-9.79, -28.45) * mm, "mid": v(-9.86, -28.27) * mm, "end": v(-10.04, -28.2) * mm});
            skLineSegment(sketch, "E684.0.40", {"start": v(-10.04, -28.2) * mm, "end": v(-11.73, -28.2) * mm});
            skArc(sketch, "E684.0.41", {"start": v(-11.73, -28.2) * mm, "mid": v(-12.75, -27.52) * mm, "end": v(-12.5, -26.32) * mm});
            skLineSegment(sketch, "E684.0.42", {"start": v(-12.5, -26.32) * mm, "end": v(-10.23, -24.04) * mm});
            skArc(sketch, "E684.0.43", {"start": v(-10.23, -24.04) * mm, "mid": v(-9.74, -23.71) * mm, "end": v(-9.16, -23.6) * mm});
            skLineSegment(sketch, "E684.0.44", {"start": v(-9.16, -23.6) * mm, "end": v(-5.4, -23.6) * mm});
            skArc(sketch, "E684.0.45", {"start": v(-5.4, -23.6) * mm, "mid": v(-4.83, -23.71) * mm, "end": v(-4.35, -24.04) * mm});
            skLineSegment(sketch, "E684.0.46", {"start": v(-4.35, -24.04) * mm, "end": v(-2.06, -26.32) * mm});
            skArc(sketch, "E684.0.47", {"start": v(-2.06, -26.32) * mm, "mid": v(-1.83, -27.52) * mm, "end": v(-2.84, -28.2) * mm});
            skLineSegment(sketch, "E684.0.48", {"start": v(-2.84, -28.2) * mm, "end": v(-4.54, -28.2) * mm});
            skArc(sketch, "E684.0.49", {"start": v(-4.54, -28.2) * mm, "mid": v(-4.71, -28.27) * mm, "end": v(-4.79, -28.45) * mm});
            skLineSegment(sketch, "E684.0.50", {"start": v(-4.79, -28.45) * mm, "end": v(-4.79, -29.5) * mm});
            skArc(sketch, "E684.0.51", {"start": v(-4.79, -29.5) * mm, "mid": v(-4.64, -29.85) * mm, "end": v(-4.29, -30) * mm});
            skLineSegment(sketch, "E684.0.52", {"start": v(-4.29, -30) * mm, "end": v(9.71, -30) * mm});
            skArc(sketch, "E684.0.53", {"start": v(9.71, -30) * mm, "mid": v(10.07, -29.85) * mm, "end": v(10.21, -29.5) * mm});
            skLineSegment(sketch, "E684.0.54", {"start": v(10.21, -29.5) * mm, "end": v(10.21, -28.45) * mm});
            skArc(sketch, "E684.0.55", {"start": v(10.21, -28.45) * mm, "mid": v(10.14, -28.27) * mm, "end": v(9.96, -28.2) * mm});
            skLineSegment(sketch, "E684.0.56", {"start": v(9.96, -28.2) * mm, "end": v(8.27, -28.2) * mm});
            skArc(sketch, "E684.0.57", {"start": v(8.27, -28.2) * mm, "mid": v(7.25, -27.52) * mm, "end": v(7.5, -26.32) * mm});
            skLineSegment(sketch, "E684.0.58", {"start": v(7.5, -26.32) * mm, "end": v(9.77, -24.04) * mm});
            skArc(sketch, "E684.0.59", {"start": v(9.77, -24.04) * mm, "mid": v(10.26, -23.71) * mm, "end": v(10.84, -23.6) * mm});
            skLineSegment(sketch, "E684.0.60", {"start": v(10.84, -23.6) * mm, "end": v(14.6, -23.6) * mm});
            skArc(sketch, "E684.0.61", {"start": v(14.6, -23.6) * mm, "mid": v(15.17, -23.71) * mm, "end": v(15.65, -24.04) * mm});
            skLineSegment(sketch, "E684.0.62", {"start": v(15.65, -24.04) * mm, "end": v(17.94, -26.32) * mm});
            skArc(sketch, "E684.0.63", {"start": v(17.94, -26.32) * mm, "mid": v(18.17, -27.52) * mm, "end": v(17.16, -28.2) * mm});
            skLineSegment(sketch, "E684.0.64", {"start": v(17.16, -28.2) * mm, "end": v(15.46, -28.2) * mm});
            skArc(sketch, "E684.0.65", {"start": v(15.46, -28.2) * mm, "mid": v(15.29, -28.27) * mm, "end": v(15.21, -28.45) * mm});
            skLineSegment(sketch, "E684.0.66", {"start": v(15.21, -28.45) * mm, "end": v(15.21, -29.5) * mm});
            skArc(sketch, "E684.0.67", {"start": v(15.21, -29.5) * mm, "mid": v(15.36, -29.85) * mm, "end": v(15.71, -30) * mm});
            skArc(sketch, "E684.0.77", {"start": v(16.75, -22.94) * mm, "mid": v(16.43, -22.45) * mm, "end": v(16.31, -21.88) * mm});
            skLineSegment(sketch, "E684.0.78", {"start": v(16.31, -21.88) * mm, "end": v(16.31, -18.12) * mm});
            skArc(sketch, "E684.0.79", {"start": v(16.31, -18.12) * mm, "mid": v(16.43, -17.55) * mm, "end": v(16.75, -17.06) * mm});
            skArc(sketch, "E684.0.93", {"start": v(16.75, -2.94) * mm, "mid": v(16.43, -2.45) * mm, "end": v(16.31, -1.88) * mm});
            skLineSegment(sketch, "E684.0.94", {"start": v(16.31, -1.88) * mm, "end": v(16.31, 1.88) * mm});
            skArc(sketch, "E684.0.95", {"start": v(16.31, 1.88) * mm, "mid": v(16.43, 2.45) * mm, "end": v(16.75, 2.94) * mm});
            skArc(sketch, "E684.0.105", {"start": v(15.71, 10) * mm, "mid": v(15.36, 9.86) * mm, "end": v(15.21, 9.5) * mm});
            skLineSegment(sketch, "E684.0.106", {"start": v(15.21, 9.5) * mm, "end": v(15.21, 8.45) * mm});
            skArc(sketch, "E684.0.107", {"start": v(15.21, 8.45) * mm, "mid": v(15.29, 8.28) * mm, "end": v(15.46, 8.2) * mm});
            skLineSegment(sketch, "E684.0.108", {"start": v(15.46, 8.2) * mm, "end": v(17.16, 8.2) * mm});
            skArc(sketch, "E684.0.109", {"start": v(17.16, 8.2) * mm, "mid": v(18.17, 7.52) * mm, "end": v(17.94, 6.32) * mm});
            skLineSegment(sketch, "E684.0.110", {"start": v(17.94, 6.32) * mm, "end": v(15.65, 4.04) * mm});
            skArc(sketch, "E684.0.111", {"start": v(15.65, 4.04) * mm, "mid": v(15.17, 3.72) * mm, "end": v(14.6, 3.6) * mm});
            skLineSegment(sketch, "E684.0.112", {"start": v(14.6, 3.6) * mm, "end": v(10.84, 3.6) * mm});
            skArc(sketch, "E684.0.113", {"start": v(10.84, 3.6) * mm, "mid": v(10.26, 3.72) * mm, "end": v(9.77, 4.04) * mm});
            skLineSegment(sketch, "E684.0.114", {"start": v(9.77, 4.04) * mm, "end": v(7.5, 6.32) * mm});
            skArc(sketch, "E684.0.115", {"start": v(7.5, 6.32) * mm, "mid": v(7.25, 7.52) * mm, "end": v(8.27, 8.2) * mm});
            skLineSegment(sketch, "E684.0.116", {"start": v(8.27, 8.2) * mm, "end": v(9.96, 8.2) * mm});
            skArc(sketch, "E684.0.117", {"start": v(9.96, 8.2) * mm, "mid": v(10.14, 8.28) * mm, "end": v(10.21, 8.45) * mm});
            skLineSegment(sketch, "E684.0.118", {"start": v(10.21, 8.45) * mm, "end": v(10.21, 9.5) * mm});
            skArc(sketch, "E684.0.119", {"start": v(10.21, 9.5) * mm, "mid": v(10.07, 9.86) * mm, "end": v(9.71, 10) * mm});
            skLineSegment(sketch, "E684.0.120", {"start": v(9.71, 10) * mm, "end": v(-4.29, 10) * mm});
            skArc(sketch, "E684.0.121", {"start": v(-4.29, 10) * mm, "mid": v(-4.64, 9.86) * mm, "end": v(-4.79, 9.5) * mm});
            skLineSegment(sketch, "E684.0.122", {"start": v(-4.79, 9.5) * mm, "end": v(-4.79, 8.45) * mm});
            skArc(sketch, "E684.0.123", {"start": v(-4.79, 8.45) * mm, "mid": v(-4.71, 8.28) * mm, "end": v(-4.54, 8.2) * mm});
            skLineSegment(sketch, "E684.0.124", {"start": v(-4.54, 8.2) * mm, "end": v(-2.84, 8.2) * mm});
            skArc(sketch, "E684.0.125", {"start": v(-2.84, 8.2) * mm, "mid": v(-1.83, 7.52) * mm, "end": v(-2.06, 6.32) * mm});
            skLineSegment(sketch, "E684.0.126", {"start": v(-2.06, 6.32) * mm, "end": v(-4.35, 4.04) * mm});
            skArc(sketch, "E684.0.127", {"start": v(-4.35, 4.04) * mm, "mid": v(-4.83, 3.72) * mm, "end": v(-5.4, 3.6) * mm});
            skLineSegment(sketch, "E684.0.128", {"start": v(-5.4, 3.6) * mm, "end": v(-9.16, 3.6) * mm});
            skArc(sketch, "E684.0.129", {"start": v(-9.16, 3.6) * mm, "mid": v(-9.74, 3.72) * mm, "end": v(-10.23, 4.04) * mm});
            skLineSegment(sketch, "E684.0.130", {"start": v(-10.23, 4.04) * mm, "end": v(-12.5, 6.32) * mm});
            skArc(sketch, "E684.0.131", {"start": v(-12.5, 6.32) * mm, "mid": v(-12.75, 7.52) * mm, "end": v(-11.73, 8.2) * mm});
            skLineSegment(sketch, "E684.0.132", {"start": v(-11.73, 8.2) * mm, "end": v(-10.04, 8.2) * mm});
            skArc(sketch, "E684.0.133", {"start": v(-10.04, 8.2) * mm, "mid": v(-9.86, 8.28) * mm, "end": v(-9.79, 8.45) * mm});
            skLineSegment(sketch, "E684.0.134", {"start": v(-9.79, 8.45) * mm, "end": v(-9.79, 9.5) * mm});
            skArc(sketch, "E684.0.135", {"start": v(-9.79, 9.5) * mm, "mid": v(-9.93, 9.86) * mm, "end": v(-10.29, 10) * mm});
            skLineSegment(sketch, "E685.0.0", {"start": v(-5.4, -3.6) * mm, "end": v(-9.16, -3.6) * mm});
            skArc(sketch, "E685.0.1", {"start": v(-9.16, -3.6) * mm, "mid": v(-9.74, -3.71) * mm, "end": v(-10.23, -4.04) * mm});
            skLineSegment(sketch, "E685.0.2", {"start": v(-10.23, -4.04) * mm, "end": v(-15.05, -8.86) * mm});
            skArc(sketch, "E685.0.3", {"start": v(-15.05, -8.86) * mm, "mid": v(-15.37, -9.35) * mm, "end": v(-15.49, -9.92) * mm});
            skLineSegment(sketch, "E685.0.4", {"start": v(-15.49, -9.92) * mm, "end": v(-15.49, -10.08) * mm});
            skArc(sketch, "E685.0.5", {"start": v(-15.49, -10.08) * mm, "mid": v(-15.37, -10.65) * mm, "end": v(-15.05, -11.14) * mm});
            skLineSegment(sketch, "E685.0.6", {"start": v(-15.05, -11.14) * mm, "end": v(-10.23, -15.96) * mm});
            skArc(sketch, "E685.0.7", {"start": v(-10.23, -15.96) * mm, "mid": v(-9.74, -16.28) * mm, "end": v(-9.16, -16.4) * mm});
            skLineSegment(sketch, "E685.0.8", {"start": v(-9.16, -16.4) * mm, "end": v(-5.4, -16.4) * mm});
            skLineSegment(sketch, "E685.0.9", {"start": v(-5.4, -16.4) * mm, "end": v(-3.69, -18.12) * mm});
            skLineSegment(sketch, "E685.0.10", {"start": v(-3.69, -18.12) * mm, "end": v(-3.69, -21.88) * mm});
            skArc(sketch, "E685.0.11", {"start": v(-3.69, -21.88) * mm, "mid": v(-3.57, -22.45) * mm, "end": v(-3.25, -22.94) * mm});
            skLineSegment(sketch, "E685.0.12", {"start": v(-3.25, -22.94) * mm, "end": v(1.57, -27.76) * mm});
            skArc(sketch, "E685.0.13", {"start": v(1.57, -27.76) * mm, "mid": v(2.06, -28.08) * mm, "end": v(2.64, -28.2) * mm});
            skLineSegment(sketch, "E685.0.14", {"start": v(2.64, -28.2) * mm, "end": v(2.8, -28.2) * mm});
            skArc(sketch, "E685.0.15", {"start": v(2.8, -28.2) * mm, "mid": v(3.37, -28.08) * mm, "end": v(3.85, -27.76) * mm});
            skLineSegment(sketch, "E685.0.16", {"start": v(3.85, -27.76) * mm, "end": v(8.67, -22.94) * mm});
            skArc(sketch, "E685.0.17", {"start": v(8.67, -22.94) * mm, "mid": v(9, -22.45) * mm, "end": v(9.11, -21.88) * mm});
            skLineSegment(sketch, "E685.0.18", {"start": v(9.11, -21.88) * mm, "end": v(9.11, -18.12) * mm});
            skLineSegment(sketch, "E685.0.19", {"start": v(9.11, -18.12) * mm, "end": v(10.84, -16.4) * mm});
            skLineSegment(sketch, "E685.0.20", {"start": v(10.84, -16.4) * mm, "end": v(14.6, -16.4) * mm});
            skArc(sketch, "E685.0.21", {"start": v(14.6, -16.4) * mm, "mid": v(15.17, -16.28) * mm, "end": v(15.65, -15.96) * mm});
            skLineSegment(sketch, "E685.0.22", {"start": v(15.65, -15.96) * mm, "end": v(20.47, -11.14) * mm});
            skArc(sketch, "E685.0.23", {"start": v(20.47, -11.14) * mm, "mid": v(20.8, -10.65) * mm, "end": v(20.91, -10.08) * mm});
            skLineSegment(sketch, "E685.0.24", {"start": v(20.91, -10.08) * mm, "end": v(20.91, -9.92) * mm});
            skArc(sketch, "E685.0.25", {"start": v(20.91, -9.92) * mm, "mid": v(20.8, -9.35) * mm, "end": v(20.47, -8.86) * mm});
            skLineSegment(sketch, "E685.0.26", {"start": v(20.47, -8.86) * mm, "end": v(15.65, -4.04) * mm});
            skArc(sketch, "E685.0.27", {"start": v(15.65, -4.04) * mm, "mid": v(15.17, -3.71) * mm, "end": v(14.6, -3.6) * mm});
            skLineSegment(sketch, "E685.0.28", {"start": v(14.6, -3.6) * mm, "end": v(10.84, -3.6) * mm});
            skLineSegment(sketch, "E685.0.29", {"start": v(10.84, -3.6) * mm, "end": v(9.11, -1.88) * mm});
            skLineSegment(sketch, "E685.0.30", {"start": v(9.11, -1.88) * mm, "end": v(9.11, 1.88) * mm});
            skArc(sketch, "E685.0.31", {"start": v(9.11, 1.88) * mm, "mid": v(9, 2.45) * mm, "end": v(8.67, 2.94) * mm});
            skLineSegment(sketch, "E685.0.32", {"start": v(8.67, 2.94) * mm, "end": v(3.85, 7.76) * mm});
            skArc(sketch, "E685.0.33", {"start": v(3.85, 7.76) * mm, "mid": v(3.37, 8.09) * mm, "end": v(2.8, 8.2) * mm});
            skLineSegment(sketch, "E685.0.34", {"start": v(2.8, 8.2) * mm, "end": v(2.64, 8.2) * mm});
            skArc(sketch, "E685.0.35", {"start": v(2.64, 8.2) * mm, "mid": v(2.06, 8.09) * mm, "end": v(1.57, 7.76) * mm});
            skLineSegment(sketch, "E685.0.36", {"start": v(1.57, 7.76) * mm, "end": v(-3.25, 2.94) * mm});
            skArc(sketch, "E685.0.37", {"start": v(-3.25, 2.94) * mm, "mid": v(-3.57, 2.45) * mm, "end": v(-3.69, 1.88) * mm});
            skLineSegment(sketch, "E685.0.38", {"start": v(-3.69, 1.88) * mm, "end": v(-3.69, -1.88) * mm});
            skLineSegment(sketch, "E685.0.39", {"start": v(-3.69, -1.88) * mm, "end": v(-5.4, -3.6) * mm});
            skCircle(sketch, "E686.0", {"center": v(-7.29, 0) * mm, "radius": 2.15 * mm});
            skCircle(sketch, "E687.0", {"center": v(12.71, 0) * mm, "radius": 2.15 * mm});
            skCircle(sketch, "E688.0", {"center": v(12.71, -20) * mm, "radius": 2.15 * mm});
            skCircle(sketch, "E689.0", {"center": v(-7.29, -20) * mm, "radius": 2.15 * mm});
            skLineSegment(sketch, "E690.0", {"start": v(-19.41, -10) * mm, "end": v(25.27, -10) * mm, "construction": true});
            skLineSegment(sketch, "E691.0", {"start": v(-15.79, 8.5) * mm, "end": v(6.66, -13.95) * mm, "construction": true});
            skLineSegment(sketch, "E692.0", {"start": v(2.71, -10) * mm, "end": v(21.21, 8.5) * mm, "construction": true});
            skLineSegment(sketch, "E693", {"start": v(12.71, 12.48) * mm, "end": v(12.71, -32.12) * mm, "construction": true});
            skLineSegment(sketch, "E694.0.MirrorCS", {"start": v(16.75, 2.94) * mm, "end": v(21.57, 7.76) * mm});
            skLineSegment(sketch, "E695.0.MirrorCS", {"start": v(15.71, 10) * mm, "end": v(29.71, 10) * mm});
            skLineSegment(sketch, "E696.0.MirrorCS", {"start": v(21.57, -27.76) * mm, "end": v(16.75, -22.94) * mm});
            skLineSegment(sketch, "E697.0.MirrorCS", {"start": v(29.71, -30) * mm, "end": v(15.71, -30) * mm});
            skArc(sketch, "E698.0.MirrorCS", {"start": v(29.71, 10) * mm, "mid": v(30.07, 9.86) * mm, "end": v(30.21, 9.5) * mm});
            skLineSegment(sketch, "E699.0.MirrorCS", {"start": v(30.21, 9.5) * mm, "end": v(30.21, 8.45) * mm});
            skArc(sketch, "E700.0.MirrorCS", {"start": v(30.21, 8.45) * mm, "mid": v(30.14, 8.28) * mm, "end": v(29.96, 8.2) * mm});
            skLineSegment(sketch, "E701.0.MirrorCS", {"start": v(29.96, 8.2) * mm, "end": v(28.27, 8.2) * mm});
            skArc(sketch, "E702.0.MirrorCS", {"start": v(28.27, 8.2) * mm, "mid": v(27.25, 7.52) * mm, "end": v(27.5, 6.32) * mm});
            skLineSegment(sketch, "E703.0.MirrorCS", {"start": v(27.5, 6.32) * mm, "end": v(29.77, 4.04) * mm});
            skArc(sketch, "E704.0.MirrorCS", {"start": v(29.77, 4.04) * mm, "mid": v(30.26, 3.72) * mm, "end": v(30.84, 3.6) * mm});
            skLineSegment(sketch, "E705.0.MirrorCS", {"start": v(30.84, 3.6) * mm, "end": v(34.6, 3.6) * mm});
            skArc(sketch, "E706.0.MirrorCS", {"start": v(34.6, 3.6) * mm, "mid": v(35.17, 3.72) * mm, "end": v(35.65, 4.04) * mm});
            skLineSegment(sketch, "E707.0.MirrorCS", {"start": v(35.65, 4.04) * mm, "end": v(37.94, 6.32) * mm});
            skArc(sketch, "E708.0.MirrorCS", {"start": v(37.94, 6.32) * mm, "mid": v(38.17, 7.52) * mm, "end": v(37.16, 8.2) * mm});
            skLineSegment(sketch, "E709.0.MirrorCS", {"start": v(37.16, 8.2) * mm, "end": v(35.46, 8.2) * mm});
            skArc(sketch, "E710.0.MirrorCS", {"start": v(35.46, 8.2) * mm, "mid": v(35.29, 8.28) * mm, "end": v(35.21, 8.45) * mm});
            skLineSegment(sketch, "E711.0.MirrorCS", {"start": v(35.21, 8.45) * mm, "end": v(35.21, 9.5) * mm});
            skArc(sketch, "E712.0.MirrorCS", {"start": v(35.21, 9.5) * mm, "mid": v(35.36, 9.86) * mm, "end": v(35.71, 10) * mm});
            skLineSegment(sketch, "E713.0.MirrorCS", {"start": v(35.71, 10) * mm, "end": v(41.21, 10) * mm});
            skArc(sketch, "E714.0.MirrorCS", {"start": v(41.21, 10) * mm, "mid": v(42.27, 9.56) * mm, "end": v(42.71, 8.5) * mm});
            skLineSegment(sketch, "E715.0.MirrorCS", {"start": v(42.71, 8.5) * mm, "end": v(42.71, 3) * mm});
            skArc(sketch, "E716.0.MirrorCS", {"start": v(42.71, 3) * mm, "mid": v(42.57, 2.65) * mm, "end": v(42.21, 2.5) * mm});
            skLineSegment(sketch, "E717.0.MirrorCS", {"start": v(42.21, 2.5) * mm, "end": v(41.16, 2.5) * mm});
            skArc(sketch, "E718.0.MirrorCS", {"start": v(41.16, 2.5) * mm, "mid": v(40.99, 2.58) * mm, "end": v(40.91, 2.75) * mm});
            skLineSegment(sketch, "E719.0.MirrorCS", {"start": v(40.91, 2.75) * mm, "end": v(40.91, 4.45) * mm});
            skArc(sketch, "E720.0.MirrorCS", {"start": v(40.91, 4.45) * mm, "mid": v(40.23, 5.46) * mm, "end": v(39.04, 5.22) * mm});
            skLineSegment(sketch, "E721.0.MirrorCS", {"start": v(39.04, 5.22) * mm, "end": v(36.75, 2.94) * mm});
            skArc(sketch, "E722.0.MirrorCS", {"start": v(36.75, 2.94) * mm, "mid": v(36.43, 2.45) * mm, "end": v(36.31, 1.88) * mm});
            skLineSegment(sketch, "E723.0.MirrorCS", {"start": v(36.31, 1.88) * mm, "end": v(36.31, -1.88) * mm});
            skArc(sketch, "E724.0.MirrorCS", {"start": v(36.31, -1.88) * mm, "mid": v(36.43, -2.45) * mm, "end": v(36.75, -2.94) * mm});
            skLineSegment(sketch, "E725.0.MirrorCS", {"start": v(36.75, -2.94) * mm, "end": v(39.04, -5.22) * mm});
            skArc(sketch, "E726.0.MirrorCS", {"start": v(39.04, -5.22) * mm, "mid": v(40.23, -5.46) * mm, "end": v(40.91, -4.44) * mm});
            skLineSegment(sketch, "E727.0.MirrorCS", {"start": v(40.91, -4.44) * mm, "end": v(40.91, -2.75) * mm});
            skArc(sketch, "E728.0.MirrorCS", {"start": v(40.91, -2.75) * mm, "mid": v(40.99, -2.57) * mm, "end": v(41.16, -2.5) * mm});
            skLineSegment(sketch, "E729.0.MirrorCS", {"start": v(41.16, -2.5) * mm, "end": v(42.21, -2.5) * mm});
            skArc(sketch, "E730.0.MirrorCS", {"start": v(42.21, -2.5) * mm, "mid": v(42.57, -2.64) * mm, "end": v(42.71, -3) * mm});
            skLineSegment(sketch, "E731.0.MirrorCS", {"start": v(42.71, -3) * mm, "end": v(42.71, -17) * mm});
            skArc(sketch, "E732.0.MirrorCS", {"start": v(42.71, -17) * mm, "mid": v(42.57, -17.35) * mm, "end": v(42.21, -17.5) * mm});
            skLineSegment(sketch, "E733.0.MirrorCS", {"start": v(42.21, -17.5) * mm, "end": v(41.16, -17.5) * mm});
            skArc(sketch, "E734.0.MirrorCS", {"start": v(41.16, -17.5) * mm, "mid": v(40.99, -17.42) * mm, "end": v(40.91, -17.25) * mm});
            skLineSegment(sketch, "E735.0.MirrorCS", {"start": v(40.91, -17.25) * mm, "end": v(40.91, -15.55) * mm});
            skArc(sketch, "E736.0.MirrorCS", {"start": v(40.91, -15.55) * mm, "mid": v(40.23, -14.54) * mm, "end": v(39.04, -14.78) * mm});
            skLineSegment(sketch, "E737.0.MirrorCS", {"start": v(39.04, -14.78) * mm, "end": v(36.75, -17.06) * mm});
            skArc(sketch, "E738.0.MirrorCS", {"start": v(36.75, -17.06) * mm, "mid": v(36.43, -17.55) * mm, "end": v(36.31, -18.12) * mm});
            skLineSegment(sketch, "E739.0.MirrorCS", {"start": v(36.31, -18.12) * mm, "end": v(36.31, -21.88) * mm});
            skArc(sketch, "E740.0.MirrorCS", {"start": v(36.31, -21.88) * mm, "mid": v(36.43, -22.45) * mm, "end": v(36.75, -22.94) * mm});
            skLineSegment(sketch, "E741.0.MirrorCS", {"start": v(36.75, -22.94) * mm, "end": v(39.04, -25.22) * mm});
            skArc(sketch, "E742.0.MirrorCS", {"start": v(39.04, -25.22) * mm, "mid": v(40.23, -25.46) * mm, "end": v(40.91, -24.44) * mm});
            skLineSegment(sketch, "E743.0.MirrorCS", {"start": v(40.91, -24.44) * mm, "end": v(40.91, -22.75) * mm});
            skArc(sketch, "E744.0.MirrorCS", {"start": v(40.91, -22.75) * mm, "mid": v(40.99, -22.57) * mm, "end": v(41.16, -22.5) * mm});
            skLineSegment(sketch, "E745.0.MirrorCS", {"start": v(41.16, -22.5) * mm, "end": v(42.21, -22.5) * mm});
            skArc(sketch, "E746.0.MirrorCS", {"start": v(42.21, -22.5) * mm, "mid": v(42.57, -22.64) * mm, "end": v(42.71, -23) * mm});
            skLineSegment(sketch, "E747.0.MirrorCS", {"start": v(42.71, -23) * mm, "end": v(42.71, -28.5) * mm});
            skArc(sketch, "E748.0.MirrorCS", {"start": v(42.71, -28.5) * mm, "mid": v(42.27, -29.56) * mm, "end": v(41.21, -30) * mm});
            skLineSegment(sketch, "E749.0.MirrorCS", {"start": v(41.21, -30) * mm, "end": v(35.71, -30) * mm});
            skArc(sketch, "E750.0.MirrorCS", {"start": v(35.71, -30) * mm, "mid": v(35.36, -29.85) * mm, "end": v(35.21, -29.5) * mm});
            skLineSegment(sketch, "E751.0.MirrorCS", {"start": v(35.21, -29.5) * mm, "end": v(35.21, -28.45) * mm});
            skArc(sketch, "E752.0.MirrorCS", {"start": v(35.21, -28.45) * mm, "mid": v(35.29, -28.27) * mm, "end": v(35.46, -28.2) * mm});
            skLineSegment(sketch, "E753.0.MirrorCS", {"start": v(35.46, -28.2) * mm, "end": v(37.16, -28.2) * mm});
            skArc(sketch, "E754.0.MirrorCS", {"start": v(37.16, -28.2) * mm, "mid": v(38.17, -27.52) * mm, "end": v(37.94, -26.32) * mm});
            skLineSegment(sketch, "E755.0.MirrorCS", {"start": v(37.94, -26.32) * mm, "end": v(35.65, -24.04) * mm});
            skArc(sketch, "E756.0.MirrorCS", {"start": v(35.65, -24.04) * mm, "mid": v(35.17, -23.71) * mm, "end": v(34.6, -23.6) * mm});
            skLineSegment(sketch, "E757.0.MirrorCS", {"start": v(34.6, -23.6) * mm, "end": v(30.84, -23.6) * mm});
            skArc(sketch, "E758.0.MirrorCS", {"start": v(30.84, -23.6) * mm, "mid": v(30.26, -23.71) * mm, "end": v(29.77, -24.04) * mm});
            skLineSegment(sketch, "E759.0.MirrorCS", {"start": v(29.77, -24.04) * mm, "end": v(27.5, -26.32) * mm});
            skArc(sketch, "E760.0.MirrorCS", {"start": v(27.5, -26.32) * mm, "mid": v(27.25, -27.52) * mm, "end": v(28.27, -28.2) * mm});
            skLineSegment(sketch, "E761.0.MirrorCS", {"start": v(28.27, -28.2) * mm, "end": v(29.96, -28.2) * mm});
            skArc(sketch, "E762.0.MirrorCS", {"start": v(29.96, -28.2) * mm, "mid": v(30.14, -28.27) * mm, "end": v(30.21, -28.45) * mm});
            skLineSegment(sketch, "E763.0.MirrorCS", {"start": v(30.21, -28.45) * mm, "end": v(30.21, -29.5) * mm});
            skArc(sketch, "E764.0.MirrorCS", {"start": v(30.21, -29.5) * mm, "mid": v(30.07, -29.85) * mm, "end": v(29.71, -30) * mm});
            skCircle(sketch, "E765.0.MirrorC", {"center": v(32.71, 0) * mm, "radius": 2.15 * mm});
            skCircle(sketch, "E766.0.MirrorC", {"center": v(32.71, -20) * mm, "radius": 2.15 * mm});
            skArc(sketch, "E767.0.MirrorCS", {"start": v(21.57, 7.76) * mm, "mid": v(22.06, 8.09) * mm, "end": v(22.64, 8.2) * mm});
            skLineSegment(sketch, "E768.0.MirrorCS", {"start": v(22.64, 8.2) * mm, "end": v(22.8, 8.2) * mm});
            skArc(sketch, "E769.0.MirrorCS", {"start": v(22.8, 8.2) * mm, "mid": v(23.37, 8.09) * mm, "end": v(23.85, 7.76) * mm});
            skLineSegment(sketch, "E770.0.MirrorCS", {"start": v(23.85, 7.76) * mm, "end": v(28.67, 2.94) * mm});
            skArc(sketch, "E771.0.MirrorCS", {"start": v(28.67, 2.94) * mm, "mid": v(29, 2.45) * mm, "end": v(29.11, 1.88) * mm});
            skLineSegment(sketch, "E772.0.MirrorCS", {"start": v(29.11, 1.88) * mm, "end": v(29.11, -1.88) * mm});
            skArc(sketch, "E773.0.MirrorCS", {"start": v(22.64, -28.2) * mm, "mid": v(22.06, -28.08) * mm, "end": v(21.57, -27.76) * mm});
            skLineSegment(sketch, "E774.0.MirrorCS", {"start": v(22.8, -28.2) * mm, "end": v(22.64, -28.2) * mm});
            skArc(sketch, "E775.0.MirrorCS", {"start": v(23.85, -27.76) * mm, "mid": v(23.37, -28.08) * mm, "end": v(22.8, -28.2) * mm});
            skLineSegment(sketch, "E776.0.MirrorCS", {"start": v(28.67, -22.94) * mm, "end": v(23.85, -27.76) * mm});
            skArc(sketch, "E777.0.MirrorCS", {"start": v(29.11, -21.88) * mm, "mid": v(29, -22.45) * mm, "end": v(28.67, -22.94) * mm});
            skLineSegment(sketch, "E778.0.MirrorCS", {"start": v(29.11, -18.12) * mm, "end": v(29.11, -21.88) * mm});
            skLineSegment(sketch, "E779.0.MirrorCS", {"start": v(30.84, -3.6) * mm, "end": v(34.6, -3.6) * mm});
            skArc(sketch, "E780.0.MirrorCS", {"start": v(34.6, -3.6) * mm, "mid": v(35.17, -3.71) * mm, "end": v(35.65, -4.04) * mm});
            skLineSegment(sketch, "E781.0.MirrorCS", {"start": v(35.65, -4.04) * mm, "end": v(40.47, -8.86) * mm});
            skArc(sketch, "E782.0.MirrorCS", {"start": v(40.47, -8.86) * mm, "mid": v(40.8, -9.35) * mm, "end": v(40.91, -9.92) * mm});
            skLineSegment(sketch, "E783.0.MirrorCS", {"start": v(40.91, -9.92) * mm, "end": v(40.91, -10.08) * mm});
            skArc(sketch, "E784.0.MirrorCS", {"start": v(40.91, -10.08) * mm, "mid": v(40.8, -10.65) * mm, "end": v(40.47, -11.14) * mm});
            skLineSegment(sketch, "E785.0.MirrorCS", {"start": v(40.47, -11.14) * mm, "end": v(35.65, -15.96) * mm});
            skArc(sketch, "E786.0.MirrorCS", {"start": v(35.65, -15.96) * mm, "mid": v(35.17, -16.28) * mm, "end": v(34.6, -16.4) * mm});
            skLineSegment(sketch, "E787.0.MirrorCS", {"start": v(34.6, -16.4) * mm, "end": v(30.84, -16.4) * mm});
            skLineSegment(sketch, "E788.0.MirrorCS", {"start": v(23.85, -7.76) * mm, "end": v(28.67, -2.94) * mm});
            skLineSegment(sketch, "E789.0.MirrorCS", {"start": v(16.75, -2.94) * mm, "end": v(21.57, -7.76) * mm});
            skArc(sketch, "E790.0.MirrorCS", {"start": v(23.85, -7.76) * mm, "mid": v(23.37, -8.08) * mm, "end": v(22.8, -8.2) * mm});
            skArc(sketch, "E791.0.MirrorCS", {"start": v(22.64, -8.2) * mm, "mid": v(22.06, -8.08) * mm, "end": v(21.57, -7.76) * mm});
            skLineSegment(sketch, "E792.0.MirrorCS", {"start": v(22.64, -8.2) * mm, "end": v(22.8, -8.2) * mm});
            skArc(sketch, "E793.0.MirrorCS", {"start": v(29.11, -1.88) * mm, "mid": v(29, -2.45) * mm, "end": v(28.67, -2.94) * mm});
            skLineSegment(sketch, "E794.0.MirrorCS", {"start": v(16.75, -17.06) * mm, "end": v(21.57, -12.24) * mm});
            skLineSegment(sketch, "E795.0.MirrorCS", {"start": v(23.85, -12.24) * mm, "end": v(28.67, -17.06) * mm});
            skArc(sketch, "E796.0.MirrorCS", {"start": v(29.11, -18.12) * mm, "mid": v(29, -17.55) * mm, "end": v(28.67, -17.06) * mm});
            skArc(sketch, "E797.0.MirrorCS", {"start": v(22.64, -11.8) * mm, "mid": v(22.06, -11.91) * mm, "end": v(21.57, -12.24) * mm});
            skArc(sketch, "E798.0.MirrorCS", {"start": v(23.85, -12.24) * mm, "mid": v(23.37, -11.91) * mm, "end": v(22.8, -11.8) * mm});
            skLineSegment(sketch, "E799.0.MirrorCS", {"start": v(22.64, -11.8) * mm, "end": v(22.8, -11.8) * mm});
            skLineSegment(sketch, "E800", {"start": v(32.71, 13.24) * mm, "end": v(32.71, -32.64) * mm, "construction": true});
            skArc(sketch, "E801.0.MirrorCS", {"start": v(30.84, -3.6) * mm, "mid": v(30.26, -3.71) * mm, "end": v(29.77, -4.04) * mm});
            skLineSegment(sketch, "E802.0.MirrorCS", {"start": v(29.77, -4.04) * mm, "end": v(24.95, -8.86) * mm});
            skArc(sketch, "E803.0.MirrorCS", {"start": v(24.95, -8.86) * mm, "mid": v(24.63, -9.35) * mm, "end": v(24.51, -9.92) * mm});
            skLineSegment(sketch, "E804.0.MirrorCS", {"start": v(24.51, -9.92) * mm, "end": v(24.51, -10.08) * mm});
            skArc(sketch, "E805.0.MirrorCS", {"start": v(24.51, -10.08) * mm, "mid": v(24.63, -10.65) * mm, "end": v(24.95, -11.14) * mm});
            skLineSegment(sketch, "E806.0.MirrorCS", {"start": v(24.95, -11.14) * mm, "end": v(29.77, -15.96) * mm});
            skArc(sketch, "E807.0.MirrorCS", {"start": v(29.77, -15.96) * mm, "mid": v(30.26, -16.28) * mm, "end": v(30.84, -16.4) * mm});
            skSolve(sketch);
        }
        {
            var Q0;
            Q0=qSketchRegion(id+"F1",true);
            extrude(context, id + "F8", {"entities" : qUnion([Q0]), "depth" : 500 * mm});
        }
        {
            var Q0;
            Q0=qSketchRegion(id+"F2",true);
            extrude(context, id + "F9", {"entities" : qUnion([Q0]), "depth" : 450 * mm});
        }
        {
            var Q0;
            Q0=qSketchRegion(id+"F3",true);
            extrude(context, id + "F10", {"entities" : qUnion([Q0]), "depth" : 400 * mm});
        }
        {
            var Q0;
            Q0=qSketchRegion(id+"F4",true);
            extrude(context, id + "F11", {"entities" : qUnion([Q0]), "depth" : 350 * mm});
        }
        {
            var Q0;
            Q0=qSketchRegion(id+"F5",true);
            extrude(context, id + "F12", {"entities" : qUnion([Q0]), "depth" : 300 * mm});
        }
        {
            var Q0;
            Q0=qSketchRegion(id+"F6",true);
            extrude(context, id + "F13", {"entities" : qUnion([Q0]), "depth" : 250 * mm});
        }
        {
            var Q0;
            Q0=qSketchRegion(id+"F7",true);
            extrude(context, id + "F14", {"entities" : qUnion([Q0]), "depth" : 200 * mm});
        }
    });
